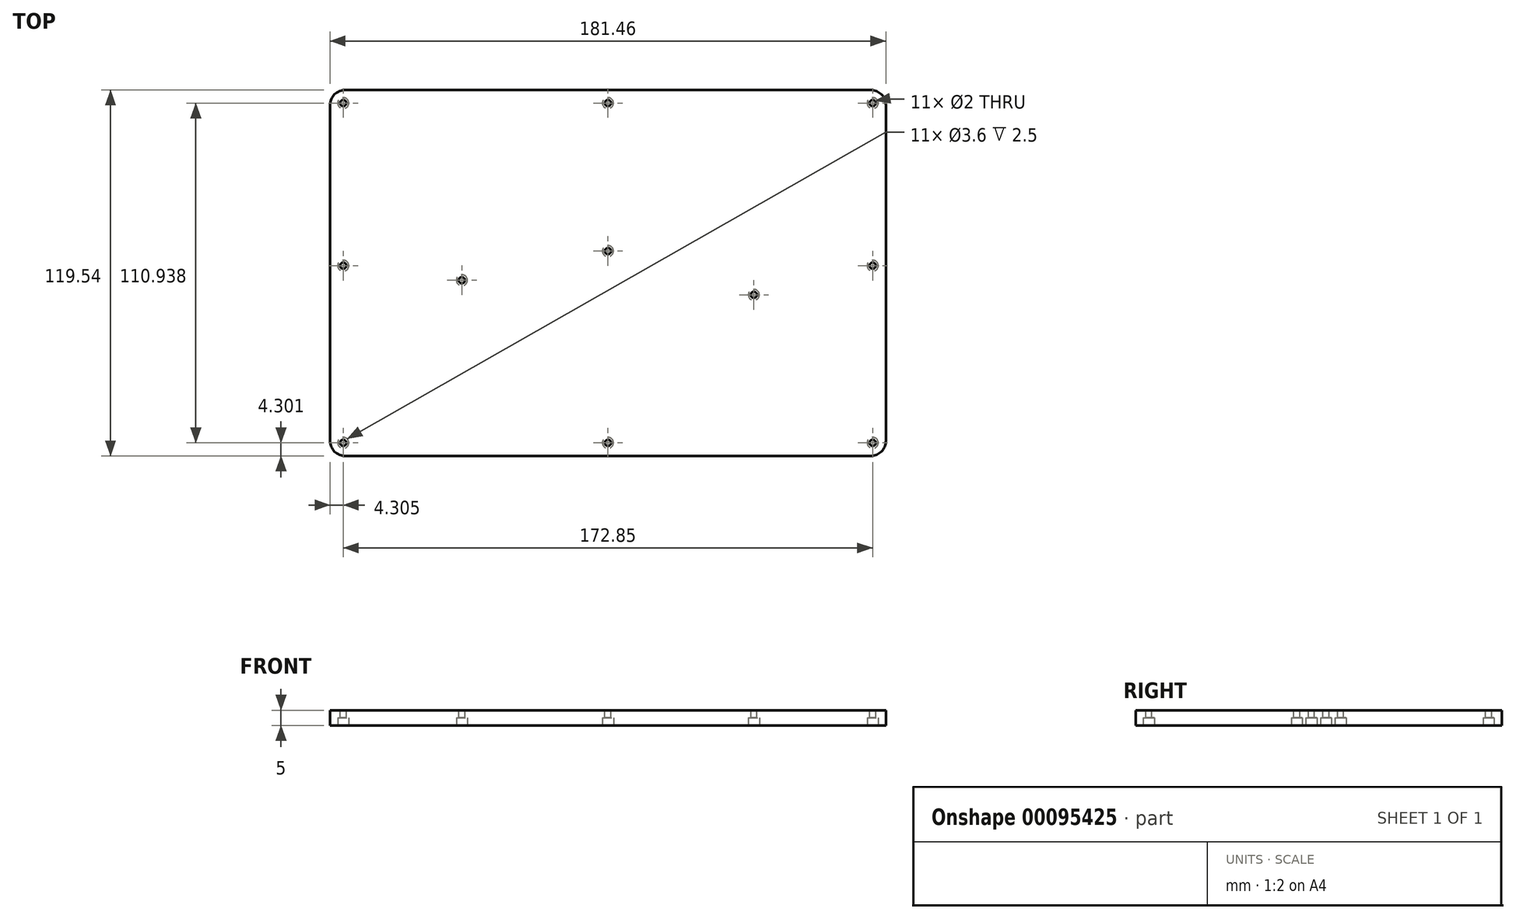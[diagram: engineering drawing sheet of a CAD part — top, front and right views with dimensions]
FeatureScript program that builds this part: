
annotation { "Feature Type Name" : "Feature", "Feature Type Description" : "" }
export const myFeature = defineFeature(function(context is Context, id is Id, definition is map)
    precondition{}
    {
        {
            var Q0;
            Q0=qCreatedBy(makeId("Top.planeOp"),FACE);
            var sketch = newSketch(context, id + "F0", { "sketchPlane" : qUnion([Q0])});
            skLineSegment(sketch, "E0", {"start": v(-90.73, 59.77) * mm, "end": v(90.73, 59.77) * mm});
            skLineSegment(sketch, "E1", {"start": v(90.73, 59.77) * mm, "end": v(90.73, -59.77) * mm});
            skLineSegment(sketch, "E2", {"start": v(90.73, -59.77) * mm, "end": v(-90.73, -59.77) * mm});
            skLineSegment(sketch, "E3", {"start": v(-90.73, -59.77) * mm, "end": v(-90.73, 59.77) * mm});
            skLineSegment(sketch, "E4", {"start": v(-70.2, -42.72) * mm, "end": v(-70.2, -43.52) * mm});
            skLineSegment(sketch, "E5", {"start": v(-70.2, -43.52) * mm, "end": v(-71.47, -43.52) * mm});
            skLineSegment(sketch, "E6", {"start": v(-71.47, -43.52) * mm, "end": v(-71.47, -44.3) * mm});
            skLineSegment(sketch, "E7", {"start": v(-71.47, -44.3) * mm, "end": v(-70.67, -44.3) * mm});
            skLineSegment(sketch, "E8", {"start": v(-70.67, -44.3) * mm, "end": v(-70.67, -46.02) * mm});
            skLineSegment(sketch, "E9", {"start": v(-70.67, -46.02) * mm, "end": v(-69.75, -46.02) * mm});
            skLineSegment(sketch, "E10", {"start": v(-69.75, -46.02) * mm, "end": v(-69.75, -49.32) * mm});
            skLineSegment(sketch, "E11", {"start": v(-69.75, -49.32) * mm, "end": v(-70.67, -49.32) * mm});
            skLineSegment(sketch, "E12", {"start": v(-70.67, -49.32) * mm, "end": v(-70.67, -50.94) * mm});
            skLineSegment(sketch, "E13", {"start": v(-70.67, -50.94) * mm, "end": v(-73.9, -50.94) * mm});
            skLineSegment(sketch, "E14", {"start": v(-73.9, -50.94) * mm, "end": v(-73.9, -51.82) * mm});
            skLineSegment(sketch, "E15", {"start": v(-73.9, -51.82) * mm, "end": v(-76.7, -51.82) * mm});
            skLineSegment(sketch, "E16", {"start": v(-76.7, -51.82) * mm, "end": v(-76.7, -50.94) * mm});
            skLineSegment(sketch, "E17", {"start": v(-76.7, -50.94) * mm, "end": v(-82.97, -50.94) * mm});
            skLineSegment(sketch, "E18", {"start": v(-82.97, -50.94) * mm, "end": v(-82.97, -49.32) * mm});
            skLineSegment(sketch, "E19", {"start": v(-82.97, -49.32) * mm, "end": v(-83.95, -49.32) * mm});
            skLineSegment(sketch, "E20", {"start": v(-83.95, -49.32) * mm, "end": v(-83.95, -46.02) * mm});
            skLineSegment(sketch, "E21", {"start": v(-83.95, -46.02) * mm, "end": v(-82.97, -46.02) * mm});
            skLineSegment(sketch, "E22", {"start": v(-82.97, -46.02) * mm, "end": v(-82.97, -44.3) * mm});
            skLineSegment(sketch, "E23", {"start": v(-82.97, -44.3) * mm, "end": v(-82.17, -44.3) * mm});
            skLineSegment(sketch, "E24", {"start": v(-82.17, -44.3) * mm, "end": v(-82.17, -43.52) * mm});
            skLineSegment(sketch, "E25", {"start": v(-82.17, -43.52) * mm, "end": v(-82.2, -43.52) * mm});
            skLineSegment(sketch, "E26", {"start": v(-82.2, -43.52) * mm, "end": v(-82.2, -42.72) * mm});
            skLineSegment(sketch, "E27", {"start": v(-82.2, -42.72) * mm, "end": v(-83.2, -42.72) * mm});
            skLineSegment(sketch, "E28", {"start": v(-83.2, -42.72) * mm, "end": v(-83.2, -28.72) * mm});
            skLineSegment(sketch, "E29", {"start": v(-83.2, -28.72) * mm, "end": v(-82.2, -28.72) * mm});
            skLineSegment(sketch, "E30", {"start": v(-82.2, -28.72) * mm, "end": v(-82.2, -27.92) * mm});
            skLineSegment(sketch, "E31", {"start": v(-82.2, -27.92) * mm, "end": v(-82.17, -27.92) * mm});
            skLineSegment(sketch, "E32", {"start": v(-82.17, -27.92) * mm, "end": v(-82.17, -27.14) * mm});
            skLineSegment(sketch, "E33", {"start": v(-82.17, -27.14) * mm, "end": v(-82.97, -27.14) * mm});
            skLineSegment(sketch, "E34", {"start": v(-82.97, -27.14) * mm, "end": v(-82.97, -25.42) * mm});
            skLineSegment(sketch, "E35", {"start": v(-82.97, -25.42) * mm, "end": v(-83.95, -25.42) * mm});
            skLineSegment(sketch, "E36", {"start": v(-83.95, -25.42) * mm, "end": v(-83.95, -22.12) * mm});
            skLineSegment(sketch, "E37", {"start": v(-83.95, -22.12) * mm, "end": v(-82.97, -22.12) * mm});
            skLineSegment(sketch, "E38", {"start": v(-82.97, -22.12) * mm, "end": v(-82.97, -20.5) * mm});
            skLineSegment(sketch, "E39", {"start": v(-82.97, -20.5) * mm, "end": v(-76.7, -20.5) * mm});
            skLineSegment(sketch, "E40", {"start": v(-76.7, -20.5) * mm, "end": v(-76.7, -19.62) * mm});
            skLineSegment(sketch, "E41", {"start": v(-76.7, -19.62) * mm, "end": v(-73.9, -19.62) * mm});
            skLineSegment(sketch, "E42", {"start": v(-73.9, -19.62) * mm, "end": v(-73.9, -20.5) * mm});
            skLineSegment(sketch, "E43", {"start": v(-73.9, -20.5) * mm, "end": v(-70.67, -20.5) * mm});
            skLineSegment(sketch, "E44", {"start": v(-70.67, -20.5) * mm, "end": v(-70.67, -22.12) * mm});
            skLineSegment(sketch, "E45", {"start": v(-70.67, -22.12) * mm, "end": v(-69.75, -22.12) * mm});
            skLineSegment(sketch, "E46", {"start": v(-69.75, -22.12) * mm, "end": v(-69.75, -25.42) * mm});
            skLineSegment(sketch, "E47", {"start": v(-69.75, -25.42) * mm, "end": v(-70.67, -25.42) * mm});
            skLineSegment(sketch, "E48", {"start": v(-70.67, -25.42) * mm, "end": v(-70.67, -27.14) * mm});
            skLineSegment(sketch, "E49", {"start": v(-70.67, -27.14) * mm, "end": v(-71.47, -27.14) * mm});
            skLineSegment(sketch, "E50", {"start": v(-71.47, -27.14) * mm, "end": v(-71.47, -27.92) * mm});
            skLineSegment(sketch, "E51", {"start": v(-71.47, -27.92) * mm, "end": v(-70.2, -27.92) * mm});
            skLineSegment(sketch, "E52", {"start": v(-70.2, -27.92) * mm, "end": v(-70.2, -28.72) * mm});
            skLineSegment(sketch, "E53", {"start": v(-70.2, -28.72) * mm, "end": v(-69.2, -28.72) * mm});
            skLineSegment(sketch, "E54", {"start": v(-69.2, -28.72) * mm, "end": v(-69.2, -42.72) * mm});
            skLineSegment(sketch, "E55", {"start": v(-69.2, -42.72) * mm, "end": v(-70.2, -42.72) * mm});
            skLineSegment(sketch, "E56", {"start": v(-69.2, 24.96) * mm, "end": v(-69.2, 23.96) * mm});
            skLineSegment(sketch, "E57", {"start": v(-69.2, 23.96) * mm, "end": v(-83.2, 23.96) * mm});
            skLineSegment(sketch, "E58", {"start": v(-83.2, 23.96) * mm, "end": v(-83.2, 24.96) * mm});
            skLineSegment(sketch, "E59", {"start": v(-83.2, 24.96) * mm, "end": v(-84, 24.96) * mm});
            skLineSegment(sketch, "E60", {"start": v(-84, 24.96) * mm, "end": v(-84, 28.06) * mm});
            skLineSegment(sketch, "E61", {"start": v(-84, 28.06) * mm, "end": v(-83.2, 28.06) * mm});
            skLineSegment(sketch, "E62", {"start": v(-83.2, 28.06) * mm, "end": v(-83.2, 33.86) * mm});
            skLineSegment(sketch, "E63", {"start": v(-83.2, 33.86) * mm, "end": v(-84, 33.86) * mm});
            skLineSegment(sketch, "E64", {"start": v(-84, 33.86) * mm, "end": v(-84, 36.96) * mm});
            skLineSegment(sketch, "E65", {"start": v(-84, 36.96) * mm, "end": v(-83.2, 36.96) * mm});
            skLineSegment(sketch, "E66", {"start": v(-83.2, 36.96) * mm, "end": v(-83.2, 37.96) * mm});
            skLineSegment(sketch, "E67", {"start": v(-83.2, 37.96) * mm, "end": v(-69.2, 37.96) * mm});
            skLineSegment(sketch, "E68", {"start": v(-69.2, 37.96) * mm, "end": v(-69.2, 36.96) * mm});
            skLineSegment(sketch, "E69", {"start": v(-69.2, 36.96) * mm, "end": v(-68.4, 36.96) * mm});
            skLineSegment(sketch, "E70", {"start": v(-68.4, 36.96) * mm, "end": v(-68.4, 33.86) * mm});
            skLineSegment(sketch, "E71", {"start": v(-68.4, 33.86) * mm, "end": v(-69.2, 33.86) * mm});
            skLineSegment(sketch, "E72", {"start": v(-69.2, 33.86) * mm, "end": v(-69.2, 28.06) * mm});
            skLineSegment(sketch, "E73", {"start": v(-69.2, 28.06) * mm, "end": v(-68.4, 28.06) * mm});
            skLineSegment(sketch, "E74", {"start": v(-68.4, 28.06) * mm, "end": v(-68.4, 24.96) * mm});
            skLineSegment(sketch, "E75", {"start": v(-68.4, 24.96) * mm, "end": v(-69.2, 24.96) * mm});
            skLineSegment(sketch, "E76", {"start": v(-69.2, 5.9) * mm, "end": v(-69.2, 4.9) * mm});
            skLineSegment(sketch, "E77", {"start": v(-69.2, 4.9) * mm, "end": v(-83.2, 4.9) * mm});
            skLineSegment(sketch, "E78", {"start": v(-83.2, 4.9) * mm, "end": v(-83.2, 5.9) * mm});
            skLineSegment(sketch, "E79", {"start": v(-83.2, 5.9) * mm, "end": v(-84, 5.9) * mm});
            skLineSegment(sketch, "E80", {"start": v(-84, 5.9) * mm, "end": v(-84, 9) * mm});
            skLineSegment(sketch, "E81", {"start": v(-84, 9) * mm, "end": v(-83.2, 9) * mm});
            skLineSegment(sketch, "E82", {"start": v(-83.2, 9) * mm, "end": v(-83.2, 14.8) * mm});
            skLineSegment(sketch, "E83", {"start": v(-83.2, 14.8) * mm, "end": v(-84, 14.8) * mm});
            skLineSegment(sketch, "E84", {"start": v(-84, 14.8) * mm, "end": v(-84, 17.9) * mm});
            skLineSegment(sketch, "E85", {"start": v(-84, 17.9) * mm, "end": v(-83.2, 17.9) * mm});
            skLineSegment(sketch, "E86", {"start": v(-83.2, 17.9) * mm, "end": v(-83.2, 18.9) * mm});
            skLineSegment(sketch, "E87", {"start": v(-83.2, 18.9) * mm, "end": v(-69.2, 18.9) * mm});
            skLineSegment(sketch, "E88", {"start": v(-69.2, 18.9) * mm, "end": v(-69.2, 17.9) * mm});
            skLineSegment(sketch, "E89", {"start": v(-69.2, 17.9) * mm, "end": v(-68.4, 17.9) * mm});
            skLineSegment(sketch, "E90", {"start": v(-68.4, 17.9) * mm, "end": v(-68.4, 14.8) * mm});
            skLineSegment(sketch, "E91", {"start": v(-68.4, 14.8) * mm, "end": v(-69.2, 14.8) * mm});
            skLineSegment(sketch, "E92", {"start": v(-69.2, 14.8) * mm, "end": v(-69.2, 9) * mm});
            skLineSegment(sketch, "E93", {"start": v(-69.2, 9) * mm, "end": v(-68.4, 9) * mm});
            skLineSegment(sketch, "E94", {"start": v(-68.4, 9) * mm, "end": v(-68.4, 5.9) * mm});
            skLineSegment(sketch, "E95", {"start": v(-68.4, 5.9) * mm, "end": v(-69.2, 5.9) * mm});
            skLineSegment(sketch, "E96", {"start": v(-69.2, -13.14) * mm, "end": v(-69.2, -14.14) * mm});
            skLineSegment(sketch, "E97", {"start": v(-69.2, -14.14) * mm, "end": v(-83.2, -14.14) * mm});
            skLineSegment(sketch, "E98", {"start": v(-83.2, -14.14) * mm, "end": v(-83.2, -13.14) * mm});
            skLineSegment(sketch, "E99", {"start": v(-83.2, -13.14) * mm, "end": v(-84, -13.14) * mm});
            skLineSegment(sketch, "E100", {"start": v(-84, -13.14) * mm, "end": v(-84, -10.04) * mm});
            skLineSegment(sketch, "E101", {"start": v(-84, -10.04) * mm, "end": v(-83.2, -10.04) * mm});
            skLineSegment(sketch, "E102", {"start": v(-83.2, -10.04) * mm, "end": v(-83.2, -4.24) * mm});
            skLineSegment(sketch, "E103", {"start": v(-83.2, -4.24) * mm, "end": v(-84, -4.24) * mm});
            skLineSegment(sketch, "E104", {"start": v(-84, -4.24) * mm, "end": v(-84, -1.14) * mm});
            skLineSegment(sketch, "E105", {"start": v(-84, -1.14) * mm, "end": v(-83.2, -1.14) * mm});
            skLineSegment(sketch, "E106", {"start": v(-83.2, -1.14) * mm, "end": v(-83.2, -0.14) * mm});
            skLineSegment(sketch, "E107", {"start": v(-83.2, -0.14) * mm, "end": v(-69.2, -0.14) * mm});
            skLineSegment(sketch, "E108", {"start": v(-69.2, -0.14) * mm, "end": v(-69.2, -1.14) * mm});
            skLineSegment(sketch, "E109", {"start": v(-69.2, -1.14) * mm, "end": v(-68.4, -1.14) * mm});
            skLineSegment(sketch, "E110", {"start": v(-68.4, -1.14) * mm, "end": v(-68.4, -4.24) * mm});
            skLineSegment(sketch, "E111", {"start": v(-68.4, -4.24) * mm, "end": v(-69.2, -4.24) * mm});
            skLineSegment(sketch, "E112", {"start": v(-69.2, -4.24) * mm, "end": v(-69.2, -10.04) * mm});
            skLineSegment(sketch, "E113", {"start": v(-69.2, -10.04) * mm, "end": v(-68.4, -10.04) * mm});
            skLineSegment(sketch, "E114", {"start": v(-68.4, -10.04) * mm, "end": v(-68.4, -13.14) * mm});
            skLineSegment(sketch, "E115", {"start": v(-68.4, -13.14) * mm, "end": v(-69.2, -13.14) * mm});
            skLineSegment(sketch, "E116", {"start": v(-50.15, 29.72) * mm, "end": v(-50.15, 28.72) * mm});
            skLineSegment(sketch, "E117", {"start": v(-50.15, 28.72) * mm, "end": v(-64.15, 28.72) * mm});
            skLineSegment(sketch, "E118", {"start": v(-64.15, 28.72) * mm, "end": v(-64.15, 29.72) * mm});
            skLineSegment(sketch, "E119", {"start": v(-64.15, 29.72) * mm, "end": v(-64.95, 29.72) * mm});
            skLineSegment(sketch, "E120", {"start": v(-64.95, 29.72) * mm, "end": v(-64.95, 32.82) * mm});
            skLineSegment(sketch, "E121", {"start": v(-64.95, 32.82) * mm, "end": v(-64.15, 32.82) * mm});
            skLineSegment(sketch, "E122", {"start": v(-64.15, 32.82) * mm, "end": v(-64.15, 38.62) * mm});
            skLineSegment(sketch, "E123", {"start": v(-64.15, 38.62) * mm, "end": v(-64.95, 38.62) * mm});
            skLineSegment(sketch, "E124", {"start": v(-64.95, 38.62) * mm, "end": v(-64.95, 41.72) * mm});
            skLineSegment(sketch, "E125", {"start": v(-64.95, 41.72) * mm, "end": v(-64.15, 41.72) * mm});
            skLineSegment(sketch, "E126", {"start": v(-64.15, 41.72) * mm, "end": v(-64.15, 42.72) * mm});
            skLineSegment(sketch, "E127", {"start": v(-64.15, 42.72) * mm, "end": v(-50.15, 42.72) * mm});
            skLineSegment(sketch, "E128", {"start": v(-50.15, 42.72) * mm, "end": v(-50.15, 41.72) * mm});
            skLineSegment(sketch, "E129", {"start": v(-50.15, 41.72) * mm, "end": v(-49.35, 41.72) * mm});
            skLineSegment(sketch, "E130", {"start": v(-49.35, 41.72) * mm, "end": v(-49.35, 38.62) * mm});
            skLineSegment(sketch, "E131", {"start": v(-49.35, 38.62) * mm, "end": v(-50.15, 38.62) * mm});
            skLineSegment(sketch, "E132", {"start": v(-50.15, 38.62) * mm, "end": v(-50.15, 32.82) * mm});
            skLineSegment(sketch, "E133", {"start": v(-50.15, 32.82) * mm, "end": v(-49.35, 32.82) * mm});
            skLineSegment(sketch, "E134", {"start": v(-49.35, 32.82) * mm, "end": v(-49.35, 29.72) * mm});
            skLineSegment(sketch, "E135", {"start": v(-49.35, 29.72) * mm, "end": v(-50.15, 29.72) * mm});
            skLineSegment(sketch, "E136", {"start": v(-50.15, 10.67) * mm, "end": v(-50.15, 9.67) * mm});
            skLineSegment(sketch, "E137", {"start": v(-50.15, 9.67) * mm, "end": v(-64.15, 9.67) * mm});
            skLineSegment(sketch, "E138", {"start": v(-64.15, 9.67) * mm, "end": v(-64.15, 10.67) * mm});
            skLineSegment(sketch, "E139", {"start": v(-64.15, 10.67) * mm, "end": v(-64.95, 10.67) * mm});
            skLineSegment(sketch, "E140", {"start": v(-64.95, 10.67) * mm, "end": v(-64.95, 13.77) * mm});
            skLineSegment(sketch, "E141", {"start": v(-64.95, 13.77) * mm, "end": v(-64.15, 13.77) * mm});
            skLineSegment(sketch, "E142", {"start": v(-64.15, 13.77) * mm, "end": v(-64.15, 19.57) * mm});
            skLineSegment(sketch, "E143", {"start": v(-64.15, 19.57) * mm, "end": v(-64.95, 19.57) * mm});
            skLineSegment(sketch, "E144", {"start": v(-64.95, 19.57) * mm, "end": v(-64.95, 22.67) * mm});
            skLineSegment(sketch, "E145", {"start": v(-64.95, 22.67) * mm, "end": v(-64.15, 22.67) * mm});
            skLineSegment(sketch, "E146", {"start": v(-64.15, 22.67) * mm, "end": v(-64.15, 23.67) * mm});
            skLineSegment(sketch, "E147", {"start": v(-64.15, 23.67) * mm, "end": v(-50.15, 23.67) * mm});
            skLineSegment(sketch, "E148", {"start": v(-50.15, 23.67) * mm, "end": v(-50.15, 22.67) * mm});
            skLineSegment(sketch, "E149", {"start": v(-50.15, 22.67) * mm, "end": v(-49.35, 22.67) * mm});
            skLineSegment(sketch, "E150", {"start": v(-49.35, 22.67) * mm, "end": v(-49.35, 19.57) * mm});
            skLineSegment(sketch, "E151", {"start": v(-49.35, 19.57) * mm, "end": v(-50.15, 19.57) * mm});
            skLineSegment(sketch, "E152", {"start": v(-50.15, 19.57) * mm, "end": v(-50.15, 13.77) * mm});
            skLineSegment(sketch, "E153", {"start": v(-50.15, 13.77) * mm, "end": v(-49.35, 13.77) * mm});
            skLineSegment(sketch, "E154", {"start": v(-49.35, 13.77) * mm, "end": v(-49.35, 10.67) * mm});
            skLineSegment(sketch, "E155", {"start": v(-49.35, 10.67) * mm, "end": v(-50.15, 10.67) * mm});
            skLineSegment(sketch, "E156", {"start": v(-50.15, -8.38) * mm, "end": v(-50.15, -9.38) * mm});
            skLineSegment(sketch, "E157", {"start": v(-50.15, -9.38) * mm, "end": v(-64.15, -9.38) * mm});
            skLineSegment(sketch, "E158", {"start": v(-64.15, -9.38) * mm, "end": v(-64.15, -8.38) * mm});
            skLineSegment(sketch, "E159", {"start": v(-64.15, -8.38) * mm, "end": v(-64.95, -8.38) * mm});
            skLineSegment(sketch, "E160", {"start": v(-64.95, -8.38) * mm, "end": v(-64.95, -5.28) * mm});
            skLineSegment(sketch, "E161", {"start": v(-64.95, -5.28) * mm, "end": v(-64.15, -5.28) * mm});
            skLineSegment(sketch, "E162", {"start": v(-64.15, -5.28) * mm, "end": v(-64.15, 0.52) * mm});
            skLineSegment(sketch, "E163", {"start": v(-64.15, 0.52) * mm, "end": v(-64.95, 0.52) * mm});
            skLineSegment(sketch, "E164", {"start": v(-64.95, 0.52) * mm, "end": v(-64.95, 3.62) * mm});
            skLineSegment(sketch, "E165", {"start": v(-64.95, 3.62) * mm, "end": v(-64.15, 3.62) * mm});
            skLineSegment(sketch, "E166", {"start": v(-64.15, 3.62) * mm, "end": v(-64.15, 4.62) * mm});
            skLineSegment(sketch, "E167", {"start": v(-64.15, 4.62) * mm, "end": v(-50.15, 4.62) * mm});
            skLineSegment(sketch, "E168", {"start": v(-50.15, 4.62) * mm, "end": v(-50.15, 3.62) * mm});
            skLineSegment(sketch, "E169", {"start": v(-50.15, 3.62) * mm, "end": v(-49.35, 3.62) * mm});
            skLineSegment(sketch, "E170", {"start": v(-49.35, 3.62) * mm, "end": v(-49.35, 0.52) * mm});
            skLineSegment(sketch, "E171", {"start": v(-49.35, 0.52) * mm, "end": v(-50.15, 0.52) * mm});
            skLineSegment(sketch, "E172", {"start": v(-50.15, 0.52) * mm, "end": v(-50.15, -5.28) * mm});
            skLineSegment(sketch, "E173", {"start": v(-50.15, -5.28) * mm, "end": v(-49.35, -5.28) * mm});
            skLineSegment(sketch, "E174", {"start": v(-49.35, -5.28) * mm, "end": v(-49.35, -8.38) * mm});
            skLineSegment(sketch, "E175", {"start": v(-49.35, -8.38) * mm, "end": v(-50.15, -8.38) * mm});
            skLineSegment(sketch, "E176", {"start": v(-50.15, -27.43) * mm, "end": v(-50.15, -28.43) * mm});
            skLineSegment(sketch, "E177", {"start": v(-50.15, -28.43) * mm, "end": v(-64.15, -28.43) * mm});
            skLineSegment(sketch, "E178", {"start": v(-64.15, -28.43) * mm, "end": v(-64.15, -27.43) * mm});
            skLineSegment(sketch, "E179", {"start": v(-64.15, -27.43) * mm, "end": v(-64.95, -27.43) * mm});
            skLineSegment(sketch, "E180", {"start": v(-64.95, -27.43) * mm, "end": v(-64.95, -24.33) * mm});
            skLineSegment(sketch, "E181", {"start": v(-64.95, -24.33) * mm, "end": v(-64.15, -24.33) * mm});
            skLineSegment(sketch, "E182", {"start": v(-64.15, -24.33) * mm, "end": v(-64.15, -18.53) * mm});
            skLineSegment(sketch, "E183", {"start": v(-64.15, -18.53) * mm, "end": v(-64.95, -18.53) * mm});
            skLineSegment(sketch, "E184", {"start": v(-64.95, -18.53) * mm, "end": v(-64.95, -15.43) * mm});
            skLineSegment(sketch, "E185", {"start": v(-64.95, -15.43) * mm, "end": v(-64.15, -15.43) * mm});
            skLineSegment(sketch, "E186", {"start": v(-64.15, -15.43) * mm, "end": v(-64.15, -14.43) * mm});
            skLineSegment(sketch, "E187", {"start": v(-64.15, -14.43) * mm, "end": v(-50.15, -14.43) * mm});
            skLineSegment(sketch, "E188", {"start": v(-50.15, -14.43) * mm, "end": v(-50.15, -15.43) * mm});
            skLineSegment(sketch, "E189", {"start": v(-50.15, -15.43) * mm, "end": v(-49.35, -15.43) * mm});
            skLineSegment(sketch, "E190", {"start": v(-49.35, -15.43) * mm, "end": v(-49.35, -18.53) * mm});
            skLineSegment(sketch, "E191", {"start": v(-49.35, -18.53) * mm, "end": v(-50.15, -18.53) * mm});
            skLineSegment(sketch, "E192", {"start": v(-50.15, -18.53) * mm, "end": v(-50.15, -24.33) * mm});
            skLineSegment(sketch, "E193", {"start": v(-50.15, -24.33) * mm, "end": v(-49.35, -24.33) * mm});
            skLineSegment(sketch, "E194", {"start": v(-49.35, -24.33) * mm, "end": v(-49.35, -27.43) * mm});
            skLineSegment(sketch, "E195", {"start": v(-49.35, -27.43) * mm, "end": v(-50.15, -27.43) * mm});
            skLineSegment(sketch, "E196", {"start": v(-50.15, -46.48) * mm, "end": v(-50.15, -47.48) * mm});
            skLineSegment(sketch, "E197", {"start": v(-50.15, -47.48) * mm, "end": v(-64.15, -47.48) * mm});
            skLineSegment(sketch, "E198", {"start": v(-64.15, -47.48) * mm, "end": v(-64.15, -46.48) * mm});
            skLineSegment(sketch, "E199", {"start": v(-64.15, -46.48) * mm, "end": v(-64.95, -46.48) * mm});
            skLineSegment(sketch, "E200", {"start": v(-64.95, -46.48) * mm, "end": v(-64.95, -43.38) * mm});
            skLineSegment(sketch, "E201", {"start": v(-64.95, -43.38) * mm, "end": v(-64.15, -43.38) * mm});
            skLineSegment(sketch, "E202", {"start": v(-64.15, -43.38) * mm, "end": v(-64.15, -37.58) * mm});
            skLineSegment(sketch, "E203", {"start": v(-64.15, -37.58) * mm, "end": v(-64.95, -37.58) * mm});
            skLineSegment(sketch, "E204", {"start": v(-64.95, -37.58) * mm, "end": v(-64.95, -34.48) * mm});
            skLineSegment(sketch, "E205", {"start": v(-64.95, -34.48) * mm, "end": v(-64.15, -34.48) * mm});
            skLineSegment(sketch, "E206", {"start": v(-64.15, -34.48) * mm, "end": v(-64.15, -33.48) * mm});
            skLineSegment(sketch, "E207", {"start": v(-64.15, -33.48) * mm, "end": v(-50.15, -33.48) * mm});
            skLineSegment(sketch, "E208", {"start": v(-50.15, -33.48) * mm, "end": v(-50.15, -34.48) * mm});
            skLineSegment(sketch, "E209", {"start": v(-50.15, -34.48) * mm, "end": v(-49.35, -34.48) * mm});
            skLineSegment(sketch, "E210", {"start": v(-49.35, -34.48) * mm, "end": v(-49.35, -37.58) * mm});
            skLineSegment(sketch, "E211", {"start": v(-49.35, -37.58) * mm, "end": v(-50.15, -37.58) * mm});
            skLineSegment(sketch, "E212", {"start": v(-50.15, -37.58) * mm, "end": v(-50.15, -43.38) * mm});
            skLineSegment(sketch, "E213", {"start": v(-50.15, -43.38) * mm, "end": v(-49.35, -43.38) * mm});
            skLineSegment(sketch, "E214", {"start": v(-49.35, -43.38) * mm, "end": v(-49.35, -46.48) * mm});
            skLineSegment(sketch, "E215", {"start": v(-49.35, -46.48) * mm, "end": v(-50.15, -46.48) * mm});
            skLineSegment(sketch, "E216", {"start": v(-31.1, 39.24) * mm, "end": v(-31.1, 38.24) * mm});
            skLineSegment(sketch, "E217", {"start": v(-31.1, 38.24) * mm, "end": v(-45.1, 38.24) * mm});
            skLineSegment(sketch, "E218", {"start": v(-45.1, 38.24) * mm, "end": v(-45.1, 39.24) * mm});
            skLineSegment(sketch, "E219", {"start": v(-45.1, 39.24) * mm, "end": v(-45.9, 39.24) * mm});
            skLineSegment(sketch, "E220", {"start": v(-45.9, 39.24) * mm, "end": v(-45.9, 42.34) * mm});
            skLineSegment(sketch, "E221", {"start": v(-45.9, 42.34) * mm, "end": v(-45.1, 42.34) * mm});
            skLineSegment(sketch, "E222", {"start": v(-45.1, 42.34) * mm, "end": v(-45.1, 48.14) * mm});
            skLineSegment(sketch, "E223", {"start": v(-45.1, 48.14) * mm, "end": v(-45.9, 48.14) * mm});
            skLineSegment(sketch, "E224", {"start": v(-45.9, 48.14) * mm, "end": v(-45.9, 51.24) * mm});
            skLineSegment(sketch, "E225", {"start": v(-45.9, 51.24) * mm, "end": v(-45.1, 51.24) * mm});
            skLineSegment(sketch, "E226", {"start": v(-45.1, 51.24) * mm, "end": v(-45.1, 52.24) * mm});
            skLineSegment(sketch, "E227", {"start": v(-45.1, 52.24) * mm, "end": v(-31.1, 52.24) * mm});
            skLineSegment(sketch, "E228", {"start": v(-31.1, 52.24) * mm, "end": v(-31.1, 51.24) * mm});
            skLineSegment(sketch, "E229", {"start": v(-31.1, 51.24) * mm, "end": v(-30.3, 51.24) * mm});
            skLineSegment(sketch, "E230", {"start": v(-30.3, 51.24) * mm, "end": v(-30.3, 48.14) * mm});
            skLineSegment(sketch, "E231", {"start": v(-30.3, 48.14) * mm, "end": v(-31.1, 48.14) * mm});
            skLineSegment(sketch, "E232", {"start": v(-31.1, 48.14) * mm, "end": v(-31.1, 42.34) * mm});
            skLineSegment(sketch, "E233", {"start": v(-31.1, 42.34) * mm, "end": v(-30.3, 42.34) * mm});
            skLineSegment(sketch, "E234", {"start": v(-30.3, 42.34) * mm, "end": v(-30.3, 39.24) * mm});
            skLineSegment(sketch, "E235", {"start": v(-30.3, 39.24) * mm, "end": v(-31.1, 39.24) * mm});
            skLineSegment(sketch, "E236", {"start": v(-31.1, 20.2) * mm, "end": v(-31.1, 19.2) * mm});
            skLineSegment(sketch, "E237", {"start": v(-31.1, 19.2) * mm, "end": v(-45.1, 19.2) * mm});
            skLineSegment(sketch, "E238", {"start": v(-45.1, 19.2) * mm, "end": v(-45.1, 20.2) * mm});
            skLineSegment(sketch, "E239", {"start": v(-45.1, 20.2) * mm, "end": v(-45.9, 20.2) * mm});
            skLineSegment(sketch, "E240", {"start": v(-45.9, 20.2) * mm, "end": v(-45.9, 23.3) * mm});
            skLineSegment(sketch, "E241", {"start": v(-45.9, 23.3) * mm, "end": v(-45.1, 23.3) * mm});
            skLineSegment(sketch, "E242", {"start": v(-45.1, 23.3) * mm, "end": v(-45.1, 29.1) * mm});
            skLineSegment(sketch, "E243", {"start": v(-45.1, 29.1) * mm, "end": v(-45.9, 29.1) * mm});
            skLineSegment(sketch, "E244", {"start": v(-45.9, 29.1) * mm, "end": v(-45.9, 32.2) * mm});
            skLineSegment(sketch, "E245", {"start": v(-45.9, 32.2) * mm, "end": v(-45.1, 32.2) * mm});
            skLineSegment(sketch, "E246", {"start": v(-45.1, 32.2) * mm, "end": v(-45.1, 33.2) * mm});
            skLineSegment(sketch, "E247", {"start": v(-45.1, 33.2) * mm, "end": v(-31.1, 33.2) * mm});
            skLineSegment(sketch, "E248", {"start": v(-31.1, 33.2) * mm, "end": v(-31.1, 32.2) * mm});
            skLineSegment(sketch, "E249", {"start": v(-31.1, 32.2) * mm, "end": v(-30.3, 32.2) * mm});
            skLineSegment(sketch, "E250", {"start": v(-30.3, 32.2) * mm, "end": v(-30.3, 29.1) * mm});
            skLineSegment(sketch, "E251", {"start": v(-30.3, 29.1) * mm, "end": v(-31.1, 29.1) * mm});
            skLineSegment(sketch, "E252", {"start": v(-31.1, 29.1) * mm, "end": v(-31.1, 23.3) * mm});
            skLineSegment(sketch, "E253", {"start": v(-31.1, 23.3) * mm, "end": v(-30.3, 23.3) * mm});
            skLineSegment(sketch, "E254", {"start": v(-30.3, 23.3) * mm, "end": v(-30.3, 20.2) * mm});
            skLineSegment(sketch, "E255", {"start": v(-30.3, 20.2) * mm, "end": v(-31.1, 20.2) * mm});
            skLineSegment(sketch, "E256", {"start": v(-31.1, 1.14) * mm, "end": v(-31.1, 0.14) * mm});
            skLineSegment(sketch, "E257", {"start": v(-31.1, 0.14) * mm, "end": v(-45.1, 0.14) * mm});
            skLineSegment(sketch, "E258", {"start": v(-45.1, 0.14) * mm, "end": v(-45.1, 1.14) * mm});
            skLineSegment(sketch, "E259", {"start": v(-45.1, 1.14) * mm, "end": v(-45.9, 1.14) * mm});
            skLineSegment(sketch, "E260", {"start": v(-45.9, 1.14) * mm, "end": v(-45.9, 4.24) * mm});
            skLineSegment(sketch, "E261", {"start": v(-45.9, 4.24) * mm, "end": v(-45.1, 4.24) * mm});
            skLineSegment(sketch, "E262", {"start": v(-45.1, 4.24) * mm, "end": v(-45.1, 10.04) * mm});
            skLineSegment(sketch, "E263", {"start": v(-45.1, 10.04) * mm, "end": v(-45.9, 10.04) * mm});
            skLineSegment(sketch, "E264", {"start": v(-45.9, 10.04) * mm, "end": v(-45.9, 13.14) * mm});
            skLineSegment(sketch, "E265", {"start": v(-45.9, 13.14) * mm, "end": v(-45.1, 13.14) * mm});
            skLineSegment(sketch, "E266", {"start": v(-45.1, 13.14) * mm, "end": v(-45.1, 14.14) * mm});
            skLineSegment(sketch, "E267", {"start": v(-45.1, 14.14) * mm, "end": v(-31.1, 14.14) * mm});
            skLineSegment(sketch, "E268", {"start": v(-31.1, 14.14) * mm, "end": v(-31.1, 13.14) * mm});
            skLineSegment(sketch, "E269", {"start": v(-31.1, 13.14) * mm, "end": v(-30.3, 13.14) * mm});
            skLineSegment(sketch, "E270", {"start": v(-30.3, 13.14) * mm, "end": v(-30.3, 10.04) * mm});
            skLineSegment(sketch, "E271", {"start": v(-30.3, 10.04) * mm, "end": v(-31.1, 10.04) * mm});
            skLineSegment(sketch, "E272", {"start": v(-31.1, 10.04) * mm, "end": v(-31.1, 4.24) * mm});
            skLineSegment(sketch, "E273", {"start": v(-31.1, 4.24) * mm, "end": v(-30.3, 4.24) * mm});
            skLineSegment(sketch, "E274", {"start": v(-30.3, 4.24) * mm, "end": v(-30.3, 1.14) * mm});
            skLineSegment(sketch, "E275", {"start": v(-30.3, 1.14) * mm, "end": v(-31.1, 1.14) * mm});
            skLineSegment(sketch, "E276", {"start": v(-31.1, -17.9) * mm, "end": v(-31.1, -18.9) * mm});
            skLineSegment(sketch, "E277", {"start": v(-31.1, -18.9) * mm, "end": v(-45.1, -18.9) * mm});
            skLineSegment(sketch, "E278", {"start": v(-45.1, -18.9) * mm, "end": v(-45.1, -17.9) * mm});
            skLineSegment(sketch, "E279", {"start": v(-45.1, -17.9) * mm, "end": v(-45.9, -17.9) * mm});
            skLineSegment(sketch, "E280", {"start": v(-45.9, -17.9) * mm, "end": v(-45.9, -14.8) * mm});
            skLineSegment(sketch, "E281", {"start": v(-45.9, -14.8) * mm, "end": v(-45.1, -14.8) * mm});
            skLineSegment(sketch, "E282", {"start": v(-45.1, -14.8) * mm, "end": v(-45.1, -9) * mm});
            skLineSegment(sketch, "E283", {"start": v(-45.1, -9) * mm, "end": v(-45.9, -9) * mm});
            skLineSegment(sketch, "E284", {"start": v(-45.9, -9) * mm, "end": v(-45.9, -5.9) * mm});
            skLineSegment(sketch, "E285", {"start": v(-45.9, -5.9) * mm, "end": v(-45.1, -5.9) * mm});
            skLineSegment(sketch, "E286", {"start": v(-45.1, -5.9) * mm, "end": v(-45.1, -4.9) * mm});
            skLineSegment(sketch, "E287", {"start": v(-45.1, -4.9) * mm, "end": v(-31.1, -4.9) * mm});
            skLineSegment(sketch, "E288", {"start": v(-31.1, -4.9) * mm, "end": v(-31.1, -5.9) * mm});
            skLineSegment(sketch, "E289", {"start": v(-31.1, -5.9) * mm, "end": v(-30.3, -5.9) * mm});
            skLineSegment(sketch, "E290", {"start": v(-30.3, -5.9) * mm, "end": v(-30.3, -9) * mm});
            skLineSegment(sketch, "E291", {"start": v(-30.3, -9) * mm, "end": v(-31.1, -9) * mm});
            skLineSegment(sketch, "E292", {"start": v(-31.1, -9) * mm, "end": v(-31.1, -14.8) * mm});
            skLineSegment(sketch, "E293", {"start": v(-31.1, -14.8) * mm, "end": v(-30.3, -14.8) * mm});
            skLineSegment(sketch, "E294", {"start": v(-30.3, -14.8) * mm, "end": v(-30.3, -17.9) * mm});
            skLineSegment(sketch, "E295", {"start": v(-30.3, -17.9) * mm, "end": v(-31.1, -17.9) * mm});
            skLineSegment(sketch, "E296", {"start": v(-31.1, -36.96) * mm, "end": v(-31.1, -37.96) * mm});
            skLineSegment(sketch, "E297", {"start": v(-31.1, -37.96) * mm, "end": v(-45.1, -37.96) * mm});
            skLineSegment(sketch, "E298", {"start": v(-45.1, -37.96) * mm, "end": v(-45.1, -36.96) * mm});
            skLineSegment(sketch, "E299", {"start": v(-45.1, -36.96) * mm, "end": v(-45.9, -36.96) * mm});
            skLineSegment(sketch, "E300", {"start": v(-45.9, -36.96) * mm, "end": v(-45.9, -33.86) * mm});
            skLineSegment(sketch, "E301", {"start": v(-45.9, -33.86) * mm, "end": v(-45.1, -33.86) * mm});
            skLineSegment(sketch, "E302", {"start": v(-45.1, -33.86) * mm, "end": v(-45.1, -28.06) * mm});
            skLineSegment(sketch, "E303", {"start": v(-45.1, -28.06) * mm, "end": v(-45.9, -28.06) * mm});
            skLineSegment(sketch, "E304", {"start": v(-45.9, -28.06) * mm, "end": v(-45.9, -24.96) * mm});
            skLineSegment(sketch, "E305", {"start": v(-45.9, -24.96) * mm, "end": v(-45.1, -24.96) * mm});
            skLineSegment(sketch, "E306", {"start": v(-45.1, -24.96) * mm, "end": v(-45.1, -23.96) * mm});
            skLineSegment(sketch, "E307", {"start": v(-45.1, -23.96) * mm, "end": v(-31.1, -23.96) * mm});
            skLineSegment(sketch, "E308", {"start": v(-31.1, -23.96) * mm, "end": v(-31.1, -24.96) * mm});
            skLineSegment(sketch, "E309", {"start": v(-31.1, -24.96) * mm, "end": v(-30.3, -24.96) * mm});
            skLineSegment(sketch, "E310", {"start": v(-30.3, -24.96) * mm, "end": v(-30.3, -28.06) * mm});
            skLineSegment(sketch, "E311", {"start": v(-30.3, -28.06) * mm, "end": v(-31.1, -28.06) * mm});
            skLineSegment(sketch, "E312", {"start": v(-31.1, -28.06) * mm, "end": v(-31.1, -33.86) * mm});
            skLineSegment(sketch, "E313", {"start": v(-31.1, -33.86) * mm, "end": v(-30.3, -33.86) * mm});
            skLineSegment(sketch, "E314", {"start": v(-30.3, -33.86) * mm, "end": v(-30.3, -36.96) * mm});
            skLineSegment(sketch, "E315", {"start": v(-30.3, -36.96) * mm, "end": v(-31.1, -36.96) * mm});
            skLineSegment(sketch, "E316", {"start": v(-12.05, 34.48) * mm, "end": v(-12.05, 33.48) * mm});
            skLineSegment(sketch, "E317", {"start": v(-12.05, 33.48) * mm, "end": v(-26.05, 33.48) * mm});
            skLineSegment(sketch, "E318", {"start": v(-26.05, 33.48) * mm, "end": v(-26.05, 34.48) * mm});
            skLineSegment(sketch, "E319", {"start": v(-26.05, 34.48) * mm, "end": v(-26.85, 34.48) * mm});
            skLineSegment(sketch, "E320", {"start": v(-26.85, 34.48) * mm, "end": v(-26.85, 37.58) * mm});
            skLineSegment(sketch, "E321", {"start": v(-26.85, 37.58) * mm, "end": v(-26.05, 37.58) * mm});
            skLineSegment(sketch, "E322", {"start": v(-26.05, 37.58) * mm, "end": v(-26.05, 43.38) * mm});
            skLineSegment(sketch, "E323", {"start": v(-26.05, 43.38) * mm, "end": v(-26.85, 43.38) * mm});
            skLineSegment(sketch, "E324", {"start": v(-26.85, 43.38) * mm, "end": v(-26.85, 46.48) * mm});
            skLineSegment(sketch, "E325", {"start": v(-26.85, 46.48) * mm, "end": v(-26.05, 46.48) * mm});
            skLineSegment(sketch, "E326", {"start": v(-26.05, 46.48) * mm, "end": v(-26.05, 47.48) * mm});
            skLineSegment(sketch, "E327", {"start": v(-26.05, 47.48) * mm, "end": v(-12.05, 47.48) * mm});
            skLineSegment(sketch, "E328", {"start": v(-12.05, 47.48) * mm, "end": v(-12.05, 46.48) * mm});
            skLineSegment(sketch, "E329", {"start": v(-12.05, 46.48) * mm, "end": v(-11.25, 46.48) * mm});
            skLineSegment(sketch, "E330", {"start": v(-11.25, 46.48) * mm, "end": v(-11.25, 43.38) * mm});
            skLineSegment(sketch, "E331", {"start": v(-11.25, 43.38) * mm, "end": v(-12.05, 43.38) * mm});
            skLineSegment(sketch, "E332", {"start": v(-12.05, 43.38) * mm, "end": v(-12.05, 37.58) * mm});
            skLineSegment(sketch, "E333", {"start": v(-12.05, 37.58) * mm, "end": v(-11.25, 37.58) * mm});
            skLineSegment(sketch, "E334", {"start": v(-11.25, 37.58) * mm, "end": v(-11.25, 34.48) * mm});
            skLineSegment(sketch, "E335", {"start": v(-11.25, 34.48) * mm, "end": v(-12.05, 34.48) * mm});
            skLineSegment(sketch, "E336", {"start": v(-12.05, 15.43) * mm, "end": v(-12.05, 14.43) * mm});
            skLineSegment(sketch, "E337", {"start": v(-12.05, 14.43) * mm, "end": v(-26.05, 14.43) * mm});
            skLineSegment(sketch, "E338", {"start": v(-26.05, 14.43) * mm, "end": v(-26.05, 15.43) * mm});
            skLineSegment(sketch, "E339", {"start": v(-26.05, 15.43) * mm, "end": v(-26.85, 15.43) * mm});
            skLineSegment(sketch, "E340", {"start": v(-26.85, 15.43) * mm, "end": v(-26.85, 18.53) * mm});
            skLineSegment(sketch, "E341", {"start": v(-26.85, 18.53) * mm, "end": v(-26.05, 18.53) * mm});
            skLineSegment(sketch, "E342", {"start": v(-26.05, 18.53) * mm, "end": v(-26.05, 24.33) * mm});
            skLineSegment(sketch, "E343", {"start": v(-26.05, 24.33) * mm, "end": v(-26.85, 24.33) * mm});
            skLineSegment(sketch, "E344", {"start": v(-26.85, 24.33) * mm, "end": v(-26.85, 27.43) * mm});
            skLineSegment(sketch, "E345", {"start": v(-26.85, 27.43) * mm, "end": v(-26.05, 27.43) * mm});
            skLineSegment(sketch, "E346", {"start": v(-26.05, 27.43) * mm, "end": v(-26.05, 28.43) * mm});
            skLineSegment(sketch, "E347", {"start": v(-26.05, 28.43) * mm, "end": v(-12.05, 28.43) * mm});
            skLineSegment(sketch, "E348", {"start": v(-12.05, 28.43) * mm, "end": v(-12.05, 27.43) * mm});
            skLineSegment(sketch, "E349", {"start": v(-12.05, 27.43) * mm, "end": v(-11.25, 27.43) * mm});
            skLineSegment(sketch, "E350", {"start": v(-11.25, 27.43) * mm, "end": v(-11.25, 24.33) * mm});
            skLineSegment(sketch, "E351", {"start": v(-11.25, 24.33) * mm, "end": v(-12.05, 24.33) * mm});
            skLineSegment(sketch, "E352", {"start": v(-12.05, 24.33) * mm, "end": v(-12.05, 18.53) * mm});
            skLineSegment(sketch, "E353", {"start": v(-12.05, 18.53) * mm, "end": v(-11.25, 18.53) * mm});
            skLineSegment(sketch, "E354", {"start": v(-11.25, 18.53) * mm, "end": v(-11.25, 15.43) * mm});
            skLineSegment(sketch, "E355", {"start": v(-11.25, 15.43) * mm, "end": v(-12.05, 15.43) * mm});
            skLineSegment(sketch, "E356", {"start": v(-12.05, -3.62) * mm, "end": v(-12.05, -4.62) * mm});
            skLineSegment(sketch, "E357", {"start": v(-12.05, -4.62) * mm, "end": v(-26.05, -4.62) * mm});
            skLineSegment(sketch, "E358", {"start": v(-26.05, -4.62) * mm, "end": v(-26.05, -3.62) * mm});
            skLineSegment(sketch, "E359", {"start": v(-26.05, -3.62) * mm, "end": v(-26.85, -3.62) * mm});
            skLineSegment(sketch, "E360", {"start": v(-26.85, -3.62) * mm, "end": v(-26.85, -0.52) * mm});
            skLineSegment(sketch, "E361", {"start": v(-26.85, -0.52) * mm, "end": v(-26.05, -0.52) * mm});
            skLineSegment(sketch, "E362", {"start": v(-26.05, -0.52) * mm, "end": v(-26.05, 5.28) * mm});
            skLineSegment(sketch, "E363", {"start": v(-26.05, 5.28) * mm, "end": v(-26.85, 5.28) * mm});
            skLineSegment(sketch, "E364", {"start": v(-26.85, 5.28) * mm, "end": v(-26.85, 8.38) * mm});
            skLineSegment(sketch, "E365", {"start": v(-26.85, 8.38) * mm, "end": v(-26.05, 8.38) * mm});
            skLineSegment(sketch, "E366", {"start": v(-26.05, 8.38) * mm, "end": v(-26.05, 9.38) * mm});
            skLineSegment(sketch, "E367", {"start": v(-26.05, 9.38) * mm, "end": v(-12.05, 9.38) * mm});
            skLineSegment(sketch, "E368", {"start": v(-12.05, 9.38) * mm, "end": v(-12.05, 8.38) * mm});
            skLineSegment(sketch, "E369", {"start": v(-12.05, 8.38) * mm, "end": v(-11.25, 8.38) * mm});
            skLineSegment(sketch, "E370", {"start": v(-11.25, 8.38) * mm, "end": v(-11.25, 5.28) * mm});
            skLineSegment(sketch, "E371", {"start": v(-11.25, 5.28) * mm, "end": v(-12.05, 5.28) * mm});
            skLineSegment(sketch, "E372", {"start": v(-12.05, 5.28) * mm, "end": v(-12.05, -0.52) * mm});
            skLineSegment(sketch, "E373", {"start": v(-12.05, -0.52) * mm, "end": v(-11.25, -0.52) * mm});
            skLineSegment(sketch, "E374", {"start": v(-11.25, -0.52) * mm, "end": v(-11.25, -3.62) * mm});
            skLineSegment(sketch, "E375", {"start": v(-11.25, -3.62) * mm, "end": v(-12.05, -3.62) * mm});
            skLineSegment(sketch, "E376", {"start": v(-12.05, -22.67) * mm, "end": v(-12.05, -23.67) * mm});
            skLineSegment(sketch, "E377", {"start": v(-12.05, -23.67) * mm, "end": v(-26.05, -23.67) * mm});
            skLineSegment(sketch, "E378", {"start": v(-26.05, -23.67) * mm, "end": v(-26.05, -22.67) * mm});
            skLineSegment(sketch, "E379", {"start": v(-26.05, -22.67) * mm, "end": v(-26.85, -22.67) * mm});
            skLineSegment(sketch, "E380", {"start": v(-26.85, -22.67) * mm, "end": v(-26.85, -19.57) * mm});
            skLineSegment(sketch, "E381", {"start": v(-26.85, -19.57) * mm, "end": v(-26.05, -19.57) * mm});
            skLineSegment(sketch, "E382", {"start": v(-26.05, -19.57) * mm, "end": v(-26.05, -13.77) * mm});
            skLineSegment(sketch, "E383", {"start": v(-26.05, -13.77) * mm, "end": v(-26.85, -13.77) * mm});
            skLineSegment(sketch, "E384", {"start": v(-26.85, -13.77) * mm, "end": v(-26.85, -10.67) * mm});
            skLineSegment(sketch, "E385", {"start": v(-26.85, -10.67) * mm, "end": v(-26.05, -10.67) * mm});
            skLineSegment(sketch, "E386", {"start": v(-26.05, -10.67) * mm, "end": v(-26.05, -9.67) * mm});
            skLineSegment(sketch, "E387", {"start": v(-26.05, -9.67) * mm, "end": v(-12.05, -9.67) * mm});
            skLineSegment(sketch, "E388", {"start": v(-12.05, -9.67) * mm, "end": v(-12.05, -10.67) * mm});
            skLineSegment(sketch, "E389", {"start": v(-12.05, -10.67) * mm, "end": v(-11.25, -10.67) * mm});
            skLineSegment(sketch, "E390", {"start": v(-11.25, -10.67) * mm, "end": v(-11.25, -13.77) * mm});
            skLineSegment(sketch, "E391", {"start": v(-11.25, -13.77) * mm, "end": v(-12.05, -13.77) * mm});
            skLineSegment(sketch, "E392", {"start": v(-12.05, -13.77) * mm, "end": v(-12.05, -19.57) * mm});
            skLineSegment(sketch, "E393", {"start": v(-12.05, -19.57) * mm, "end": v(-11.25, -19.57) * mm});
            skLineSegment(sketch, "E394", {"start": v(-11.25, -19.57) * mm, "end": v(-11.25, -22.67) * mm});
            skLineSegment(sketch, "E395", {"start": v(-11.25, -22.67) * mm, "end": v(-12.05, -22.67) * mm});
            skLineSegment(sketch, "E396", {"start": v(-12.05, -41.72) * mm, "end": v(-12.05, -42.72) * mm});
            skLineSegment(sketch, "E397", {"start": v(-12.05, -42.72) * mm, "end": v(-26.05, -42.72) * mm});
            skLineSegment(sketch, "E398", {"start": v(-26.05, -42.72) * mm, "end": v(-26.05, -41.72) * mm});
            skLineSegment(sketch, "E399", {"start": v(-26.05, -41.72) * mm, "end": v(-26.85, -41.72) * mm});
            skLineSegment(sketch, "E400", {"start": v(-26.85, -41.72) * mm, "end": v(-26.85, -38.62) * mm});
            skLineSegment(sketch, "E401", {"start": v(-26.85, -38.62) * mm, "end": v(-26.05, -38.62) * mm});
            skLineSegment(sketch, "E402", {"start": v(-26.05, -38.62) * mm, "end": v(-26.05, -32.82) * mm});
            skLineSegment(sketch, "E403", {"start": v(-26.05, -32.82) * mm, "end": v(-26.85, -32.82) * mm});
            skLineSegment(sketch, "E404", {"start": v(-26.85, -32.82) * mm, "end": v(-26.85, -29.72) * mm});
            skLineSegment(sketch, "E405", {"start": v(-26.85, -29.72) * mm, "end": v(-26.05, -29.72) * mm});
            skLineSegment(sketch, "E406", {"start": v(-26.05, -29.72) * mm, "end": v(-26.05, -28.72) * mm});
            skLineSegment(sketch, "E407", {"start": v(-26.05, -28.72) * mm, "end": v(-12.05, -28.72) * mm});
            skLineSegment(sketch, "E408", {"start": v(-12.05, -28.72) * mm, "end": v(-12.05, -29.72) * mm});
            skLineSegment(sketch, "E409", {"start": v(-12.05, -29.72) * mm, "end": v(-11.25, -29.72) * mm});
            skLineSegment(sketch, "E410", {"start": v(-11.25, -29.72) * mm, "end": v(-11.25, -32.82) * mm});
            skLineSegment(sketch, "E411", {"start": v(-11.25, -32.82) * mm, "end": v(-12.05, -32.82) * mm});
            skLineSegment(sketch, "E412", {"start": v(-12.05, -32.82) * mm, "end": v(-12.05, -38.62) * mm});
            skLineSegment(sketch, "E413", {"start": v(-12.05, -38.62) * mm, "end": v(-11.25, -38.62) * mm});
            skLineSegment(sketch, "E414", {"start": v(-11.25, -38.62) * mm, "end": v(-11.25, -41.72) * mm});
            skLineSegment(sketch, "E415", {"start": v(-11.25, -41.72) * mm, "end": v(-12.05, -41.72) * mm});
            skLineSegment(sketch, "E416", {"start": v(7, 29.72) * mm, "end": v(7, 28.72) * mm});
            skLineSegment(sketch, "E417", {"start": v(7, 28.72) * mm, "end": v(-7, 28.72) * mm});
            skLineSegment(sketch, "E418", {"start": v(-7, 28.72) * mm, "end": v(-7, 29.72) * mm});
            skLineSegment(sketch, "E419", {"start": v(-7, 29.72) * mm, "end": v(-7.8, 29.72) * mm});
            skLineSegment(sketch, "E420", {"start": v(-7.8, 29.72) * mm, "end": v(-7.8, 32.82) * mm});
            skLineSegment(sketch, "E421", {"start": v(-7.8, 32.82) * mm, "end": v(-7, 32.82) * mm});
            skLineSegment(sketch, "E422", {"start": v(-7, 32.82) * mm, "end": v(-7, 38.62) * mm});
            skLineSegment(sketch, "E423", {"start": v(-7, 38.62) * mm, "end": v(-7.8, 38.62) * mm});
            skLineSegment(sketch, "E424", {"start": v(-7.8, 38.62) * mm, "end": v(-7.8, 41.72) * mm});
            skLineSegment(sketch, "E425", {"start": v(-7.8, 41.72) * mm, "end": v(-7, 41.72) * mm});
            skLineSegment(sketch, "E426", {"start": v(-7, 41.72) * mm, "end": v(-7, 42.72) * mm});
            skLineSegment(sketch, "E427", {"start": v(-7, 42.72) * mm, "end": v(7, 42.72) * mm});
            skLineSegment(sketch, "E428", {"start": v(7, 42.72) * mm, "end": v(7, 41.72) * mm});
            skLineSegment(sketch, "E429", {"start": v(7, 41.72) * mm, "end": v(7.8, 41.72) * mm});
            skLineSegment(sketch, "E430", {"start": v(7.8, 41.72) * mm, "end": v(7.8, 38.62) * mm});
            skLineSegment(sketch, "E431", {"start": v(7.8, 38.62) * mm, "end": v(7, 38.62) * mm});
            skLineSegment(sketch, "E432", {"start": v(7, 38.62) * mm, "end": v(7, 32.82) * mm});
            skLineSegment(sketch, "E433", {"start": v(7, 32.82) * mm, "end": v(7.8, 32.82) * mm});
            skLineSegment(sketch, "E434", {"start": v(7.8, 32.82) * mm, "end": v(7.8, 29.72) * mm});
            skLineSegment(sketch, "E435", {"start": v(7.8, 29.72) * mm, "end": v(7, 29.72) * mm});
            skLineSegment(sketch, "E436", {"start": v(7, 10.67) * mm, "end": v(7, 9.67) * mm});
            skLineSegment(sketch, "E437", {"start": v(7, 9.67) * mm, "end": v(-7, 9.67) * mm});
            skLineSegment(sketch, "E438", {"start": v(-7, 9.67) * mm, "end": v(-7, 10.67) * mm});
            skLineSegment(sketch, "E439", {"start": v(-7, 10.67) * mm, "end": v(-7.8, 10.67) * mm});
            skLineSegment(sketch, "E440", {"start": v(-7.8, 10.67) * mm, "end": v(-7.8, 13.77) * mm});
            skLineSegment(sketch, "E441", {"start": v(-7.8, 13.77) * mm, "end": v(-7, 13.77) * mm});
            skLineSegment(sketch, "E442", {"start": v(-7, 13.77) * mm, "end": v(-7, 19.57) * mm});
            skLineSegment(sketch, "E443", {"start": v(-7, 19.57) * mm, "end": v(-7.8, 19.57) * mm});
            skLineSegment(sketch, "E444", {"start": v(-7.8, 19.57) * mm, "end": v(-7.8, 22.67) * mm});
            skLineSegment(sketch, "E445", {"start": v(-7.8, 22.67) * mm, "end": v(-7, 22.67) * mm});
            skLineSegment(sketch, "E446", {"start": v(-7, 22.67) * mm, "end": v(-7, 23.67) * mm});
            skLineSegment(sketch, "E447", {"start": v(-7, 23.67) * mm, "end": v(7, 23.67) * mm});
            skLineSegment(sketch, "E448", {"start": v(7, 23.67) * mm, "end": v(7, 22.67) * mm});
            skLineSegment(sketch, "E449", {"start": v(7, 22.67) * mm, "end": v(7.8, 22.67) * mm});
            skLineSegment(sketch, "E450", {"start": v(7.8, 22.67) * mm, "end": v(7.8, 19.57) * mm});
            skLineSegment(sketch, "E451", {"start": v(7.8, 19.57) * mm, "end": v(7, 19.57) * mm});
            skLineSegment(sketch, "E452", {"start": v(7, 19.57) * mm, "end": v(7, 13.77) * mm});
            skLineSegment(sketch, "E453", {"start": v(7, 13.77) * mm, "end": v(7.8, 13.77) * mm});
            skLineSegment(sketch, "E454", {"start": v(7.8, 13.77) * mm, "end": v(7.8, 10.67) * mm});
            skLineSegment(sketch, "E455", {"start": v(7.8, 10.67) * mm, "end": v(7, 10.67) * mm});
            skLineSegment(sketch, "E456", {"start": v(7, -8.38) * mm, "end": v(7, -9.38) * mm});
            skLineSegment(sketch, "E457", {"start": v(7, -9.38) * mm, "end": v(-7, -9.38) * mm});
            skLineSegment(sketch, "E458", {"start": v(-7, -9.38) * mm, "end": v(-7, -8.38) * mm});
            skLineSegment(sketch, "E459", {"start": v(-7, -8.38) * mm, "end": v(-7.8, -8.38) * mm});
            skLineSegment(sketch, "E460", {"start": v(-7.8, -8.38) * mm, "end": v(-7.8, -5.28) * mm});
            skLineSegment(sketch, "E461", {"start": v(-7.8, -5.28) * mm, "end": v(-7, -5.28) * mm});
            skLineSegment(sketch, "E462", {"start": v(-7, -5.28) * mm, "end": v(-7, 0.52) * mm});
            skLineSegment(sketch, "E463", {"start": v(-7, 0.52) * mm, "end": v(-7.8, 0.52) * mm});
            skLineSegment(sketch, "E464", {"start": v(-7.8, 0.52) * mm, "end": v(-7.8, 3.62) * mm});
            skLineSegment(sketch, "E465", {"start": v(-7.8, 3.62) * mm, "end": v(-7, 3.62) * mm});
            skLineSegment(sketch, "E466", {"start": v(-7, 3.62) * mm, "end": v(-7, 4.62) * mm});
            skLineSegment(sketch, "E467", {"start": v(-7, 4.62) * mm, "end": v(7, 4.62) * mm});
            skLineSegment(sketch, "E468", {"start": v(7, 4.62) * mm, "end": v(7, 3.62) * mm});
            skLineSegment(sketch, "E469", {"start": v(7, 3.62) * mm, "end": v(7.8, 3.62) * mm});
            skLineSegment(sketch, "E470", {"start": v(7.8, 3.62) * mm, "end": v(7.8, 0.52) * mm});
            skLineSegment(sketch, "E471", {"start": v(7.8, 0.52) * mm, "end": v(7, 0.52) * mm});
            skLineSegment(sketch, "E472", {"start": v(7, 0.52) * mm, "end": v(7, -5.28) * mm});
            skLineSegment(sketch, "E473", {"start": v(7, -5.28) * mm, "end": v(7.8, -5.28) * mm});
            skLineSegment(sketch, "E474", {"start": v(7.8, -5.28) * mm, "end": v(7.8, -8.38) * mm});
            skLineSegment(sketch, "E475", {"start": v(7.8, -8.38) * mm, "end": v(7, -8.38) * mm});
            skLineSegment(sketch, "E476", {"start": v(7, -27.43) * mm, "end": v(7, -28.43) * mm});
            skLineSegment(sketch, "E477", {"start": v(7, -28.43) * mm, "end": v(-7, -28.43) * mm});
            skLineSegment(sketch, "E478", {"start": v(-7, -28.43) * mm, "end": v(-7, -27.43) * mm});
            skLineSegment(sketch, "E479", {"start": v(-7, -27.43) * mm, "end": v(-7.8, -27.43) * mm});
            skLineSegment(sketch, "E480", {"start": v(-7.8, -27.43) * mm, "end": v(-7.8, -24.33) * mm});
            skLineSegment(sketch, "E481", {"start": v(-7.8, -24.33) * mm, "end": v(-7, -24.33) * mm});
            skLineSegment(sketch, "E482", {"start": v(-7, -24.33) * mm, "end": v(-7, -18.53) * mm});
            skLineSegment(sketch, "E483", {"start": v(-7, -18.53) * mm, "end": v(-7.8, -18.53) * mm});
            skLineSegment(sketch, "E484", {"start": v(-7.8, -18.53) * mm, "end": v(-7.8, -15.43) * mm});
            skLineSegment(sketch, "E485", {"start": v(-7.8, -15.43) * mm, "end": v(-7, -15.43) * mm});
            skLineSegment(sketch, "E486", {"start": v(-7, -15.43) * mm, "end": v(-7, -14.43) * mm});
            skLineSegment(sketch, "E487", {"start": v(-7, -14.43) * mm, "end": v(7, -14.43) * mm});
            skLineSegment(sketch, "E488", {"start": v(7, -14.43) * mm, "end": v(7, -15.43) * mm});
            skLineSegment(sketch, "E489", {"start": v(7, -15.43) * mm, "end": v(7.8, -15.43) * mm});
            skLineSegment(sketch, "E490", {"start": v(7.8, -15.43) * mm, "end": v(7.8, -18.53) * mm});
            skLineSegment(sketch, "E491", {"start": v(7.8, -18.53) * mm, "end": v(7, -18.53) * mm});
            skLineSegment(sketch, "E492", {"start": v(7, -18.53) * mm, "end": v(7, -24.33) * mm});
            skLineSegment(sketch, "E493", {"start": v(7, -24.33) * mm, "end": v(7.8, -24.33) * mm});
            skLineSegment(sketch, "E494", {"start": v(7.8, -24.33) * mm, "end": v(7.8, -27.43) * mm});
            skLineSegment(sketch, "E495", {"start": v(7.8, -27.43) * mm, "end": v(7, -27.43) * mm});
            skLineSegment(sketch, "E496", {"start": v(7, -46.48) * mm, "end": v(7, -47.48) * mm});
            skLineSegment(sketch, "E497", {"start": v(7, -47.48) * mm, "end": v(-7, -47.48) * mm});
            skLineSegment(sketch, "E498", {"start": v(-7, -47.48) * mm, "end": v(-7, -46.48) * mm});
            skLineSegment(sketch, "E499", {"start": v(-7, -46.48) * mm, "end": v(-7.8, -46.48) * mm});
            skLineSegment(sketch, "E500", {"start": v(-7.8, -46.48) * mm, "end": v(-7.8, -43.38) * mm});
            skLineSegment(sketch, "E501", {"start": v(-7.8, -43.38) * mm, "end": v(-7, -43.38) * mm});
            skLineSegment(sketch, "E502", {"start": v(-7, -43.38) * mm, "end": v(-7, -37.58) * mm});
            skLineSegment(sketch, "E503", {"start": v(-7, -37.58) * mm, "end": v(-7.8, -37.58) * mm});
            skLineSegment(sketch, "E504", {"start": v(-7.8, -37.58) * mm, "end": v(-7.8, -34.48) * mm});
            skLineSegment(sketch, "E505", {"start": v(-7.8, -34.48) * mm, "end": v(-7, -34.48) * mm});
            skLineSegment(sketch, "E506", {"start": v(-7, -34.48) * mm, "end": v(-7, -33.48) * mm});
            skLineSegment(sketch, "E507", {"start": v(-7, -33.48) * mm, "end": v(7, -33.48) * mm});
            skLineSegment(sketch, "E508", {"start": v(7, -33.48) * mm, "end": v(7, -34.48) * mm});
            skLineSegment(sketch, "E509", {"start": v(7, -34.48) * mm, "end": v(7.8, -34.48) * mm});
            skLineSegment(sketch, "E510", {"start": v(7.8, -34.48) * mm, "end": v(7.8, -37.58) * mm});
            skLineSegment(sketch, "E511", {"start": v(7.8, -37.58) * mm, "end": v(7, -37.58) * mm});
            skLineSegment(sketch, "E512", {"start": v(7, -37.58) * mm, "end": v(7, -43.38) * mm});
            skLineSegment(sketch, "E513", {"start": v(7, -43.38) * mm, "end": v(7.8, -43.38) * mm});
            skLineSegment(sketch, "E514", {"start": v(7.8, -43.38) * mm, "end": v(7.8, -46.48) * mm});
            skLineSegment(sketch, "E515", {"start": v(7.8, -46.48) * mm, "end": v(7, -46.48) * mm});
            skLineSegment(sketch, "E516", {"start": v(26.05, 24.96) * mm, "end": v(26.05, 23.96) * mm});
            skLineSegment(sketch, "E517", {"start": v(26.05, 23.96) * mm, "end": v(12.05, 23.96) * mm});
            skLineSegment(sketch, "E518", {"start": v(12.05, 23.96) * mm, "end": v(12.05, 24.96) * mm});
            skLineSegment(sketch, "E519", {"start": v(12.05, 24.96) * mm, "end": v(11.25, 24.96) * mm});
            skLineSegment(sketch, "E520", {"start": v(11.25, 24.96) * mm, "end": v(11.25, 28.06) * mm});
            skLineSegment(sketch, "E521", {"start": v(11.25, 28.06) * mm, "end": v(12.05, 28.06) * mm});
            skLineSegment(sketch, "E522", {"start": v(12.05, 28.06) * mm, "end": v(12.05, 33.86) * mm});
            skLineSegment(sketch, "E523", {"start": v(12.05, 33.86) * mm, "end": v(11.25, 33.86) * mm});
            skLineSegment(sketch, "E524", {"start": v(11.25, 33.86) * mm, "end": v(11.25, 36.96) * mm});
            skLineSegment(sketch, "E525", {"start": v(11.25, 36.96) * mm, "end": v(12.05, 36.96) * mm});
            skLineSegment(sketch, "E526", {"start": v(12.05, 36.96) * mm, "end": v(12.05, 37.96) * mm});
            skLineSegment(sketch, "E527", {"start": v(12.05, 37.96) * mm, "end": v(26.05, 37.96) * mm});
            skLineSegment(sketch, "E528", {"start": v(26.05, 37.96) * mm, "end": v(26.05, 36.96) * mm});
            skLineSegment(sketch, "E529", {"start": v(26.05, 36.96) * mm, "end": v(26.85, 36.96) * mm});
            skLineSegment(sketch, "E530", {"start": v(26.85, 36.96) * mm, "end": v(26.85, 33.86) * mm});
            skLineSegment(sketch, "E531", {"start": v(26.85, 33.86) * mm, "end": v(26.05, 33.86) * mm});
            skLineSegment(sketch, "E532", {"start": v(26.05, 33.86) * mm, "end": v(26.05, 28.06) * mm});
            skLineSegment(sketch, "E533", {"start": v(26.05, 28.06) * mm, "end": v(26.85, 28.06) * mm});
            skLineSegment(sketch, "E534", {"start": v(26.85, 28.06) * mm, "end": v(26.85, 24.96) * mm});
            skLineSegment(sketch, "E535", {"start": v(26.85, 24.96) * mm, "end": v(26.05, 24.96) * mm});
            skLineSegment(sketch, "E536", {"start": v(26.05, 5.9) * mm, "end": v(26.05, 4.9) * mm});
            skLineSegment(sketch, "E537", {"start": v(26.05, 4.9) * mm, "end": v(12.05, 4.9) * mm});
            skLineSegment(sketch, "E538", {"start": v(12.05, 4.9) * mm, "end": v(12.05, 5.9) * mm});
            skLineSegment(sketch, "E539", {"start": v(12.05, 5.9) * mm, "end": v(11.25, 5.9) * mm});
            skLineSegment(sketch, "E540", {"start": v(11.25, 5.9) * mm, "end": v(11.25, 9) * mm});
            skLineSegment(sketch, "E541", {"start": v(11.25, 9) * mm, "end": v(12.05, 9) * mm});
            skLineSegment(sketch, "E542", {"start": v(12.05, 9) * mm, "end": v(12.05, 14.8) * mm});
            skLineSegment(sketch, "E543", {"start": v(12.05, 14.8) * mm, "end": v(11.25, 14.8) * mm});
            skLineSegment(sketch, "E544", {"start": v(11.25, 14.8) * mm, "end": v(11.25, 17.9) * mm});
            skLineSegment(sketch, "E545", {"start": v(11.25, 17.9) * mm, "end": v(12.05, 17.9) * mm});
            skLineSegment(sketch, "E546", {"start": v(12.05, 17.9) * mm, "end": v(12.05, 18.9) * mm});
            skLineSegment(sketch, "E547", {"start": v(12.05, 18.9) * mm, "end": v(26.05, 18.9) * mm});
            skLineSegment(sketch, "E548", {"start": v(26.05, 18.9) * mm, "end": v(26.05, 17.9) * mm});
            skLineSegment(sketch, "E549", {"start": v(26.05, 17.9) * mm, "end": v(26.85, 17.9) * mm});
            skLineSegment(sketch, "E550", {"start": v(26.85, 17.9) * mm, "end": v(26.85, 14.8) * mm});
            skLineSegment(sketch, "E551", {"start": v(26.85, 14.8) * mm, "end": v(26.05, 14.8) * mm});
            skLineSegment(sketch, "E552", {"start": v(26.05, 14.8) * mm, "end": v(26.05, 9) * mm});
            skLineSegment(sketch, "E553", {"start": v(26.05, 9) * mm, "end": v(26.85, 9) * mm});
            skLineSegment(sketch, "E554", {"start": v(26.85, 9) * mm, "end": v(26.85, 5.9) * mm});
            skLineSegment(sketch, "E555", {"start": v(26.85, 5.9) * mm, "end": v(26.05, 5.9) * mm});
            skLineSegment(sketch, "E556", {"start": v(26.05, -13.14) * mm, "end": v(26.05, -14.14) * mm});
            skLineSegment(sketch, "E557", {"start": v(26.05, -14.14) * mm, "end": v(12.05, -14.14) * mm});
            skLineSegment(sketch, "E558", {"start": v(12.05, -14.14) * mm, "end": v(12.05, -13.14) * mm});
            skLineSegment(sketch, "E559", {"start": v(12.05, -13.14) * mm, "end": v(11.25, -13.14) * mm});
            skLineSegment(sketch, "E560", {"start": v(11.25, -13.14) * mm, "end": v(11.25, -10.04) * mm});
            skLineSegment(sketch, "E561", {"start": v(11.25, -10.04) * mm, "end": v(12.05, -10.04) * mm});
            skLineSegment(sketch, "E562", {"start": v(12.05, -10.04) * mm, "end": v(12.05, -4.24) * mm});
            skLineSegment(sketch, "E563", {"start": v(12.05, -4.24) * mm, "end": v(11.25, -4.24) * mm});
            skLineSegment(sketch, "E564", {"start": v(11.25, -4.24) * mm, "end": v(11.25, -1.14) * mm});
            skLineSegment(sketch, "E565", {"start": v(11.25, -1.14) * mm, "end": v(12.05, -1.14) * mm});
            skLineSegment(sketch, "E566", {"start": v(12.05, -1.14) * mm, "end": v(12.05, -0.14) * mm});
            skLineSegment(sketch, "E567", {"start": v(12.05, -0.14) * mm, "end": v(26.05, -0.14) * mm});
            skLineSegment(sketch, "E568", {"start": v(26.05, -0.14) * mm, "end": v(26.05, -1.14) * mm});
            skLineSegment(sketch, "E569", {"start": v(26.05, -1.14) * mm, "end": v(26.85, -1.14) * mm});
            skLineSegment(sketch, "E570", {"start": v(26.85, -1.14) * mm, "end": v(26.85, -4.24) * mm});
            skLineSegment(sketch, "E571", {"start": v(26.85, -4.24) * mm, "end": v(26.05, -4.24) * mm});
            skLineSegment(sketch, "E572", {"start": v(26.05, -4.24) * mm, "end": v(26.05, -10.04) * mm});
            skLineSegment(sketch, "E573", {"start": v(26.05, -10.04) * mm, "end": v(26.85, -10.04) * mm});
            skLineSegment(sketch, "E574", {"start": v(26.85, -10.04) * mm, "end": v(26.85, -13.14) * mm});
            skLineSegment(sketch, "E575", {"start": v(26.85, -13.14) * mm, "end": v(26.05, -13.14) * mm});
            skLineSegment(sketch, "E576", {"start": v(26.05, -32.2) * mm, "end": v(26.05, -33.2) * mm});
            skLineSegment(sketch, "E577", {"start": v(26.05, -33.2) * mm, "end": v(12.05, -33.2) * mm});
            skLineSegment(sketch, "E578", {"start": v(12.05, -33.2) * mm, "end": v(12.05, -32.2) * mm});
            skLineSegment(sketch, "E579", {"start": v(12.05, -32.2) * mm, "end": v(11.25, -32.2) * mm});
            skLineSegment(sketch, "E580", {"start": v(11.25, -32.2) * mm, "end": v(11.25, -29.1) * mm});
            skLineSegment(sketch, "E581", {"start": v(11.25, -29.1) * mm, "end": v(12.05, -29.1) * mm});
            skLineSegment(sketch, "E582", {"start": v(12.05, -29.1) * mm, "end": v(12.05, -23.3) * mm});
            skLineSegment(sketch, "E583", {"start": v(12.05, -23.3) * mm, "end": v(11.25, -23.3) * mm});
            skLineSegment(sketch, "E584", {"start": v(11.25, -23.3) * mm, "end": v(11.25, -20.2) * mm});
            skLineSegment(sketch, "E585", {"start": v(11.25, -20.2) * mm, "end": v(12.05, -20.2) * mm});
            skLineSegment(sketch, "E586", {"start": v(12.05, -20.2) * mm, "end": v(12.05, -19.2) * mm});
            skLineSegment(sketch, "E587", {"start": v(12.05, -19.2) * mm, "end": v(26.05, -19.2) * mm});
            skLineSegment(sketch, "E588", {"start": v(26.05, -19.2) * mm, "end": v(26.05, -20.2) * mm});
            skLineSegment(sketch, "E589", {"start": v(26.05, -20.2) * mm, "end": v(26.85, -20.2) * mm});
            skLineSegment(sketch, "E590", {"start": v(26.85, -20.2) * mm, "end": v(26.85, -23.3) * mm});
            skLineSegment(sketch, "E591", {"start": v(26.85, -23.3) * mm, "end": v(26.05, -23.3) * mm});
            skLineSegment(sketch, "E592", {"start": v(26.05, -23.3) * mm, "end": v(26.05, -29.1) * mm});
            skLineSegment(sketch, "E593", {"start": v(26.05, -29.1) * mm, "end": v(26.85, -29.1) * mm});
            skLineSegment(sketch, "E594", {"start": v(26.85, -29.1) * mm, "end": v(26.85, -32.2) * mm});
            skLineSegment(sketch, "E595", {"start": v(26.85, -32.2) * mm, "end": v(26.05, -32.2) * mm});
            skLineSegment(sketch, "E596", {"start": v(26.05, -51.24) * mm, "end": v(26.05, -52.24) * mm});
            skLineSegment(sketch, "E597", {"start": v(26.05, -52.24) * mm, "end": v(12.05, -52.24) * mm});
            skLineSegment(sketch, "E598", {"start": v(12.05, -52.24) * mm, "end": v(12.05, -51.24) * mm});
            skLineSegment(sketch, "E599", {"start": v(12.05, -51.24) * mm, "end": v(11.25, -51.24) * mm});
            skLineSegment(sketch, "E600", {"start": v(11.25, -51.24) * mm, "end": v(11.25, -48.14) * mm});
            skLineSegment(sketch, "E601", {"start": v(11.25, -48.14) * mm, "end": v(12.05, -48.14) * mm});
            skLineSegment(sketch, "E602", {"start": v(12.05, -48.14) * mm, "end": v(12.05, -42.34) * mm});
            skLineSegment(sketch, "E603", {"start": v(12.05, -42.34) * mm, "end": v(11.25, -42.34) * mm});
            skLineSegment(sketch, "E604", {"start": v(11.25, -42.34) * mm, "end": v(11.25, -39.24) * mm});
            skLineSegment(sketch, "E605", {"start": v(11.25, -39.24) * mm, "end": v(12.05, -39.24) * mm});
            skLineSegment(sketch, "E606", {"start": v(12.05, -39.24) * mm, "end": v(12.05, -38.24) * mm});
            skLineSegment(sketch, "E607", {"start": v(12.05, -38.24) * mm, "end": v(26.05, -38.24) * mm});
            skLineSegment(sketch, "E608", {"start": v(26.05, -38.24) * mm, "end": v(26.05, -39.24) * mm});
            skLineSegment(sketch, "E609", {"start": v(26.05, -39.24) * mm, "end": v(26.85, -39.24) * mm});
            skLineSegment(sketch, "E610", {"start": v(26.85, -39.24) * mm, "end": v(26.85, -42.34) * mm});
            skLineSegment(sketch, "E611", {"start": v(26.85, -42.34) * mm, "end": v(26.05, -42.34) * mm});
            skLineSegment(sketch, "E612", {"start": v(26.05, -42.34) * mm, "end": v(26.05, -48.14) * mm});
            skLineSegment(sketch, "E613", {"start": v(26.05, -48.14) * mm, "end": v(26.85, -48.14) * mm});
            skLineSegment(sketch, "E614", {"start": v(26.85, -48.14) * mm, "end": v(26.85, -51.24) * mm});
            skLineSegment(sketch, "E615", {"start": v(26.85, -51.24) * mm, "end": v(26.05, -51.24) * mm});
            skLineSegment(sketch, "E616", {"start": v(45.1, 24.96) * mm, "end": v(45.1, 23.96) * mm});
            skLineSegment(sketch, "E617", {"start": v(45.1, 23.96) * mm, "end": v(31.1, 23.96) * mm});
            skLineSegment(sketch, "E618", {"start": v(31.1, 23.96) * mm, "end": v(31.1, 24.96) * mm});
            skLineSegment(sketch, "E619", {"start": v(31.1, 24.96) * mm, "end": v(30.3, 24.96) * mm});
            skLineSegment(sketch, "E620", {"start": v(30.3, 24.96) * mm, "end": v(30.3, 28.06) * mm});
            skLineSegment(sketch, "E621", {"start": v(30.3, 28.06) * mm, "end": v(31.1, 28.06) * mm});
            skLineSegment(sketch, "E622", {"start": v(31.1, 28.06) * mm, "end": v(31.1, 33.86) * mm});
            skLineSegment(sketch, "E623", {"start": v(31.1, 33.86) * mm, "end": v(30.3, 33.86) * mm});
            skLineSegment(sketch, "E624", {"start": v(30.3, 33.86) * mm, "end": v(30.3, 36.96) * mm});
            skLineSegment(sketch, "E625", {"start": v(30.3, 36.96) * mm, "end": v(31.1, 36.96) * mm});
            skLineSegment(sketch, "E626", {"start": v(31.1, 36.96) * mm, "end": v(31.1, 37.96) * mm});
            skLineSegment(sketch, "E627", {"start": v(31.1, 37.96) * mm, "end": v(45.1, 37.96) * mm});
            skLineSegment(sketch, "E628", {"start": v(45.1, 37.96) * mm, "end": v(45.1, 36.96) * mm});
            skLineSegment(sketch, "E629", {"start": v(45.1, 36.96) * mm, "end": v(45.9, 36.96) * mm});
            skLineSegment(sketch, "E630", {"start": v(45.9, 36.96) * mm, "end": v(45.9, 33.86) * mm});
            skLineSegment(sketch, "E631", {"start": v(45.9, 33.86) * mm, "end": v(45.1, 33.86) * mm});
            skLineSegment(sketch, "E632", {"start": v(45.1, 33.86) * mm, "end": v(45.1, 28.06) * mm});
            skLineSegment(sketch, "E633", {"start": v(45.1, 28.06) * mm, "end": v(45.9, 28.06) * mm});
            skLineSegment(sketch, "E634", {"start": v(45.9, 28.06) * mm, "end": v(45.9, 24.96) * mm});
            skLineSegment(sketch, "E635", {"start": v(45.9, 24.96) * mm, "end": v(45.1, 24.96) * mm});
            skLineSegment(sketch, "E636", {"start": v(45.1, 5.9) * mm, "end": v(45.1, 4.9) * mm});
            skLineSegment(sketch, "E637", {"start": v(45.1, 4.9) * mm, "end": v(31.1, 4.9) * mm});
            skLineSegment(sketch, "E638", {"start": v(31.1, 4.9) * mm, "end": v(31.1, 5.9) * mm});
            skLineSegment(sketch, "E639", {"start": v(31.1, 5.9) * mm, "end": v(30.3, 5.9) * mm});
            skLineSegment(sketch, "E640", {"start": v(30.3, 5.9) * mm, "end": v(30.3, 9) * mm});
            skLineSegment(sketch, "E641", {"start": v(30.3, 9) * mm, "end": v(31.1, 9) * mm});
            skLineSegment(sketch, "E642", {"start": v(31.1, 9) * mm, "end": v(31.1, 14.8) * mm});
            skLineSegment(sketch, "E643", {"start": v(31.1, 14.8) * mm, "end": v(30.3, 14.8) * mm});
            skLineSegment(sketch, "E644", {"start": v(30.3, 14.8) * mm, "end": v(30.3, 17.9) * mm});
            skLineSegment(sketch, "E645", {"start": v(30.3, 17.9) * mm, "end": v(31.1, 17.9) * mm});
            skLineSegment(sketch, "E646", {"start": v(31.1, 17.9) * mm, "end": v(31.1, 18.9) * mm});
            skLineSegment(sketch, "E647", {"start": v(31.1, 18.9) * mm, "end": v(45.1, 18.9) * mm});
            skLineSegment(sketch, "E648", {"start": v(45.1, 18.9) * mm, "end": v(45.1, 17.9) * mm});
            skLineSegment(sketch, "E649", {"start": v(45.1, 17.9) * mm, "end": v(45.9, 17.9) * mm});
            skLineSegment(sketch, "E650", {"start": v(45.9, 17.9) * mm, "end": v(45.9, 14.8) * mm});
            skLineSegment(sketch, "E651", {"start": v(45.9, 14.8) * mm, "end": v(45.1, 14.8) * mm});
            skLineSegment(sketch, "E652", {"start": v(45.1, 14.8) * mm, "end": v(45.1, 9) * mm});
            skLineSegment(sketch, "E653", {"start": v(45.1, 9) * mm, "end": v(45.9, 9) * mm});
            skLineSegment(sketch, "E654", {"start": v(45.9, 9) * mm, "end": v(45.9, 5.9) * mm});
            skLineSegment(sketch, "E655", {"start": v(45.9, 5.9) * mm, "end": v(45.1, 5.9) * mm});
            skLineSegment(sketch, "E656", {"start": v(45.1, -13.14) * mm, "end": v(45.1, -14.14) * mm});
            skLineSegment(sketch, "E657", {"start": v(45.1, -14.14) * mm, "end": v(31.1, -14.14) * mm});
            skLineSegment(sketch, "E658", {"start": v(31.1, -14.14) * mm, "end": v(31.1, -13.14) * mm});
            skLineSegment(sketch, "E659", {"start": v(31.1, -13.14) * mm, "end": v(30.3, -13.14) * mm});
            skLineSegment(sketch, "E660", {"start": v(30.3, -13.14) * mm, "end": v(30.3, -10.04) * mm});
            skLineSegment(sketch, "E661", {"start": v(30.3, -10.04) * mm, "end": v(31.1, -10.04) * mm});
            skLineSegment(sketch, "E662", {"start": v(31.1, -10.04) * mm, "end": v(31.1, -4.24) * mm});
            skLineSegment(sketch, "E663", {"start": v(31.1, -4.24) * mm, "end": v(30.3, -4.24) * mm});
            skLineSegment(sketch, "E664", {"start": v(30.3, -4.24) * mm, "end": v(30.3, -1.14) * mm});
            skLineSegment(sketch, "E665", {"start": v(30.3, -1.14) * mm, "end": v(31.1, -1.14) * mm});
            skLineSegment(sketch, "E666", {"start": v(31.1, -1.14) * mm, "end": v(31.1, -0.14) * mm});
            skLineSegment(sketch, "E667", {"start": v(31.1, -0.14) * mm, "end": v(45.1, -0.14) * mm});
            skLineSegment(sketch, "E668", {"start": v(45.1, -0.14) * mm, "end": v(45.1, -1.14) * mm});
            skLineSegment(sketch, "E669", {"start": v(45.1, -1.14) * mm, "end": v(45.9, -1.14) * mm});
            skLineSegment(sketch, "E670", {"start": v(45.9, -1.14) * mm, "end": v(45.9, -4.24) * mm});
            skLineSegment(sketch, "E671", {"start": v(45.9, -4.24) * mm, "end": v(45.1, -4.24) * mm});
            skLineSegment(sketch, "E672", {"start": v(45.1, -4.24) * mm, "end": v(45.1, -10.04) * mm});
            skLineSegment(sketch, "E673", {"start": v(45.1, -10.04) * mm, "end": v(45.9, -10.04) * mm});
            skLineSegment(sketch, "E674", {"start": v(45.9, -10.04) * mm, "end": v(45.9, -13.14) * mm});
            skLineSegment(sketch, "E675", {"start": v(45.9, -13.14) * mm, "end": v(45.1, -13.14) * mm});
            skLineSegment(sketch, "E676", {"start": v(45.1, -32.2) * mm, "end": v(45.1, -33.2) * mm});
            skLineSegment(sketch, "E677", {"start": v(45.1, -33.2) * mm, "end": v(31.1, -33.2) * mm});
            skLineSegment(sketch, "E678", {"start": v(31.1, -33.2) * mm, "end": v(31.1, -32.2) * mm});
            skLineSegment(sketch, "E679", {"start": v(31.1, -32.2) * mm, "end": v(30.3, -32.2) * mm});
            skLineSegment(sketch, "E680", {"start": v(30.3, -32.2) * mm, "end": v(30.3, -29.1) * mm});
            skLineSegment(sketch, "E681", {"start": v(30.3, -29.1) * mm, "end": v(31.1, -29.1) * mm});
            skLineSegment(sketch, "E682", {"start": v(31.1, -29.1) * mm, "end": v(31.1, -23.3) * mm});
            skLineSegment(sketch, "E683", {"start": v(31.1, -23.3) * mm, "end": v(30.3, -23.3) * mm});
            skLineSegment(sketch, "E684", {"start": v(30.3, -23.3) * mm, "end": v(30.3, -20.2) * mm});
            skLineSegment(sketch, "E685", {"start": v(30.3, -20.2) * mm, "end": v(31.1, -20.2) * mm});
            skLineSegment(sketch, "E686", {"start": v(31.1, -20.2) * mm, "end": v(31.1, -19.2) * mm});
            skLineSegment(sketch, "E687", {"start": v(31.1, -19.2) * mm, "end": v(45.1, -19.2) * mm});
            skLineSegment(sketch, "E688", {"start": v(45.1, -19.2) * mm, "end": v(45.1, -20.2) * mm});
            skLineSegment(sketch, "E689", {"start": v(45.1, -20.2) * mm, "end": v(45.9, -20.2) * mm});
            skLineSegment(sketch, "E690", {"start": v(45.9, -20.2) * mm, "end": v(45.9, -23.3) * mm});
            skLineSegment(sketch, "E691", {"start": v(45.9, -23.3) * mm, "end": v(45.1, -23.3) * mm});
            skLineSegment(sketch, "E692", {"start": v(45.1, -23.3) * mm, "end": v(45.1, -29.1) * mm});
            skLineSegment(sketch, "E693", {"start": v(45.1, -29.1) * mm, "end": v(45.9, -29.1) * mm});
            skLineSegment(sketch, "E694", {"start": v(45.9, -29.1) * mm, "end": v(45.9, -32.2) * mm});
            skLineSegment(sketch, "E695", {"start": v(45.9, -32.2) * mm, "end": v(45.1, -32.2) * mm});
            skLineSegment(sketch, "E696", {"start": v(45.1, -51.24) * mm, "end": v(45.1, -52.24) * mm});
            skLineSegment(sketch, "E697", {"start": v(45.1, -52.24) * mm, "end": v(31.1, -52.24) * mm});
            skLineSegment(sketch, "E698", {"start": v(31.1, -52.24) * mm, "end": v(31.1, -51.24) * mm});
            skLineSegment(sketch, "E699", {"start": v(31.1, -51.24) * mm, "end": v(30.3, -51.24) * mm});
            skLineSegment(sketch, "E700", {"start": v(30.3, -51.24) * mm, "end": v(30.3, -48.14) * mm});
            skLineSegment(sketch, "E701", {"start": v(30.3, -48.14) * mm, "end": v(31.1, -48.14) * mm});
            skLineSegment(sketch, "E702", {"start": v(31.1, -48.14) * mm, "end": v(31.1, -42.34) * mm});
            skLineSegment(sketch, "E703", {"start": v(31.1, -42.34) * mm, "end": v(30.3, -42.34) * mm});
            skLineSegment(sketch, "E704", {"start": v(30.3, -42.34) * mm, "end": v(30.3, -39.24) * mm});
            skLineSegment(sketch, "E705", {"start": v(30.3, -39.24) * mm, "end": v(31.1, -39.24) * mm});
            skLineSegment(sketch, "E706", {"start": v(31.1, -39.24) * mm, "end": v(31.1, -38.24) * mm});
            skLineSegment(sketch, "E707", {"start": v(31.1, -38.24) * mm, "end": v(45.1, -38.24) * mm});
            skLineSegment(sketch, "E708", {"start": v(45.1, -38.24) * mm, "end": v(45.1, -39.24) * mm});
            skLineSegment(sketch, "E709", {"start": v(45.1, -39.24) * mm, "end": v(45.9, -39.24) * mm});
            skLineSegment(sketch, "E710", {"start": v(45.9, -39.24) * mm, "end": v(45.9, -42.34) * mm});
            skLineSegment(sketch, "E711", {"start": v(45.9, -42.34) * mm, "end": v(45.1, -42.34) * mm});
            skLineSegment(sketch, "E712", {"start": v(45.1, -42.34) * mm, "end": v(45.1, -48.14) * mm});
            skLineSegment(sketch, "E713", {"start": v(45.1, -48.14) * mm, "end": v(45.9, -48.14) * mm});
            skLineSegment(sketch, "E714", {"start": v(45.9, -48.14) * mm, "end": v(45.9, -51.24) * mm});
            skLineSegment(sketch, "E715", {"start": v(45.9, -51.24) * mm, "end": v(45.1, -51.24) * mm});
            skLineSegment(sketch, "E716", {"start": v(64.15, 24.96) * mm, "end": v(64.15, 23.96) * mm});
            skLineSegment(sketch, "E717", {"start": v(64.15, 23.96) * mm, "end": v(50.15, 23.96) * mm});
            skLineSegment(sketch, "E718", {"start": v(50.15, 23.96) * mm, "end": v(50.15, 24.96) * mm});
            skLineSegment(sketch, "E719", {"start": v(50.15, 24.96) * mm, "end": v(49.35, 24.96) * mm});
            skLineSegment(sketch, "E720", {"start": v(49.35, 24.96) * mm, "end": v(49.35, 28.06) * mm});
            skLineSegment(sketch, "E721", {"start": v(49.35, 28.06) * mm, "end": v(50.15, 28.06) * mm});
            skLineSegment(sketch, "E722", {"start": v(50.15, 28.06) * mm, "end": v(50.15, 33.86) * mm});
            skLineSegment(sketch, "E723", {"start": v(50.15, 33.86) * mm, "end": v(49.35, 33.86) * mm});
            skLineSegment(sketch, "E724", {"start": v(49.35, 33.86) * mm, "end": v(49.35, 36.96) * mm});
            skLineSegment(sketch, "E725", {"start": v(49.35, 36.96) * mm, "end": v(50.15, 36.96) * mm});
            skLineSegment(sketch, "E726", {"start": v(50.15, 36.96) * mm, "end": v(50.15, 37.96) * mm});
            skLineSegment(sketch, "E727", {"start": v(50.15, 37.96) * mm, "end": v(64.15, 37.96) * mm});
            skLineSegment(sketch, "E728", {"start": v(64.15, 37.96) * mm, "end": v(64.15, 36.96) * mm});
            skLineSegment(sketch, "E729", {"start": v(64.15, 36.96) * mm, "end": v(64.95, 36.96) * mm});
            skLineSegment(sketch, "E730", {"start": v(64.95, 36.96) * mm, "end": v(64.95, 33.86) * mm});
            skLineSegment(sketch, "E731", {"start": v(64.95, 33.86) * mm, "end": v(64.15, 33.86) * mm});
            skLineSegment(sketch, "E732", {"start": v(64.15, 33.86) * mm, "end": v(64.15, 28.06) * mm});
            skLineSegment(sketch, "E733", {"start": v(64.15, 28.06) * mm, "end": v(64.95, 28.06) * mm});
            skLineSegment(sketch, "E734", {"start": v(64.95, 28.06) * mm, "end": v(64.95, 24.96) * mm});
            skLineSegment(sketch, "E735", {"start": v(64.95, 24.96) * mm, "end": v(64.15, 24.96) * mm});
            skLineSegment(sketch, "E736", {"start": v(64.15, 5.9) * mm, "end": v(64.15, 4.9) * mm});
            skLineSegment(sketch, "E737", {"start": v(64.15, 4.9) * mm, "end": v(50.15, 4.9) * mm});
            skLineSegment(sketch, "E738", {"start": v(50.15, 4.9) * mm, "end": v(50.15, 5.9) * mm});
            skLineSegment(sketch, "E739", {"start": v(50.15, 5.9) * mm, "end": v(49.35, 5.9) * mm});
            skLineSegment(sketch, "E740", {"start": v(49.35, 5.9) * mm, "end": v(49.35, 9) * mm});
            skLineSegment(sketch, "E741", {"start": v(49.35, 9) * mm, "end": v(50.15, 9) * mm});
            skLineSegment(sketch, "E742", {"start": v(50.15, 9) * mm, "end": v(50.15, 14.8) * mm});
            skLineSegment(sketch, "E743", {"start": v(50.15, 14.8) * mm, "end": v(49.35, 14.8) * mm});
            skLineSegment(sketch, "E744", {"start": v(49.35, 14.8) * mm, "end": v(49.35, 17.9) * mm});
            skLineSegment(sketch, "E745", {"start": v(49.35, 17.9) * mm, "end": v(50.15, 17.9) * mm});
            skLineSegment(sketch, "E746", {"start": v(50.15, 17.9) * mm, "end": v(50.15, 18.9) * mm});
            skLineSegment(sketch, "E747", {"start": v(50.15, 18.9) * mm, "end": v(64.15, 18.9) * mm});
            skLineSegment(sketch, "E748", {"start": v(64.15, 18.9) * mm, "end": v(64.15, 17.9) * mm});
            skLineSegment(sketch, "E749", {"start": v(64.15, 17.9) * mm, "end": v(64.95, 17.9) * mm});
            skLineSegment(sketch, "E750", {"start": v(64.95, 17.9) * mm, "end": v(64.95, 14.8) * mm});
            skLineSegment(sketch, "E751", {"start": v(64.95, 14.8) * mm, "end": v(64.15, 14.8) * mm});
            skLineSegment(sketch, "E752", {"start": v(64.15, 14.8) * mm, "end": v(64.15, 9) * mm});
            skLineSegment(sketch, "E753", {"start": v(64.15, 9) * mm, "end": v(64.95, 9) * mm});
            skLineSegment(sketch, "E754", {"start": v(64.95, 9) * mm, "end": v(64.95, 5.9) * mm});
            skLineSegment(sketch, "E755", {"start": v(64.95, 5.9) * mm, "end": v(64.15, 5.9) * mm});
            skLineSegment(sketch, "E756", {"start": v(64.15, -13.14) * mm, "end": v(64.15, -14.14) * mm});
            skLineSegment(sketch, "E757", {"start": v(64.15, -14.14) * mm, "end": v(50.15, -14.14) * mm});
            skLineSegment(sketch, "E758", {"start": v(50.15, -14.14) * mm, "end": v(50.15, -13.14) * mm});
            skLineSegment(sketch, "E759", {"start": v(50.15, -13.14) * mm, "end": v(49.35, -13.14) * mm});
            skLineSegment(sketch, "E760", {"start": v(49.35, -13.14) * mm, "end": v(49.35, -10.04) * mm});
            skLineSegment(sketch, "E761", {"start": v(49.35, -10.04) * mm, "end": v(50.15, -10.04) * mm});
            skLineSegment(sketch, "E762", {"start": v(50.15, -10.04) * mm, "end": v(50.15, -4.24) * mm});
            skLineSegment(sketch, "E763", {"start": v(50.15, -4.24) * mm, "end": v(49.35, -4.24) * mm});
            skLineSegment(sketch, "E764", {"start": v(49.35, -4.24) * mm, "end": v(49.35, -1.14) * mm});
            skLineSegment(sketch, "E765", {"start": v(49.35, -1.14) * mm, "end": v(50.15, -1.14) * mm});
            skLineSegment(sketch, "E766", {"start": v(50.15, -1.14) * mm, "end": v(50.15, -0.14) * mm});
            skLineSegment(sketch, "E767", {"start": v(50.15, -0.14) * mm, "end": v(64.15, -0.14) * mm});
            skLineSegment(sketch, "E768", {"start": v(64.15, -0.14) * mm, "end": v(64.15, -1.14) * mm});
            skLineSegment(sketch, "E769", {"start": v(64.15, -1.14) * mm, "end": v(64.95, -1.14) * mm});
            skLineSegment(sketch, "E770", {"start": v(64.95, -1.14) * mm, "end": v(64.95, -4.24) * mm});
            skLineSegment(sketch, "E771", {"start": v(64.95, -4.24) * mm, "end": v(64.15, -4.24) * mm});
            skLineSegment(sketch, "E772", {"start": v(64.15, -4.24) * mm, "end": v(64.15, -10.04) * mm});
            skLineSegment(sketch, "E773", {"start": v(64.15, -10.04) * mm, "end": v(64.95, -10.04) * mm});
            skLineSegment(sketch, "E774", {"start": v(64.95, -10.04) * mm, "end": v(64.95, -13.14) * mm});
            skLineSegment(sketch, "E775", {"start": v(64.95, -13.14) * mm, "end": v(64.15, -13.14) * mm});
            skLineSegment(sketch, "E776", {"start": v(64.15, -32.2) * mm, "end": v(64.15, -33.2) * mm});
            skLineSegment(sketch, "E777", {"start": v(64.15, -33.2) * mm, "end": v(50.15, -33.2) * mm});
            skLineSegment(sketch, "E778", {"start": v(50.15, -33.2) * mm, "end": v(50.15, -32.2) * mm});
            skLineSegment(sketch, "E779", {"start": v(50.15, -32.2) * mm, "end": v(49.35, -32.2) * mm});
            skLineSegment(sketch, "E780", {"start": v(49.35, -32.2) * mm, "end": v(49.35, -29.1) * mm});
            skLineSegment(sketch, "E781", {"start": v(49.35, -29.1) * mm, "end": v(50.15, -29.1) * mm});
            skLineSegment(sketch, "E782", {"start": v(50.15, -29.1) * mm, "end": v(50.15, -23.3) * mm});
            skLineSegment(sketch, "E783", {"start": v(50.15, -23.3) * mm, "end": v(49.35, -23.3) * mm});
            skLineSegment(sketch, "E784", {"start": v(49.35, -23.3) * mm, "end": v(49.35, -20.2) * mm});
            skLineSegment(sketch, "E785", {"start": v(49.35, -20.2) * mm, "end": v(50.15, -20.2) * mm});
            skLineSegment(sketch, "E786", {"start": v(50.15, -20.2) * mm, "end": v(50.15, -19.2) * mm});
            skLineSegment(sketch, "E787", {"start": v(50.15, -19.2) * mm, "end": v(64.15, -19.2) * mm});
            skLineSegment(sketch, "E788", {"start": v(64.15, -19.2) * mm, "end": v(64.15, -20.2) * mm});
            skLineSegment(sketch, "E789", {"start": v(64.15, -20.2) * mm, "end": v(64.95, -20.2) * mm});
            skLineSegment(sketch, "E790", {"start": v(64.95, -20.2) * mm, "end": v(64.95, -23.3) * mm});
            skLineSegment(sketch, "E791", {"start": v(64.95, -23.3) * mm, "end": v(64.15, -23.3) * mm});
            skLineSegment(sketch, "E792", {"start": v(64.15, -23.3) * mm, "end": v(64.15, -29.1) * mm});
            skLineSegment(sketch, "E793", {"start": v(64.15, -29.1) * mm, "end": v(64.95, -29.1) * mm});
            skLineSegment(sketch, "E794", {"start": v(64.95, -29.1) * mm, "end": v(64.95, -32.2) * mm});
            skLineSegment(sketch, "E795", {"start": v(64.95, -32.2) * mm, "end": v(64.15, -32.2) * mm});
            skLineSegment(sketch, "E796", {"start": v(81.9, -45.74) * mm, "end": v(81.9, -52.01) * mm});
            skLineSegment(sketch, "E797", {"start": v(81.9, -52.01) * mm, "end": v(80.27, -52.01) * mm});
            skLineSegment(sketch, "E798", {"start": v(80.27, -52.01) * mm, "end": v(80.27, -53) * mm});
            skLineSegment(sketch, "E799", {"start": v(80.27, -53) * mm, "end": v(76.98, -53) * mm});
            skLineSegment(sketch, "E800", {"start": v(76.98, -53) * mm, "end": v(76.98, -52.01) * mm});
            skLineSegment(sketch, "E801", {"start": v(76.98, -52.01) * mm, "end": v(75.25, -52.01) * mm});
            skLineSegment(sketch, "E802", {"start": v(75.25, -52.01) * mm, "end": v(75.25, -51.21) * mm});
            skLineSegment(sketch, "E803", {"start": v(75.25, -51.21) * mm, "end": v(74.48, -51.21) * mm});
            skLineSegment(sketch, "E804", {"start": v(74.48, -51.21) * mm, "end": v(74.48, -51.24) * mm});
            skLineSegment(sketch, "E805", {"start": v(74.48, -51.24) * mm, "end": v(73.68, -51.24) * mm});
            skLineSegment(sketch, "E806", {"start": v(73.68, -51.24) * mm, "end": v(73.68, -52.24) * mm});
            skLineSegment(sketch, "E807", {"start": v(73.68, -52.24) * mm, "end": v(59.68, -52.24) * mm});
            skLineSegment(sketch, "E808", {"start": v(59.68, -52.24) * mm, "end": v(59.68, -51.24) * mm});
            skLineSegment(sketch, "E809", {"start": v(59.68, -51.24) * mm, "end": v(58.87, -51.24) * mm});
            skLineSegment(sketch, "E810", {"start": v(58.87, -51.24) * mm, "end": v(58.87, -51.21) * mm});
            skLineSegment(sketch, "E811", {"start": v(58.87, -51.21) * mm, "end": v(58.1, -51.21) * mm});
            skLineSegment(sketch, "E812", {"start": v(58.1, -51.21) * mm, "end": v(58.1, -52.01) * mm});
            skLineSegment(sketch, "E813", {"start": v(58.1, -52.01) * mm, "end": v(56.38, -52.01) * mm});
            skLineSegment(sketch, "E814", {"start": v(56.38, -52.01) * mm, "end": v(56.38, -53) * mm});
            skLineSegment(sketch, "E815", {"start": v(56.38, -53) * mm, "end": v(53.07, -53) * mm});
            skLineSegment(sketch, "E816", {"start": v(53.07, -53) * mm, "end": v(53.07, -52.01) * mm});
            skLineSegment(sketch, "E817", {"start": v(53.07, -52.01) * mm, "end": v(51.45, -52.01) * mm});
            skLineSegment(sketch, "E818", {"start": v(51.45, -52.01) * mm, "end": v(51.45, -45.74) * mm});
            skLineSegment(sketch, "E819", {"start": v(51.45, -45.74) * mm, "end": v(50.58, -45.74) * mm});
            skLineSegment(sketch, "E820", {"start": v(50.58, -45.74) * mm, "end": v(50.58, -42.94) * mm});
            skLineSegment(sketch, "E821", {"start": v(50.58, -42.94) * mm, "end": v(51.45, -42.94) * mm});
            skLineSegment(sketch, "E822", {"start": v(51.45, -42.94) * mm, "end": v(51.45, -39.71) * mm});
            skLineSegment(sketch, "E823", {"start": v(51.45, -39.71) * mm, "end": v(53.07, -39.71) * mm});
            skLineSegment(sketch, "E824", {"start": v(53.07, -39.71) * mm, "end": v(53.07, -38.8) * mm});
            skLineSegment(sketch, "E825", {"start": v(53.07, -38.8) * mm, "end": v(56.38, -38.8) * mm});
            skLineSegment(sketch, "E826", {"start": v(56.38, -38.8) * mm, "end": v(56.38, -39.71) * mm});
            skLineSegment(sketch, "E827", {"start": v(56.38, -39.71) * mm, "end": v(58.1, -39.71) * mm});
            skLineSegment(sketch, "E828", {"start": v(58.1, -39.71) * mm, "end": v(58.1, -40.51) * mm});
            skLineSegment(sketch, "E829", {"start": v(58.1, -40.51) * mm, "end": v(58.87, -40.51) * mm});
            skLineSegment(sketch, "E830", {"start": v(58.87, -40.51) * mm, "end": v(58.87, -39.24) * mm});
            skLineSegment(sketch, "E831", {"start": v(58.87, -39.24) * mm, "end": v(59.68, -39.24) * mm});
            skLineSegment(sketch, "E832", {"start": v(59.68, -39.24) * mm, "end": v(59.68, -38.24) * mm});
            skLineSegment(sketch, "E833", {"start": v(59.68, -38.24) * mm, "end": v(73.68, -38.24) * mm});
            skLineSegment(sketch, "E834", {"start": v(73.68, -38.24) * mm, "end": v(73.68, -39.24) * mm});
            skLineSegment(sketch, "E835", {"start": v(73.68, -39.24) * mm, "end": v(74.48, -39.24) * mm});
            skLineSegment(sketch, "E836", {"start": v(74.48, -39.24) * mm, "end": v(74.48, -40.51) * mm});
            skLineSegment(sketch, "E837", {"start": v(74.48, -40.51) * mm, "end": v(75.25, -40.51) * mm});
            skLineSegment(sketch, "E838", {"start": v(75.25, -40.51) * mm, "end": v(75.25, -39.71) * mm});
            skLineSegment(sketch, "E839", {"start": v(75.25, -39.71) * mm, "end": v(76.98, -39.71) * mm});
            skLineSegment(sketch, "E840", {"start": v(76.98, -39.71) * mm, "end": v(76.98, -38.8) * mm});
            skLineSegment(sketch, "E841", {"start": v(76.98, -38.8) * mm, "end": v(80.27, -38.8) * mm});
            skLineSegment(sketch, "E842", {"start": v(80.27, -38.8) * mm, "end": v(80.27, -39.71) * mm});
            skLineSegment(sketch, "E843", {"start": v(80.27, -39.71) * mm, "end": v(81.9, -39.71) * mm});
            skLineSegment(sketch, "E844", {"start": v(81.9, -39.71) * mm, "end": v(81.9, -42.94) * mm});
            skLineSegment(sketch, "E845", {"start": v(81.9, -42.94) * mm, "end": v(82.78, -42.94) * mm});
            skLineSegment(sketch, "E846", {"start": v(82.78, -42.94) * mm, "end": v(82.78, -45.74) * mm});
            skLineSegment(sketch, "E847", {"start": v(82.78, -45.74) * mm, "end": v(81.9, -45.74) * mm});
            skLineSegment(sketch, "E848", {"start": v(83.2, 24.96) * mm, "end": v(83.2, 23.96) * mm});
            skLineSegment(sketch, "E849", {"start": v(83.2, 23.96) * mm, "end": v(69.2, 23.96) * mm});
            skLineSegment(sketch, "E850", {"start": v(69.2, 23.96) * mm, "end": v(69.2, 24.96) * mm});
            skLineSegment(sketch, "E851", {"start": v(69.2, 24.96) * mm, "end": v(68.4, 24.96) * mm});
            skLineSegment(sketch, "E852", {"start": v(68.4, 24.96) * mm, "end": v(68.4, 28.06) * mm});
            skLineSegment(sketch, "E853", {"start": v(68.4, 28.06) * mm, "end": v(69.2, 28.06) * mm});
            skLineSegment(sketch, "E854", {"start": v(69.2, 28.06) * mm, "end": v(69.2, 33.86) * mm});
            skLineSegment(sketch, "E855", {"start": v(69.2, 33.86) * mm, "end": v(68.4, 33.86) * mm});
            skLineSegment(sketch, "E856", {"start": v(68.4, 33.86) * mm, "end": v(68.4, 36.96) * mm});
            skLineSegment(sketch, "E857", {"start": v(68.4, 36.96) * mm, "end": v(69.2, 36.96) * mm});
            skLineSegment(sketch, "E858", {"start": v(69.2, 36.96) * mm, "end": v(69.2, 37.96) * mm});
            skLineSegment(sketch, "E859", {"start": v(69.2, 37.96) * mm, "end": v(83.2, 37.96) * mm});
            skLineSegment(sketch, "E860", {"start": v(83.2, 37.96) * mm, "end": v(83.2, 36.96) * mm});
            skLineSegment(sketch, "E861", {"start": v(83.2, 36.96) * mm, "end": v(84, 36.96) * mm});
            skLineSegment(sketch, "E862", {"start": v(84, 36.96) * mm, "end": v(84, 33.86) * mm});
            skLineSegment(sketch, "E863", {"start": v(84, 33.86) * mm, "end": v(83.2, 33.86) * mm});
            skLineSegment(sketch, "E864", {"start": v(83.2, 33.86) * mm, "end": v(83.2, 28.06) * mm});
            skLineSegment(sketch, "E865", {"start": v(83.2, 28.06) * mm, "end": v(84, 28.06) * mm});
            skLineSegment(sketch, "E866", {"start": v(84, 28.06) * mm, "end": v(84, 24.96) * mm});
            skLineSegment(sketch, "E867", {"start": v(84, 24.96) * mm, "end": v(83.2, 24.96) * mm});
            skLineSegment(sketch, "E868", {"start": v(83.2, 5.9) * mm, "end": v(83.2, 4.9) * mm});
            skLineSegment(sketch, "E869", {"start": v(83.2, 4.9) * mm, "end": v(69.2, 4.9) * mm});
            skLineSegment(sketch, "E870", {"start": v(69.2, 4.9) * mm, "end": v(69.2, 5.9) * mm});
            skLineSegment(sketch, "E871", {"start": v(69.2, 5.9) * mm, "end": v(68.4, 5.9) * mm});
            skLineSegment(sketch, "E872", {"start": v(68.4, 5.9) * mm, "end": v(68.4, 9) * mm});
            skLineSegment(sketch, "E873", {"start": v(68.4, 9) * mm, "end": v(69.2, 9) * mm});
            skLineSegment(sketch, "E874", {"start": v(69.2, 9) * mm, "end": v(69.2, 14.8) * mm});
            skLineSegment(sketch, "E875", {"start": v(69.2, 14.8) * mm, "end": v(68.4, 14.8) * mm});
            skLineSegment(sketch, "E876", {"start": v(68.4, 14.8) * mm, "end": v(68.4, 17.9) * mm});
            skLineSegment(sketch, "E877", {"start": v(68.4, 17.9) * mm, "end": v(69.2, 17.9) * mm});
            skLineSegment(sketch, "E878", {"start": v(69.2, 17.9) * mm, "end": v(69.2, 18.9) * mm});
            skLineSegment(sketch, "E879", {"start": v(69.2, 18.9) * mm, "end": v(83.2, 18.9) * mm});
            skLineSegment(sketch, "E880", {"start": v(83.2, 18.9) * mm, "end": v(83.2, 17.9) * mm});
            skLineSegment(sketch, "E881", {"start": v(83.2, 17.9) * mm, "end": v(84, 17.9) * mm});
            skLineSegment(sketch, "E882", {"start": v(84, 17.9) * mm, "end": v(84, 14.8) * mm});
            skLineSegment(sketch, "E883", {"start": v(84, 14.8) * mm, "end": v(83.2, 14.8) * mm});
            skLineSegment(sketch, "E884", {"start": v(83.2, 14.8) * mm, "end": v(83.2, 9) * mm});
            skLineSegment(sketch, "E885", {"start": v(83.2, 9) * mm, "end": v(84, 9) * mm});
            skLineSegment(sketch, "E886", {"start": v(84, 9) * mm, "end": v(84, 5.9) * mm});
            skLineSegment(sketch, "E887", {"start": v(84, 5.9) * mm, "end": v(83.2, 5.9) * mm});
            skLineSegment(sketch, "E888", {"start": v(83.2, -13.14) * mm, "end": v(83.2, -14.14) * mm});
            skLineSegment(sketch, "E889", {"start": v(83.2, -14.14) * mm, "end": v(69.2, -14.14) * mm});
            skLineSegment(sketch, "E890", {"start": v(69.2, -14.14) * mm, "end": v(69.2, -13.14) * mm});
            skLineSegment(sketch, "E891", {"start": v(69.2, -13.14) * mm, "end": v(68.4, -13.14) * mm});
            skLineSegment(sketch, "E892", {"start": v(68.4, -13.14) * mm, "end": v(68.4, -10.04) * mm});
            skLineSegment(sketch, "E893", {"start": v(68.4, -10.04) * mm, "end": v(69.2, -10.04) * mm});
            skLineSegment(sketch, "E894", {"start": v(69.2, -10.04) * mm, "end": v(69.2, -4.24) * mm});
            skLineSegment(sketch, "E895", {"start": v(69.2, -4.24) * mm, "end": v(68.4, -4.24) * mm});
            skLineSegment(sketch, "E896", {"start": v(68.4, -4.24) * mm, "end": v(68.4, -1.14) * mm});
            skLineSegment(sketch, "E897", {"start": v(68.4, -1.14) * mm, "end": v(69.2, -1.14) * mm});
            skLineSegment(sketch, "E898", {"start": v(69.2, -1.14) * mm, "end": v(69.2, -0.14) * mm});
            skLineSegment(sketch, "E899", {"start": v(69.2, -0.14) * mm, "end": v(83.2, -0.14) * mm});
            skLineSegment(sketch, "E900", {"start": v(83.2, -0.14) * mm, "end": v(83.2, -1.14) * mm});
            skLineSegment(sketch, "E901", {"start": v(83.2, -1.14) * mm, "end": v(84, -1.14) * mm});
            skLineSegment(sketch, "E902", {"start": v(84, -1.14) * mm, "end": v(84, -4.24) * mm});
            skLineSegment(sketch, "E903", {"start": v(84, -4.24) * mm, "end": v(83.2, -4.24) * mm});
            skLineSegment(sketch, "E904", {"start": v(83.2, -4.24) * mm, "end": v(83.2, -10.04) * mm});
            skLineSegment(sketch, "E905", {"start": v(83.2, -10.04) * mm, "end": v(84, -10.04) * mm});
            skLineSegment(sketch, "E906", {"start": v(84, -10.04) * mm, "end": v(84, -13.14) * mm});
            skLineSegment(sketch, "E907", {"start": v(84, -13.14) * mm, "end": v(83.2, -13.14) * mm});
            skLineSegment(sketch, "E908", {"start": v(83.2, -32.2) * mm, "end": v(83.2, -33.2) * mm});
            skLineSegment(sketch, "E909", {"start": v(83.2, -33.2) * mm, "end": v(69.2, -33.2) * mm});
            skLineSegment(sketch, "E910", {"start": v(69.2, -33.2) * mm, "end": v(69.2, -32.2) * mm});
            skLineSegment(sketch, "E911", {"start": v(69.2, -32.2) * mm, "end": v(68.4, -32.2) * mm});
            skLineSegment(sketch, "E912", {"start": v(68.4, -32.2) * mm, "end": v(68.4, -29.1) * mm});
            skLineSegment(sketch, "E913", {"start": v(68.4, -29.1) * mm, "end": v(69.2, -29.1) * mm});
            skLineSegment(sketch, "E914", {"start": v(69.2, -29.1) * mm, "end": v(69.2, -23.3) * mm});
            skLineSegment(sketch, "E915", {"start": v(69.2, -23.3) * mm, "end": v(68.4, -23.3) * mm});
            skLineSegment(sketch, "E916", {"start": v(68.4, -23.3) * mm, "end": v(68.4, -20.2) * mm});
            skLineSegment(sketch, "E917", {"start": v(68.4, -20.2) * mm, "end": v(69.2, -20.2) * mm});
            skLineSegment(sketch, "E918", {"start": v(69.2, -20.2) * mm, "end": v(69.2, -19.2) * mm});
            skLineSegment(sketch, "E919", {"start": v(69.2, -19.2) * mm, "end": v(83.2, -19.2) * mm});
            skLineSegment(sketch, "E920", {"start": v(83.2, -19.2) * mm, "end": v(83.2, -20.2) * mm});
            skLineSegment(sketch, "E921", {"start": v(83.2, -20.2) * mm, "end": v(84, -20.2) * mm});
            skLineSegment(sketch, "E922", {"start": v(84, -20.2) * mm, "end": v(84, -23.3) * mm});
            skLineSegment(sketch, "E923", {"start": v(84, -23.3) * mm, "end": v(83.2, -23.3) * mm});
            skLineSegment(sketch, "E924", {"start": v(83.2, -23.3) * mm, "end": v(83.2, -29.1) * mm});
            skLineSegment(sketch, "E925", {"start": v(83.2, -29.1) * mm, "end": v(84, -29.1) * mm});
            skLineSegment(sketch, "E926", {"start": v(84, -29.1) * mm, "end": v(84, -32.2) * mm});
            skLineSegment(sketch, "E927", {"start": v(84, -32.2) * mm, "end": v(83.2, -32.2) * mm});
            skLineSegment(sketch, "E928.bottom", {"start": v(-84, 38.76) * mm, "end": v(-68.4, 38.76) * mm});
            skLineSegment(sketch, "E928.top", {"start": v(-84, 23.16) * mm, "end": v(-68.4, 23.16) * mm});
            skLineSegment(sketch, "E928.left", {"start": v(-84, 38.76) * mm, "end": v(-84, 23.16) * mm});
            skLineSegment(sketch, "E928.right", {"start": v(-68.4, 38.76) * mm, "end": v(-68.4, 23.16) * mm});
            skLineSegment(sketch, "E929.bottom", {"start": v(-84, 19.7) * mm, "end": v(-68.4, 19.7) * mm});
            skLineSegment(sketch, "E929.top", {"start": v(-84, 4.1) * mm, "end": v(-68.4, 4.1) * mm});
            skLineSegment(sketch, "E929.left", {"start": v(-84, 19.7) * mm, "end": v(-84, 4.1) * mm});
            skLineSegment(sketch, "E929.right", {"start": v(-68.4, 19.7) * mm, "end": v(-68.4, 4.1) * mm});
            skLineSegment(sketch, "E930.bottom", {"start": v(-84, 0.66) * mm, "end": v(-68.4, 0.66) * mm});
            skLineSegment(sketch, "E930.top", {"start": v(-84, -14.94) * mm, "end": v(-68.4, -14.94) * mm});
            skLineSegment(sketch, "E930.left", {"start": v(-84, 0.66) * mm, "end": v(-84, -14.94) * mm});
            skLineSegment(sketch, "E930.right", {"start": v(-68.4, 0.66) * mm, "end": v(-68.4, -14.94) * mm});
            skLineSegment(sketch, "E931.bottom", {"start": v(-64.95, 43.52) * mm, "end": v(-49.35, 43.52) * mm});
            skLineSegment(sketch, "E931.top", {"start": v(-64.95, 27.92) * mm, "end": v(-49.35, 27.92) * mm});
            skLineSegment(sketch, "E931.left", {"start": v(-64.95, 43.52) * mm, "end": v(-64.95, 27.92) * mm});
            skLineSegment(sketch, "E931.right", {"start": v(-49.35, 43.52) * mm, "end": v(-49.35, 27.92) * mm});
            skLineSegment(sketch, "E932.bottom", {"start": v(-64.95, 24.47) * mm, "end": v(-49.35, 24.47) * mm});
            skLineSegment(sketch, "E932.top", {"start": v(-64.95, 8.87) * mm, "end": v(-49.35, 8.87) * mm});
            skLineSegment(sketch, "E932.left", {"start": v(-64.95, 24.47) * mm, "end": v(-64.95, 8.87) * mm});
            skLineSegment(sketch, "E932.right", {"start": v(-49.35, 24.47) * mm, "end": v(-49.35, 8.87) * mm});
            skLineSegment(sketch, "E933.bottom", {"start": v(-64.95, 5.42) * mm, "end": v(-49.35, 5.42) * mm});
            skLineSegment(sketch, "E933.top", {"start": v(-64.95, -10.18) * mm, "end": v(-49.35, -10.18) * mm});
            skLineSegment(sketch, "E933.left", {"start": v(-64.95, 5.42) * mm, "end": v(-64.95, -10.18) * mm});
            skLineSegment(sketch, "E933.right", {"start": v(-49.35, 5.42) * mm, "end": v(-49.35, -10.18) * mm});
            skLineSegment(sketch, "E934.bottom", {"start": v(-64.95, -13.63) * mm, "end": v(-49.35, -13.63) * mm});
            skLineSegment(sketch, "E934.top", {"start": v(-64.95, -29.23) * mm, "end": v(-49.35, -29.23) * mm});
            skLineSegment(sketch, "E934.left", {"start": v(-64.95, -13.63) * mm, "end": v(-64.95, -29.23) * mm});
            skLineSegment(sketch, "E934.right", {"start": v(-49.35, -13.63) * mm, "end": v(-49.35, -29.23) * mm});
            skLineSegment(sketch, "E935.bottom", {"start": v(-64.95, -32.68) * mm, "end": v(-49.35, -32.68) * mm});
            skLineSegment(sketch, "E935.top", {"start": v(-64.95, -48.28) * mm, "end": v(-49.35, -48.28) * mm});
            skLineSegment(sketch, "E935.left", {"start": v(-64.95, -32.68) * mm, "end": v(-64.95, -48.28) * mm});
            skLineSegment(sketch, "E935.right", {"start": v(-49.35, -32.68) * mm, "end": v(-49.35, -48.28) * mm});
            skLineSegment(sketch, "E936.bottom", {"start": v(-45.9, 53.04) * mm, "end": v(-30.3, 53.04) * mm});
            skLineSegment(sketch, "E936.top", {"start": v(-45.9, 37.44) * mm, "end": v(-30.3, 37.44) * mm});
            skLineSegment(sketch, "E936.left", {"start": v(-45.9, 53.04) * mm, "end": v(-45.9, 37.44) * mm});
            skLineSegment(sketch, "E936.right", {"start": v(-30.3, 53.04) * mm, "end": v(-30.3, 37.44) * mm});
            skLineSegment(sketch, "E937.bottom", {"start": v(-45.9, 34) * mm, "end": v(-30.3, 34) * mm});
            skLineSegment(sketch, "E937.top", {"start": v(-45.9, 17.93) * mm, "end": v(-30.3, 17.93) * mm});
            skLineSegment(sketch, "E937.left", {"start": v(-45.9, 34) * mm, "end": v(-45.9, 17.93) * mm});
            skLineSegment(sketch, "E937.right", {"start": v(-30.3, 34) * mm, "end": v(-30.3, 17.93) * mm});
            skLineSegment(sketch, "E938.bottom", {"start": v(-45.9, 14.94) * mm, "end": v(-30.3, 14.94) * mm});
            skLineSegment(sketch, "E938.top", {"start": v(-45.9, -0.66) * mm, "end": v(-30.3, -0.66) * mm});
            skLineSegment(sketch, "E938.left", {"start": v(-45.9, 14.94) * mm, "end": v(-45.9, -0.66) * mm});
            skLineSegment(sketch, "E938.right", {"start": v(-30.3, 14.94) * mm, "end": v(-30.3, -0.66) * mm});
            skLineSegment(sketch, "E939.bottom", {"start": v(-45.9, -4.1) * mm, "end": v(-30.3, -4.1) * mm});
            skLineSegment(sketch, "E939.top", {"start": v(-45.9, -19.7) * mm, "end": v(-30.3, -19.7) * mm});
            skLineSegment(sketch, "E939.left", {"start": v(-45.9, -4.1) * mm, "end": v(-45.9, -19.7) * mm});
            skLineSegment(sketch, "E939.right", {"start": v(-30.3, -4.1) * mm, "end": v(-30.3, -19.7) * mm});
            skLineSegment(sketch, "E940.bottom", {"start": v(-45.9, -23.16) * mm, "end": v(-30.3, -23.16) * mm});
            skLineSegment(sketch, "E940.top", {"start": v(-45.9, -38.76) * mm, "end": v(-30.3, -38.76) * mm});
            skLineSegment(sketch, "E940.left", {"start": v(-45.9, -23.16) * mm, "end": v(-45.9, -38.76) * mm});
            skLineSegment(sketch, "E940.right", {"start": v(-30.3, -23.16) * mm, "end": v(-30.3, -38.76) * mm});
            skLineSegment(sketch, "E941.bottom", {"start": v(-26.85, -27.92) * mm, "end": v(-11.25, -27.92) * mm});
            skLineSegment(sketch, "E941.top", {"start": v(-26.85, -43.52) * mm, "end": v(-11.25, -43.52) * mm});
            skLineSegment(sketch, "E941.left", {"start": v(-26.85, -27.92) * mm, "end": v(-26.85, -43.52) * mm});
            skLineSegment(sketch, "E941.right", {"start": v(-11.25, -27.92) * mm, "end": v(-11.25, -43.52) * mm});
            skLineSegment(sketch, "E942.bottom", {"start": v(-26.85, -8.87) * mm, "end": v(-11.25, -8.87) * mm});
            skLineSegment(sketch, "E942.top", {"start": v(-26.85, -24.47) * mm, "end": v(-11.25, -24.47) * mm});
            skLineSegment(sketch, "E942.left", {"start": v(-26.85, -8.87) * mm, "end": v(-26.85, -24.47) * mm});
            skLineSegment(sketch, "E942.right", {"start": v(-11.25, -8.87) * mm, "end": v(-11.25, -24.47) * mm});
            skPoint(sketch, "E943.oppositeSnap0", {"position": v(-11.25, -2.07) * mm});
            skLineSegment(sketch, "E943.bottom", {"start": v(-26.85, 10.18) * mm, "end": v(-11.25, 10.18) * mm});
            skLineSegment(sketch, "E943.top", {"start": v(-26.85, -5.42) * mm, "end": v(-11.25, -5.42) * mm});
            skLineSegment(sketch, "E943.left", {"start": v(-26.85, 10.18) * mm, "end": v(-26.85, -5.42) * mm});
            skLineSegment(sketch, "E943.right", {"start": v(-11.25, 10.18) * mm, "end": v(-11.25, -5.42) * mm});
            skLineSegment(sketch, "E944.bottom", {"start": v(-26.85, 29.23) * mm, "end": v(-11.25, 29.23) * mm});
            skLineSegment(sketch, "E944.top", {"start": v(-26.85, 13.63) * mm, "end": v(-11.25, 13.63) * mm});
            skLineSegment(sketch, "E944.left", {"start": v(-26.85, 29.23) * mm, "end": v(-26.85, 13.63) * mm});
            skLineSegment(sketch, "E944.right", {"start": v(-11.25, 29.23) * mm, "end": v(-11.25, 13.63) * mm});
            skLineSegment(sketch, "E945.bottom", {"start": v(-26.85, 48.28) * mm, "end": v(-11.25, 48.28) * mm});
            skLineSegment(sketch, "E945.top", {"start": v(-26.85, 32.68) * mm, "end": v(-11.25, 32.68) * mm});
            skLineSegment(sketch, "E945.left", {"start": v(-26.85, 48.28) * mm, "end": v(-26.85, 32.68) * mm});
            skLineSegment(sketch, "E945.right", {"start": v(-11.25, 48.28) * mm, "end": v(-11.25, 32.68) * mm});
            skLineSegment(sketch, "E946.bottom", {"start": v(-7.8, 43.52) * mm, "end": v(7.8, 43.52) * mm});
            skLineSegment(sketch, "E946.top", {"start": v(-7.8, 27.92) * mm, "end": v(7.8, 27.92) * mm});
            skLineSegment(sketch, "E946.left", {"start": v(-7.8, 43.52) * mm, "end": v(-7.8, 27.92) * mm});
            skLineSegment(sketch, "E946.right", {"start": v(7.8, 43.52) * mm, "end": v(7.8, 27.92) * mm});
            skLineSegment(sketch, "E947.bottom", {"start": v(-7.8, 24.47) * mm, "end": v(7.8, 24.47) * mm});
            skLineSegment(sketch, "E947.top", {"start": v(-7.8, 8.87) * mm, "end": v(7.8, 8.87) * mm});
            skLineSegment(sketch, "E947.left", {"start": v(-7.8, 24.47) * mm, "end": v(-7.8, 8.87) * mm});
            skLineSegment(sketch, "E947.right", {"start": v(7.8, 24.47) * mm, "end": v(7.8, 8.87) * mm});
            skLineSegment(sketch, "E948.bottom", {"start": v(-7.8, 5.42) * mm, "end": v(7.8, 5.42) * mm});
            skLineSegment(sketch, "E948.top", {"start": v(-7.8, -10.18) * mm, "end": v(7.8, -10.18) * mm});
            skLineSegment(sketch, "E948.left", {"start": v(-7.8, 5.42) * mm, "end": v(-7.8, -10.18) * mm});
            skLineSegment(sketch, "E948.right", {"start": v(7.8, 5.42) * mm, "end": v(7.8, -10.18) * mm});
            skLineSegment(sketch, "E949.bottom", {"start": v(11.25, 38.76) * mm, "end": v(26.85, 38.76) * mm});
            skLineSegment(sketch, "E949.top", {"start": v(11.25, 23.16) * mm, "end": v(26.85, 23.16) * mm});
            skLineSegment(sketch, "E949.left", {"start": v(11.25, 38.76) * mm, "end": v(11.25, 23.16) * mm});
            skLineSegment(sketch, "E949.right", {"start": v(26.85, 38.76) * mm, "end": v(26.85, 23.16) * mm});
            skLineSegment(sketch, "E950.bottom", {"start": v(11.25, 19.7) * mm, "end": v(26.85, 19.7) * mm});
            skLineSegment(sketch, "E950.top", {"start": v(11.25, 4.1) * mm, "end": v(26.85, 4.1) * mm});
            skLineSegment(sketch, "E950.left", {"start": v(11.25, 19.7) * mm, "end": v(11.25, 4.1) * mm});
            skLineSegment(sketch, "E950.right", {"start": v(26.85, 19.7) * mm, "end": v(26.85, 4.1) * mm});
            skLineSegment(sketch, "E951.bottom", {"start": v(11.25, 0.66) * mm, "end": v(26.85, 0.66) * mm});
            skLineSegment(sketch, "E951.top", {"start": v(11.25, -14.94) * mm, "end": v(26.85, -14.94) * mm});
            skLineSegment(sketch, "E951.left", {"start": v(11.25, 0.66) * mm, "end": v(11.25, -14.94) * mm});
            skLineSegment(sketch, "E951.right", {"start": v(26.85, 0.66) * mm, "end": v(26.85, -14.94) * mm});
            skLineSegment(sketch, "E952.bottom", {"start": v(30.3, 38.76) * mm, "end": v(45.9, 38.76) * mm});
            skLineSegment(sketch, "E952.top", {"start": v(30.3, 23.16) * mm, "end": v(45.9, 23.16) * mm});
            skLineSegment(sketch, "E952.left", {"start": v(30.3, 38.76) * mm, "end": v(30.3, 23.16) * mm});
            skLineSegment(sketch, "E952.right", {"start": v(45.9, 38.76) * mm, "end": v(45.9, 23.16) * mm});
            skLineSegment(sketch, "E953.bottom", {"start": v(30.3, 19.7) * mm, "end": v(45.9, 19.7) * mm});
            skLineSegment(sketch, "E953.top", {"start": v(30.3, 4.1) * mm, "end": v(45.9, 4.1) * mm});
            skLineSegment(sketch, "E953.left", {"start": v(30.3, 19.7) * mm, "end": v(30.3, 4.1) * mm});
            skLineSegment(sketch, "E953.right", {"start": v(45.9, 19.7) * mm, "end": v(45.9, 4.1) * mm});
            skLineSegment(sketch, "E954.bottom", {"start": v(30.3, 0.66) * mm, "end": v(45.9, 0.66) * mm});
            skLineSegment(sketch, "E954.top", {"start": v(30.3, -14.94) * mm, "end": v(45.9, -14.94) * mm});
            skLineSegment(sketch, "E954.left", {"start": v(30.3, 0.66) * mm, "end": v(30.3, -14.94) * mm});
            skLineSegment(sketch, "E954.right", {"start": v(45.9, 0.66) * mm, "end": v(45.9, -14.94) * mm});
            skLineSegment(sketch, "E955.bottom", {"start": v(49.35, 38.76) * mm, "end": v(64.95, 38.76) * mm});
            skLineSegment(sketch, "E955.top", {"start": v(49.35, 23.16) * mm, "end": v(64.95, 23.16) * mm});
            skLineSegment(sketch, "E955.left", {"start": v(49.35, 38.76) * mm, "end": v(49.35, 23.16) * mm});
            skLineSegment(sketch, "E955.right", {"start": v(64.95, 38.76) * mm, "end": v(64.95, 23.16) * mm});
            skLineSegment(sketch, "E956.bottom", {"start": v(49.35, 19.7) * mm, "end": v(64.95, 19.7) * mm});
            skLineSegment(sketch, "E956.top", {"start": v(49.35, 4.1) * mm, "end": v(64.95, 4.1) * mm});
            skLineSegment(sketch, "E956.left", {"start": v(49.35, 19.7) * mm, "end": v(49.35, 4.1) * mm});
            skLineSegment(sketch, "E956.right", {"start": v(64.95, 19.7) * mm, "end": v(64.95, 4.1) * mm});
            skLineSegment(sketch, "E957.bottom", {"start": v(49.35, 0.66) * mm, "end": v(64.95, 0.66) * mm});
            skLineSegment(sketch, "E957.top", {"start": v(49.35, -14.94) * mm, "end": v(64.95, -14.94) * mm});
            skLineSegment(sketch, "E957.left", {"start": v(49.35, 0.66) * mm, "end": v(49.35, -14.94) * mm});
            skLineSegment(sketch, "E957.right", {"start": v(64.95, 0.66) * mm, "end": v(64.95, -14.94) * mm});
            skLineSegment(sketch, "E958.bottom", {"start": v(68.4, 38.76) * mm, "end": v(84, 38.76) * mm});
            skLineSegment(sketch, "E958.top", {"start": v(68.4, 23.16) * mm, "end": v(84, 23.16) * mm});
            skLineSegment(sketch, "E958.left", {"start": v(68.4, 38.76) * mm, "end": v(68.4, 23.16) * mm});
            skLineSegment(sketch, "E958.right", {"start": v(84, 38.76) * mm, "end": v(84, 23.16) * mm});
            skLineSegment(sketch, "E959.bottom", {"start": v(68.4, 19.7) * mm, "end": v(84, 19.7) * mm});
            skLineSegment(sketch, "E959.top", {"start": v(68.4, 4.1) * mm, "end": v(84, 4.1) * mm});
            skLineSegment(sketch, "E959.left", {"start": v(68.4, 19.7) * mm, "end": v(68.4, 4.1) * mm});
            skLineSegment(sketch, "E959.right", {"start": v(84, 19.7) * mm, "end": v(84, 4.1) * mm});
            skLineSegment(sketch, "E960.bottom", {"start": v(68.4, 0.66) * mm, "end": v(84, 0.66) * mm});
            skLineSegment(sketch, "E960.top", {"start": v(68.4, -14.94) * mm, "end": v(84, -14.94) * mm});
            skLineSegment(sketch, "E960.left", {"start": v(68.4, 0.66) * mm, "end": v(68.4, -14.94) * mm});
            skLineSegment(sketch, "E960.right", {"start": v(84, 0.66) * mm, "end": v(84, -14.94) * mm});
            skLineSegment(sketch, "E961.bottom", {"start": v(-7.8, -13.44) * mm, "end": v(7.8, -13.44) * mm});
            skLineSegment(sketch, "E961.top", {"start": v(-7.8, -29.57) * mm, "end": v(7.8, -29.57) * mm});
            skLineSegment(sketch, "E961.left", {"start": v(-7.8, -13.44) * mm, "end": v(-7.8, -29.57) * mm});
            skLineSegment(sketch, "E961.right", {"start": v(7.8, -13.44) * mm, "end": v(7.8, -29.57) * mm});
            skLineSegment(sketch, "E962.bottom", {"start": v(-7.8, -32.68) * mm, "end": v(7.8, -32.68) * mm});
            skLineSegment(sketch, "E962.top", {"start": v(-7.8, -48.28) * mm, "end": v(7.8, -48.28) * mm});
            skLineSegment(sketch, "E962.left", {"start": v(-7.8, -32.68) * mm, "end": v(-7.8, -48.28) * mm});
            skLineSegment(sketch, "E962.right", {"start": v(7.8, -32.68) * mm, "end": v(7.8, -48.28) * mm});
            skLineSegment(sketch, "E963.bottom", {"start": v(11.25, -18.4) * mm, "end": v(26.85, -18.4) * mm});
            skLineSegment(sketch, "E963.top", {"start": v(11.25, -34) * mm, "end": v(26.85, -34) * mm});
            skLineSegment(sketch, "E963.left", {"start": v(11.25, -18.4) * mm, "end": v(11.25, -34) * mm});
            skLineSegment(sketch, "E963.right", {"start": v(26.85, -18.4) * mm, "end": v(26.85, -34) * mm});
            skLineSegment(sketch, "E964.bottom", {"start": v(30.3, -18.4) * mm, "end": v(45.9, -18.4) * mm});
            skLineSegment(sketch, "E964.top", {"start": v(30.3, -34) * mm, "end": v(45.9, -34) * mm});
            skLineSegment(sketch, "E964.left", {"start": v(30.3, -18.4) * mm, "end": v(30.3, -34) * mm});
            skLineSegment(sketch, "E964.right", {"start": v(45.9, -18.4) * mm, "end": v(45.9, -34) * mm});
            skLineSegment(sketch, "E965.bottom", {"start": v(49.35, -18.4) * mm, "end": v(64.95, -18.4) * mm});
            skLineSegment(sketch, "E965.top", {"start": v(49.35, -34) * mm, "end": v(64.95, -34) * mm});
            skLineSegment(sketch, "E965.left", {"start": v(49.35, -18.4) * mm, "end": v(49.35, -34) * mm});
            skLineSegment(sketch, "E965.right", {"start": v(64.95, -18.4) * mm, "end": v(64.95, -34) * mm});
            skLineSegment(sketch, "E966.bottom", {"start": v(68.4, -18.4) * mm, "end": v(84, -18.4) * mm});
            skLineSegment(sketch, "E966.top", {"start": v(68.4, -34) * mm, "end": v(84, -34) * mm});
            skLineSegment(sketch, "E966.left", {"start": v(68.4, -18.4) * mm, "end": v(68.4, -34) * mm});
            skLineSegment(sketch, "E966.right", {"start": v(84, -18.4) * mm, "end": v(84, -34) * mm});
            skLineSegment(sketch, "E967.bottom", {"start": v(11.25, -37.44) * mm, "end": v(26.85, -37.44) * mm});
            skLineSegment(sketch, "E967.top", {"start": v(11.25, -53.04) * mm, "end": v(26.85, -53.04) * mm});
            skLineSegment(sketch, "E967.left", {"start": v(11.25, -37.44) * mm, "end": v(11.25, -53.04) * mm});
            skLineSegment(sketch, "E967.right", {"start": v(26.85, -37.44) * mm, "end": v(26.85, -53.04) * mm});
            skLineSegment(sketch, "E968.bottom", {"start": v(30.3, -37.44) * mm, "end": v(45.9, -37.44) * mm});
            skLineSegment(sketch, "E968.top", {"start": v(30.3, -53.04) * mm, "end": v(45.9, -53.04) * mm});
            skLineSegment(sketch, "E968.left", {"start": v(30.3, -37.44) * mm, "end": v(30.3, -53.04) * mm});
            skLineSegment(sketch, "E968.right", {"start": v(45.9, -37.44) * mm, "end": v(45.9, -53.04) * mm});
            skLineSegment(sketch, "E969.bottom", {"start": v(50.58, -37.44) * mm, "end": v(81.9, -37.44) * mm});
            skLineSegment(sketch, "E969.top", {"start": v(50.58, -54.35) * mm, "end": v(81.9, -54.35) * mm});
            skLineSegment(sketch, "E969.left", {"start": v(50.58, -37.44) * mm, "end": v(50.58, -54.35) * mm});
            skLineSegment(sketch, "E969.right", {"start": v(81.9, -37.44) * mm, "end": v(81.9, -54.35) * mm});
            skLineSegment(sketch, "E970.bottom", {"start": v(-67.56, -19.62) * mm, "end": v(-85.14, -19.62) * mm});
            skLineSegment(sketch, "E970.top", {"start": v(-67.56, -51.82) * mm, "end": v(-85.14, -51.82) * mm});
            skLineSegment(sketch, "E970.left", {"start": v(-67.56, -19.62) * mm, "end": v(-67.56, -51.82) * mm});
            skLineSegment(sketch, "E970.right", {"start": v(-85.14, -19.62) * mm, "end": v(-85.14, -51.82) * mm});
            skSolve(sketch);
        }
        {
            var Q0;
            Q0=makeQuery(id+"F0.imprint","IMPRINT",FACE,{"disambiguationData":[TD([[makeQuery(id+"F0.imprint","IMPRINT",EDGE,{"derivedFrom":sQuery(id+"F0.wireOp",EDGE,"E0")}),-1.0]])]});
            var Q1;
            {var subQ0=sQuery(id+"F0.wireOp",EDGE,"E65");Q1=makeQuery(id+"F0.imprint","IMPRINT",FACE,{"disambiguationData":[TD([[makeQuery(id+"F0.imprint","IMPRINT",EDGE,{"derivedFrom":subQ0}),1.0]])]});}
            var Q2;
            {var subQ0=sQuery(id+"F0.wireOp",EDGE,"E61");Q2=makeQuery(id+"F0.imprint","IMPRINT",FACE,{"disambiguationData":[TD([[makeQuery(id+"F0.imprint","IMPRINT",EDGE,{"derivedFrom":subQ0}),1.0]])]});}
            var Q3;
            Q3=makeQuery(id+"F0.imprint","IMPRINT",FACE,{"disambiguationData":[TD([[makeQuery(id+"F0.imprint","IMPRINT",EDGE,{"derivedFrom":sQuery(id+"F0.wireOp",EDGE,"E56")}),1.0]])]});
            var Q4;
            {var subQ0=sQuery(id+"F0.wireOp",EDGE,"E71");Q4=makeQuery(id+"F0.imprint","IMPRINT",FACE,{"disambiguationData":[TD([[makeQuery(id+"F0.imprint","IMPRINT",EDGE,{"derivedFrom":subQ0}),1.0]])]});}
            var Q5;
            {var subQ1=sQuery(id+"F0.wireOp",EDGE,"E85");Q5=makeQuery(id+"F0.imprint","IMPRINT",FACE,{"disambiguationData":[TD([[makeQuery(id+"F0.imprint","IMPRINT",EDGE,{"derivedFrom":subQ1}),1.0]])]});}
            var Q6;
            {var subQ0=sQuery(id+"F0.wireOp",EDGE,"E81");Q6=makeQuery(id+"F0.imprint","IMPRINT",FACE,{"disambiguationData":[TD([[makeQuery(id+"F0.imprint","IMPRINT",EDGE,{"derivedFrom":subQ0}),1.0]])]});}
            var Q7;
            Q7=makeQuery(id+"F0.imprint","IMPRINT",FACE,{"disambiguationData":[TD([[makeQuery(id+"F0.imprint","IMPRINT",EDGE,{"derivedFrom":sQuery(id+"F0.wireOp",EDGE,"E76")}),1.0]])]});
            var Q8;
            {var subQ0=sQuery(id+"F0.wireOp",EDGE,"E91");Q8=makeQuery(id+"F0.imprint","IMPRINT",FACE,{"disambiguationData":[TD([[makeQuery(id+"F0.imprint","IMPRINT",EDGE,{"derivedFrom":subQ0}),1.0]])]});}
            var Q9;
            Q9=makeQuery(id+"F0.imprint","IMPRINT",FACE,{"disambiguationData":[TD([[makeQuery(id+"F0.imprint","IMPRINT",EDGE,{"derivedFrom":sQuery(id+"F0.wireOp",EDGE,"E116")}),1.0]])]});
            var Q10;
            {var subQ0=sQuery(id+"F0.wireOp",EDGE,"E121");Q10=makeQuery(id+"F0.imprint","IMPRINT",FACE,{"disambiguationData":[TD([[makeQuery(id+"F0.imprint","IMPRINT",EDGE,{"derivedFrom":subQ0}),1.0]])]});}
            var Q11;
            {var subQ2=sQuery(id+"F0.wireOp",EDGE,"E125");Q11=makeQuery(id+"F0.imprint","IMPRINT",FACE,{"disambiguationData":[TD([[makeQuery(id+"F0.imprint","IMPRINT",EDGE,{"derivedFrom":subQ2}),1.0]])]});}
            var Q12;
            {var subQ0=sQuery(id+"F0.wireOp",EDGE,"E131");Q12=makeQuery(id+"F0.imprint","IMPRINT",FACE,{"disambiguationData":[TD([[makeQuery(id+"F0.imprint","IMPRINT",EDGE,{"derivedFrom":subQ0}),1.0]])]});}
            var Q13;
            {var subQ3=sQuery(id+"F0.wireOp",EDGE,"E145");Q13=makeQuery(id+"F0.imprint","IMPRINT",FACE,{"disambiguationData":[TD([[makeQuery(id+"F0.imprint","IMPRINT",EDGE,{"derivedFrom":subQ3}),1.0]])]});}
            var Q14;
            {var subQ0=sQuery(id+"F0.wireOp",EDGE,"E141");Q14=makeQuery(id+"F0.imprint","IMPRINT",FACE,{"disambiguationData":[TD([[makeQuery(id+"F0.imprint","IMPRINT",EDGE,{"derivedFrom":subQ0}),1.0]])]});}
            var Q15;
            {var subQ0=sQuery(id+"F0.wireOp",EDGE,"E151");Q15=makeQuery(id+"F0.imprint","IMPRINT",FACE,{"disambiguationData":[TD([[makeQuery(id+"F0.imprint","IMPRINT",EDGE,{"derivedFrom":subQ0}),1.0]])]});}
            var Q16;
            Q16=makeQuery(id+"F0.imprint","IMPRINT",FACE,{"disambiguationData":[TD([[makeQuery(id+"F0.imprint","IMPRINT",EDGE,{"derivedFrom":sQuery(id+"F0.wireOp",EDGE,"E136")}),1.0]])]});
            var Q17;
            Q17=makeQuery(id+"F0.imprint","IMPRINT",FACE,{"disambiguationData":[TD([[makeQuery(id+"F0.imprint","IMPRINT",EDGE,{"derivedFrom":sQuery(id+"F0.wireOp",EDGE,"E256")}),1.0]])]});
            var Q18;
            {var subQ0=sQuery(id+"F0.wireOp",EDGE,"E261");Q18=makeQuery(id+"F0.imprint","IMPRINT",FACE,{"disambiguationData":[TD([[makeQuery(id+"F0.imprint","IMPRINT",EDGE,{"derivedFrom":subQ0}),1.0]])]});}
            var Q19;
            {var subQ3=sQuery(id+"F0.wireOp",EDGE,"E265");Q19=makeQuery(id+"F0.imprint","IMPRINT",FACE,{"disambiguationData":[TD([[makeQuery(id+"F0.imprint","IMPRINT",EDGE,{"derivedFrom":subQ3}),1.0]])]});}
            var Q20;
            {var subQ0=sQuery(id+"F0.wireOp",EDGE,"E271");Q20=makeQuery(id+"F0.imprint","IMPRINT",FACE,{"disambiguationData":[TD([[makeQuery(id+"F0.imprint","IMPRINT",EDGE,{"derivedFrom":subQ0}),1.0]])]});}
            var Q21;
            Q21=makeQuery(id+"F0.imprint","IMPRINT",FACE,{"disambiguationData":[TD([[makeQuery(id+"F0.imprint","IMPRINT",EDGE,{"derivedFrom":sQuery(id+"F0.wireOp",EDGE,"E236")}),1.0]])]});
            var Q22;
            {var subQ0=sQuery(id+"F0.wireOp",EDGE,"E251");Q22=makeQuery(id+"F0.imprint","IMPRINT",FACE,{"disambiguationData":[TD([[makeQuery(id+"F0.imprint","IMPRINT",EDGE,{"derivedFrom":subQ0}),1.0]])]});}
            var Q23;
            {var subQ0=sQuery(id+"F0.wireOp",EDGE,"E241");Q23=makeQuery(id+"F0.imprint","IMPRINT",FACE,{"disambiguationData":[TD([[makeQuery(id+"F0.imprint","IMPRINT",EDGE,{"derivedFrom":subQ0}),1.0]])]});}
            var Q24;
            {var subQ3=sQuery(id+"F0.wireOp",EDGE,"E245");Q24=makeQuery(id+"F0.imprint","IMPRINT",FACE,{"disambiguationData":[TD([[makeQuery(id+"F0.imprint","IMPRINT",EDGE,{"derivedFrom":subQ3}),1.0]])]});}
            var Q25;
            Q25=makeQuery(id+"F0.imprint","IMPRINT",FACE,{"disambiguationData":[TD([[makeQuery(id+"F0.imprint","IMPRINT",EDGE,{"derivedFrom":sQuery(id+"F0.wireOp",EDGE,"E216")}),1.0]])]});
            var Q26;
            {var subQ0=sQuery(id+"F0.wireOp",EDGE,"E221");Q26=makeQuery(id+"F0.imprint","IMPRINT",FACE,{"disambiguationData":[TD([[makeQuery(id+"F0.imprint","IMPRINT",EDGE,{"derivedFrom":subQ0}),1.0]])]});}
            var Q27;
            {var subQ3=sQuery(id+"F0.wireOp",EDGE,"E225");Q27=makeQuery(id+"F0.imprint","IMPRINT",FACE,{"disambiguationData":[TD([[makeQuery(id+"F0.imprint","IMPRINT",EDGE,{"derivedFrom":subQ3}),1.0]])]});}
            var Q28;
            {var subQ0=sQuery(id+"F0.wireOp",EDGE,"E231");Q28=makeQuery(id+"F0.imprint","IMPRINT",FACE,{"disambiguationData":[TD([[makeQuery(id+"F0.imprint","IMPRINT",EDGE,{"derivedFrom":subQ0}),1.0]])]});}
            var Q29;
            {var subQ1=sQuery(id+"F0.wireOp",EDGE,"E105");Q29=makeQuery(id+"F0.imprint","IMPRINT",FACE,{"disambiguationData":[TD([[makeQuery(id+"F0.imprint","IMPRINT",EDGE,{"derivedFrom":subQ1}),1.0]])]});}
            var Q30;
            {var subQ0=sQuery(id+"F0.wireOp",EDGE,"E101");Q30=makeQuery(id+"F0.imprint","IMPRINT",FACE,{"disambiguationData":[TD([[makeQuery(id+"F0.imprint","IMPRINT",EDGE,{"derivedFrom":subQ0}),1.0]])]});}
            var Q31;
            {var subQ0=sQuery(id+"F0.wireOp",EDGE,"E111");Q31=makeQuery(id+"F0.imprint","IMPRINT",FACE,{"disambiguationData":[TD([[makeQuery(id+"F0.imprint","IMPRINT",EDGE,{"derivedFrom":subQ0}),1.0]])]});}
            var Q32;
            Q32=makeQuery(id+"F0.imprint","IMPRINT",FACE,{"disambiguationData":[TD([[makeQuery(id+"F0.imprint","IMPRINT",EDGE,{"derivedFrom":sQuery(id+"F0.wireOp",EDGE,"E96")}),1.0]])]});
            var Q33;
            Q33=makeQuery(id+"F0.imprint","IMPRINT",FACE,{"disambiguationData":[TD([[makeQuery(id+"F0.imprint","IMPRINT",EDGE,{"derivedFrom":sQuery(id+"F0.wireOp",EDGE,"E156")}),1.0]])]});
            var Q34;
            {var subQ0=sQuery(id+"F0.wireOp",EDGE,"E161");Q34=makeQuery(id+"F0.imprint","IMPRINT",FACE,{"disambiguationData":[TD([[makeQuery(id+"F0.imprint","IMPRINT",EDGE,{"derivedFrom":subQ0}),1.0]])]});}
            var Q35;
            {var subQ0=sQuery(id+"F0.wireOp",EDGE,"E165");Q35=makeQuery(id+"F0.imprint","IMPRINT",FACE,{"disambiguationData":[TD([[makeQuery(id+"F0.imprint","IMPRINT",EDGE,{"derivedFrom":subQ0}),1.0]])]});}
            var Q36;
            {var subQ0=sQuery(id+"F0.wireOp",EDGE,"E171");Q36=makeQuery(id+"F0.imprint","IMPRINT",FACE,{"disambiguationData":[TD([[makeQuery(id+"F0.imprint","IMPRINT",EDGE,{"derivedFrom":subQ0}),1.0]])]});}
            var Q37;
            Q37=makeQuery(id+"F0.imprint","IMPRINT",FACE,{"disambiguationData":[TD([[makeQuery(id+"F0.imprint","IMPRINT",EDGE,{"derivedFrom":sQuery(id+"F0.wireOp",EDGE,"E4")}),1.0]])]});
            var Q38;
            {var subQ2=sQuery(id+"F0.wireOp",EDGE,"E16");Q38=makeQuery(id+"F0.imprint","IMPRINT",FACE,{"disambiguationData":[TD([[makeQuery(id+"F0.imprint","IMPRINT",EDGE,{"derivedFrom":subQ2}),1.0]])]});}
            var Q39;
            Q39=makeQuery(id+"F0.imprint","IMPRINT",FACE,{"disambiguationData":[TD([[makeQuery(id+"F0.imprint","IMPRINT",EDGE,{"derivedFrom":sQuery(id+"F0.wireOp",EDGE,"E176")}),1.0]])]});
            var Q40;
            {var subQ0=sQuery(id+"F0.wireOp",EDGE,"E181");Q40=makeQuery(id+"F0.imprint","IMPRINT",FACE,{"disambiguationData":[TD([[makeQuery(id+"F0.imprint","IMPRINT",EDGE,{"derivedFrom":subQ0}),1.0]])]});}
            var Q41;
            {var subQ3=sQuery(id+"F0.wireOp",EDGE,"E185");Q41=makeQuery(id+"F0.imprint","IMPRINT",FACE,{"disambiguationData":[TD([[makeQuery(id+"F0.imprint","IMPRINT",EDGE,{"derivedFrom":subQ3}),1.0]])]});}
            var Q42;
            {var subQ0=sQuery(id+"F0.wireOp",EDGE,"E191");Q42=makeQuery(id+"F0.imprint","IMPRINT",FACE,{"disambiguationData":[TD([[makeQuery(id+"F0.imprint","IMPRINT",EDGE,{"derivedFrom":subQ0}),1.0]])]});}
            var Q43;
            {var subQ0=sQuery(id+"F0.wireOp",EDGE,"E205");Q43=makeQuery(id+"F0.imprint","IMPRINT",FACE,{"disambiguationData":[TD([[makeQuery(id+"F0.imprint","IMPRINT",EDGE,{"derivedFrom":subQ0}),1.0]])]});}
            var Q44;
            {var subQ0=sQuery(id+"F0.wireOp",EDGE,"E211");Q44=makeQuery(id+"F0.imprint","IMPRINT",FACE,{"disambiguationData":[TD([[makeQuery(id+"F0.imprint","IMPRINT",EDGE,{"derivedFrom":subQ0}),1.0]])]});}
            var Q45;
            {var subQ0=sQuery(id+"F0.wireOp",EDGE,"E201");Q45=makeQuery(id+"F0.imprint","IMPRINT",FACE,{"disambiguationData":[TD([[makeQuery(id+"F0.imprint","IMPRINT",EDGE,{"derivedFrom":subQ0}),1.0]])]});}
            var Q46;
            Q46=makeQuery(id+"F0.imprint","IMPRINT",FACE,{"disambiguationData":[TD([[makeQuery(id+"F0.imprint","IMPRINT",EDGE,{"derivedFrom":sQuery(id+"F0.wireOp",EDGE,"E196")}),1.0]])]});
            var Q47;
            Q47=makeQuery(id+"F0.imprint","IMPRINT",FACE,{"disambiguationData":[TD([[makeQuery(id+"F0.imprint","IMPRINT",EDGE,{"derivedFrom":sQuery(id+"F0.wireOp",EDGE,"E296")}),1.0]])]});
            var Q48;
            {var subQ0=sQuery(id+"F0.wireOp",EDGE,"E311");Q48=makeQuery(id+"F0.imprint","IMPRINT",FACE,{"disambiguationData":[TD([[makeQuery(id+"F0.imprint","IMPRINT",EDGE,{"derivedFrom":subQ0}),1.0]])]});}
            var Q49;
            {var subQ0=sQuery(id+"F0.wireOp",EDGE,"E301");Q49=makeQuery(id+"F0.imprint","IMPRINT",FACE,{"disambiguationData":[TD([[makeQuery(id+"F0.imprint","IMPRINT",EDGE,{"derivedFrom":subQ0}),1.0]])]});}
            var Q50;
            {var subQ1=sQuery(id+"F0.wireOp",EDGE,"E305");Q50=makeQuery(id+"F0.imprint","IMPRINT",FACE,{"disambiguationData":[TD([[makeQuery(id+"F0.imprint","IMPRINT",EDGE,{"derivedFrom":subQ1}),1.0]])]});}
            var Q51;
            Q51=makeQuery(id+"F0.imprint","IMPRINT",FACE,{"disambiguationData":[TD([[makeQuery(id+"F0.imprint","IMPRINT",EDGE,{"derivedFrom":sQuery(id+"F0.wireOp",EDGE,"E276")}),1.0]])]});
            var Q52;
            {var subQ0=sQuery(id+"F0.wireOp",EDGE,"E281");Q52=makeQuery(id+"F0.imprint","IMPRINT",FACE,{"disambiguationData":[TD([[makeQuery(id+"F0.imprint","IMPRINT",EDGE,{"derivedFrom":subQ0}),1.0]])]});}
            var Q53;
            {var subQ3=sQuery(id+"F0.wireOp",EDGE,"E285");Q53=makeQuery(id+"F0.imprint","IMPRINT",FACE,{"disambiguationData":[TD([[makeQuery(id+"F0.imprint","IMPRINT",EDGE,{"derivedFrom":subQ3}),1.0]])]});}
            var Q54;
            {var subQ0=sQuery(id+"F0.wireOp",EDGE,"E291");Q54=makeQuery(id+"F0.imprint","IMPRINT",FACE,{"disambiguationData":[TD([[makeQuery(id+"F0.imprint","IMPRINT",EDGE,{"derivedFrom":subQ0}),1.0]])]});}
            var Q55;
            Q55=makeQuery(id+"F0.imprint","IMPRINT",FACE,{"disambiguationData":[TD([[makeQuery(id+"F0.imprint","IMPRINT",EDGE,{"derivedFrom":sQuery(id+"F0.wireOp",EDGE,"E396")}),1.0]])]});
            var Q56;
            {var subQ0=sQuery(id+"F0.wireOp",EDGE,"E401");Q56=makeQuery(id+"F0.imprint","IMPRINT",FACE,{"disambiguationData":[TD([[makeQuery(id+"F0.imprint","IMPRINT",EDGE,{"derivedFrom":subQ0}),1.0]])]});}
            var Q57;
            {var subQ0=sQuery(id+"F0.wireOp",EDGE,"E405");Q57=makeQuery(id+"F0.imprint","IMPRINT",FACE,{"disambiguationData":[TD([[makeQuery(id+"F0.imprint","IMPRINT",EDGE,{"derivedFrom":subQ0}),1.0]])]});}
            var Q58;
            {var subQ0=sQuery(id+"F0.wireOp",EDGE,"E411");Q58=makeQuery(id+"F0.imprint","IMPRINT",FACE,{"disambiguationData":[TD([[makeQuery(id+"F0.imprint","IMPRINT",EDGE,{"derivedFrom":subQ0}),1.0]])]});}
            var Q59;
            Q59=makeQuery(id+"F0.imprint","IMPRINT",FACE,{"disambiguationData":[TD([[makeQuery(id+"F0.imprint","IMPRINT",EDGE,{"derivedFrom":sQuery(id+"F0.wireOp",EDGE,"E376")}),1.0]])]});
            var Q60;
            {var subQ0=sQuery(id+"F0.wireOp",EDGE,"E391");Q60=makeQuery(id+"F0.imprint","IMPRINT",FACE,{"disambiguationData":[TD([[makeQuery(id+"F0.imprint","IMPRINT",EDGE,{"derivedFrom":subQ0}),1.0]])]});}
            var Q61;
            {var subQ0=sQuery(id+"F0.wireOp",EDGE,"E381");Q61=makeQuery(id+"F0.imprint","IMPRINT",FACE,{"disambiguationData":[TD([[makeQuery(id+"F0.imprint","IMPRINT",EDGE,{"derivedFrom":subQ0}),1.0]])]});}
            var Q62;
            {var subQ1=sQuery(id+"F0.wireOp",EDGE,"E385");Q62=makeQuery(id+"F0.imprint","IMPRINT",FACE,{"disambiguationData":[TD([[makeQuery(id+"F0.imprint","IMPRINT",EDGE,{"derivedFrom":subQ1}),1.0]])]});}
            var Q63;
            Q63=makeQuery(id+"F0.imprint","IMPRINT",FACE,{"disambiguationData":[TD([[makeQuery(id+"F0.imprint","IMPRINT",EDGE,{"derivedFrom":sQuery(id+"F0.wireOp",EDGE,"E496")}),1.0]])]});
            var Q64;
            {var subQ0=sQuery(id+"F0.wireOp",EDGE,"E511");Q64=makeQuery(id+"F0.imprint","IMPRINT",FACE,{"disambiguationData":[TD([[makeQuery(id+"F0.imprint","IMPRINT",EDGE,{"derivedFrom":subQ0}),1.0]])]});}
            var Q65;
            {var subQ0=sQuery(id+"F0.wireOp",EDGE,"E501");Q65=makeQuery(id+"F0.imprint","IMPRINT",FACE,{"disambiguationData":[TD([[makeQuery(id+"F0.imprint","IMPRINT",EDGE,{"derivedFrom":subQ0}),1.0]])]});}
            var Q66;
            {var subQ0=sQuery(id+"F0.wireOp",EDGE,"E505");Q66=makeQuery(id+"F0.imprint","IMPRINT",FACE,{"disambiguationData":[TD([[makeQuery(id+"F0.imprint","IMPRINT",EDGE,{"derivedFrom":subQ0}),1.0]])]});}
            var Q67;
            Q67=makeQuery(id+"F0.imprint","IMPRINT",FACE,{"disambiguationData":[TD([[makeQuery(id+"F0.imprint","IMPRINT",EDGE,{"derivedFrom":sQuery(id+"F0.wireOp",EDGE,"E476")}),1.0]])]});
            var Q68;
            {var subQ0=sQuery(id+"F0.wireOp",EDGE,"E481");Q68=makeQuery(id+"F0.imprint","IMPRINT",FACE,{"disambiguationData":[TD([[makeQuery(id+"F0.imprint","IMPRINT",EDGE,{"derivedFrom":subQ0}),1.0]])]});}
            var Q69;
            {var subQ0=sQuery(id+"F0.wireOp",EDGE,"E491");Q69=makeQuery(id+"F0.imprint","IMPRINT",FACE,{"disambiguationData":[TD([[makeQuery(id+"F0.imprint","IMPRINT",EDGE,{"derivedFrom":subQ0}),1.0]])]});}
            var Q70;
            {var subQ1=sQuery(id+"F0.wireOp",EDGE,"E485");Q70=makeQuery(id+"F0.imprint","IMPRINT",FACE,{"disambiguationData":[TD([[makeQuery(id+"F0.imprint","IMPRINT",EDGE,{"derivedFrom":subQ1}),1.0]])]});}
            var Q71;
            Q71=makeQuery(id+"F0.imprint","IMPRINT",FACE,{"disambiguationData":[TD([[makeQuery(id+"F0.imprint","IMPRINT",EDGE,{"derivedFrom":sQuery(id+"F0.wireOp",EDGE,"E456")}),1.0]])]});
            var Q72;
            {var subQ0=sQuery(id+"F0.wireOp",EDGE,"E471");Q72=makeQuery(id+"F0.imprint","IMPRINT",FACE,{"disambiguationData":[TD([[makeQuery(id+"F0.imprint","IMPRINT",EDGE,{"derivedFrom":subQ0}),1.0]])]});}
            var Q73;
            {var subQ0=sQuery(id+"F0.wireOp",EDGE,"E461");Q73=makeQuery(id+"F0.imprint","IMPRINT",FACE,{"disambiguationData":[TD([[makeQuery(id+"F0.imprint","IMPRINT",EDGE,{"derivedFrom":subQ0}),1.0]])]});}
            var Q74;
            {var subQ3=sQuery(id+"F0.wireOp",EDGE,"E465");Q74=makeQuery(id+"F0.imprint","IMPRINT",FACE,{"disambiguationData":[TD([[makeQuery(id+"F0.imprint","IMPRINT",EDGE,{"derivedFrom":subQ3}),1.0]])]});}
            var Q75;
            Q75=makeQuery(id+"F0.imprint","IMPRINT",FACE,{"disambiguationData":[TD([[makeQuery(id+"F0.imprint","IMPRINT",EDGE,{"derivedFrom":sQuery(id+"F0.wireOp",EDGE,"E356")}),1.0]])]});
            var Q76;
            {var subQ0=sQuery(id+"F0.wireOp",EDGE,"E371");Q76=makeQuery(id+"F0.imprint","IMPRINT",FACE,{"disambiguationData":[TD([[makeQuery(id+"F0.imprint","IMPRINT",EDGE,{"derivedFrom":subQ0}),1.0]])]});}
            var Q77;
            {var subQ0=sQuery(id+"F0.wireOp",EDGE,"E361");Q77=makeQuery(id+"F0.imprint","IMPRINT",FACE,{"disambiguationData":[TD([[makeQuery(id+"F0.imprint","IMPRINT",EDGE,{"derivedFrom":subQ0}),1.0]])]});}
            var Q78;
            {var subQ1=sQuery(id+"F0.wireOp",EDGE,"E365");Q78=makeQuery(id+"F0.imprint","IMPRINT",FACE,{"disambiguationData":[TD([[makeQuery(id+"F0.imprint","IMPRINT",EDGE,{"derivedFrom":subQ1}),1.0]])]});}
            var Q79;
            Q79=makeQuery(id+"F0.imprint","IMPRINT",FACE,{"disambiguationData":[TD([[makeQuery(id+"F0.imprint","IMPRINT",EDGE,{"derivedFrom":sQuery(id+"F0.wireOp",EDGE,"E336")}),1.0]])]});
            var Q80;
            {var subQ0=sQuery(id+"F0.wireOp",EDGE,"E341");Q80=makeQuery(id+"F0.imprint","IMPRINT",FACE,{"disambiguationData":[TD([[makeQuery(id+"F0.imprint","IMPRINT",EDGE,{"derivedFrom":subQ0}),1.0]])]});}
            var Q81;
            {var subQ0=sQuery(id+"F0.wireOp",EDGE,"E345");Q81=makeQuery(id+"F0.imprint","IMPRINT",FACE,{"disambiguationData":[TD([[makeQuery(id+"F0.imprint","IMPRINT",EDGE,{"derivedFrom":subQ0}),1.0]])]});}
            var Q82;
            {var subQ0=sQuery(id+"F0.wireOp",EDGE,"E351");Q82=makeQuery(id+"F0.imprint","IMPRINT",FACE,{"disambiguationData":[TD([[makeQuery(id+"F0.imprint","IMPRINT",EDGE,{"derivedFrom":subQ0}),1.0]])]});}
            var Q83;
            Q83=makeQuery(id+"F0.imprint","IMPRINT",FACE,{"disambiguationData":[TD([[makeQuery(id+"F0.imprint","IMPRINT",EDGE,{"derivedFrom":sQuery(id+"F0.wireOp",EDGE,"E436")}),1.0]])]});
            var Q84;
            {var subQ0=sQuery(id+"F0.wireOp",EDGE,"E441");Q84=makeQuery(id+"F0.imprint","IMPRINT",FACE,{"disambiguationData":[TD([[makeQuery(id+"F0.imprint","IMPRINT",EDGE,{"derivedFrom":subQ0}),1.0]])]});}
            var Q85;
            {var subQ0=sQuery(id+"F0.wireOp",EDGE,"E451");Q85=makeQuery(id+"F0.imprint","IMPRINT",FACE,{"disambiguationData":[TD([[makeQuery(id+"F0.imprint","IMPRINT",EDGE,{"derivedFrom":subQ0}),1.0]])]});}
            var Q86;
            {var subQ3=sQuery(id+"F0.wireOp",EDGE,"E445");Q86=makeQuery(id+"F0.imprint","IMPRINT",FACE,{"disambiguationData":[TD([[makeQuery(id+"F0.imprint","IMPRINT",EDGE,{"derivedFrom":subQ3}),1.0]])]});}
            var Q87;
            Q87=makeQuery(id+"F0.imprint","IMPRINT",FACE,{"disambiguationData":[TD([[makeQuery(id+"F0.imprint","IMPRINT",EDGE,{"derivedFrom":sQuery(id+"F0.wireOp",EDGE,"E416")}),1.0]])]});
            var Q88;
            {var subQ0=sQuery(id+"F0.wireOp",EDGE,"E431");Q88=makeQuery(id+"F0.imprint","IMPRINT",FACE,{"disambiguationData":[TD([[makeQuery(id+"F0.imprint","IMPRINT",EDGE,{"derivedFrom":subQ0}),1.0]])]});}
            var Q89;
            {var subQ0=sQuery(id+"F0.wireOp",EDGE,"E421");Q89=makeQuery(id+"F0.imprint","IMPRINT",FACE,{"disambiguationData":[TD([[makeQuery(id+"F0.imprint","IMPRINT",EDGE,{"derivedFrom":subQ0}),1.0]])]});}
            var Q90;
            {var subQ0=sQuery(id+"F0.wireOp",EDGE,"E425");Q90=makeQuery(id+"F0.imprint","IMPRINT",FACE,{"disambiguationData":[TD([[makeQuery(id+"F0.imprint","IMPRINT",EDGE,{"derivedFrom":subQ0}),1.0]])]});}
            var Q91;
            {var subQ1=sQuery(id+"F0.wireOp",EDGE,"E325");Q91=makeQuery(id+"F0.imprint","IMPRINT",FACE,{"disambiguationData":[TD([[makeQuery(id+"F0.imprint","IMPRINT",EDGE,{"derivedFrom":subQ1}),1.0]])]});}
            var Q92;
            {var subQ0=sQuery(id+"F0.wireOp",EDGE,"E331");Q92=makeQuery(id+"F0.imprint","IMPRINT",FACE,{"disambiguationData":[TD([[makeQuery(id+"F0.imprint","IMPRINT",EDGE,{"derivedFrom":subQ0}),1.0]])]});}
            var Q93;
            {var subQ0=sQuery(id+"F0.wireOp",EDGE,"E321");Q93=makeQuery(id+"F0.imprint","IMPRINT",FACE,{"disambiguationData":[TD([[makeQuery(id+"F0.imprint","IMPRINT",EDGE,{"derivedFrom":subQ0}),1.0]])]});}
            var Q94;
            Q94=makeQuery(id+"F0.imprint","IMPRINT",FACE,{"disambiguationData":[TD([[makeQuery(id+"F0.imprint","IMPRINT",EDGE,{"derivedFrom":sQuery(id+"F0.wireOp",EDGE,"E316")}),1.0]])]});
            var Q95;
            {var subQ3=sQuery(id+"F0.wireOp",EDGE,"E525");Q95=makeQuery(id+"F0.imprint","IMPRINT",FACE,{"disambiguationData":[TD([[makeQuery(id+"F0.imprint","IMPRINT",EDGE,{"derivedFrom":subQ3}),1.0]])]});}
            var Q96;
            {var subQ0=sQuery(id+"F0.wireOp",EDGE,"E521");Q96=makeQuery(id+"F0.imprint","IMPRINT",FACE,{"disambiguationData":[TD([[makeQuery(id+"F0.imprint","IMPRINT",EDGE,{"derivedFrom":subQ0}),1.0]])]});}
            var Q97;
            Q97=makeQuery(id+"F0.imprint","IMPRINT",FACE,{"disambiguationData":[TD([[makeQuery(id+"F0.imprint","IMPRINT",EDGE,{"derivedFrom":sQuery(id+"F0.wireOp",EDGE,"E516")}),1.0]])]});
            var Q98;
            {var subQ0=sQuery(id+"F0.wireOp",EDGE,"E531");Q98=makeQuery(id+"F0.imprint","IMPRINT",FACE,{"disambiguationData":[TD([[makeQuery(id+"F0.imprint","IMPRINT",EDGE,{"derivedFrom":subQ0}),1.0]])]});}
            var Q99;
            {var subQ0=sQuery(id+"F0.wireOp",EDGE,"E621");Q99=makeQuery(id+"F0.imprint","IMPRINT",FACE,{"disambiguationData":[TD([[makeQuery(id+"F0.imprint","IMPRINT",EDGE,{"derivedFrom":subQ0}),1.0]])]});}
            var Q100;
            {var subQ0=sQuery(id+"F0.wireOp",EDGE,"E625");Q100=makeQuery(id+"F0.imprint","IMPRINT",FACE,{"disambiguationData":[TD([[makeQuery(id+"F0.imprint","IMPRINT",EDGE,{"derivedFrom":subQ0}),1.0]])]});}
            var Q101;
            {var subQ0=sQuery(id+"F0.wireOp",EDGE,"E631");Q101=makeQuery(id+"F0.imprint","IMPRINT",FACE,{"disambiguationData":[TD([[makeQuery(id+"F0.imprint","IMPRINT",EDGE,{"derivedFrom":subQ0}),1.0]])]});}
            var Q102;
            Q102=makeQuery(id+"F0.imprint","IMPRINT",FACE,{"disambiguationData":[TD([[makeQuery(id+"F0.imprint","IMPRINT",EDGE,{"derivedFrom":sQuery(id+"F0.wireOp",EDGE,"E616")}),1.0]])]});
            var Q103;
            Q103=makeQuery(id+"F0.imprint","IMPRINT",FACE,{"disambiguationData":[TD([[makeQuery(id+"F0.imprint","IMPRINT",EDGE,{"derivedFrom":sQuery(id+"F0.wireOp",EDGE,"E716")}),1.0]])]});
            var Q104;
            {var subQ0=sQuery(id+"F0.wireOp",EDGE,"E721");Q104=makeQuery(id+"F0.imprint","IMPRINT",FACE,{"disambiguationData":[TD([[makeQuery(id+"F0.imprint","IMPRINT",EDGE,{"derivedFrom":subQ0}),1.0]])]});}
            var Q105;
            {var subQ1=sQuery(id+"F0.wireOp",EDGE,"E725");Q105=makeQuery(id+"F0.imprint","IMPRINT",FACE,{"disambiguationData":[TD([[makeQuery(id+"F0.imprint","IMPRINT",EDGE,{"derivedFrom":subQ1}),1.0]])]});}
            var Q106;
            {var subQ0=sQuery(id+"F0.wireOp",EDGE,"E731");Q106=makeQuery(id+"F0.imprint","IMPRINT",FACE,{"disambiguationData":[TD([[makeQuery(id+"F0.imprint","IMPRINT",EDGE,{"derivedFrom":subQ0}),1.0]])]});}
            var Q107;
            {var subQ0=sQuery(id+"F0.wireOp",EDGE,"E853");Q107=makeQuery(id+"F0.imprint","IMPRINT",FACE,{"disambiguationData":[TD([[makeQuery(id+"F0.imprint","IMPRINT",EDGE,{"derivedFrom":subQ0}),1.0]])]});}
            var Q108;
            {var subQ1=sQuery(id+"F0.wireOp",EDGE,"E857");Q108=makeQuery(id+"F0.imprint","IMPRINT",FACE,{"disambiguationData":[TD([[makeQuery(id+"F0.imprint","IMPRINT",EDGE,{"derivedFrom":subQ1}),1.0]])]});}
            var Q109;
            {var subQ0=sQuery(id+"F0.wireOp",EDGE,"E863");Q109=makeQuery(id+"F0.imprint","IMPRINT",FACE,{"disambiguationData":[TD([[makeQuery(id+"F0.imprint","IMPRINT",EDGE,{"derivedFrom":subQ0}),1.0]])]});}
            var Q110;
            Q110=makeQuery(id+"F0.imprint","IMPRINT",FACE,{"disambiguationData":[TD([[makeQuery(id+"F0.imprint","IMPRINT",EDGE,{"derivedFrom":sQuery(id+"F0.wireOp",EDGE,"E848")}),1.0]])]});
            var Q111;
            {var subQ3=sQuery(id+"F0.wireOp",EDGE,"E877");Q111=makeQuery(id+"F0.imprint","IMPRINT",FACE,{"disambiguationData":[TD([[makeQuery(id+"F0.imprint","IMPRINT",EDGE,{"derivedFrom":subQ3}),1.0]])]});}
            var Q112;
            {var subQ0=sQuery(id+"F0.wireOp",EDGE,"E883");Q112=makeQuery(id+"F0.imprint","IMPRINT",FACE,{"disambiguationData":[TD([[makeQuery(id+"F0.imprint","IMPRINT",EDGE,{"derivedFrom":subQ0}),1.0]])]});}
            var Q113;
            Q113=makeQuery(id+"F0.imprint","IMPRINT",FACE,{"disambiguationData":[TD([[makeQuery(id+"F0.imprint","IMPRINT",EDGE,{"derivedFrom":sQuery(id+"F0.wireOp",EDGE,"E868")}),1.0]])]});
            var Q114;
            {var subQ0=sQuery(id+"F0.wireOp",EDGE,"E873");Q114=makeQuery(id+"F0.imprint","IMPRINT",FACE,{"disambiguationData":[TD([[makeQuery(id+"F0.imprint","IMPRINT",EDGE,{"derivedFrom":subQ0}),1.0]])]});}
            var Q115;
            {var subQ1=sQuery(id+"F0.wireOp",EDGE,"E897");Q115=makeQuery(id+"F0.imprint","IMPRINT",FACE,{"disambiguationData":[TD([[makeQuery(id+"F0.imprint","IMPRINT",EDGE,{"derivedFrom":subQ1}),1.0]])]});}
            var Q116;
            {var subQ0=sQuery(id+"F0.wireOp",EDGE,"E893");Q116=makeQuery(id+"F0.imprint","IMPRINT",FACE,{"disambiguationData":[TD([[makeQuery(id+"F0.imprint","IMPRINT",EDGE,{"derivedFrom":subQ0}),1.0]])]});}
            var Q117;
            Q117=makeQuery(id+"F0.imprint","IMPRINT",FACE,{"disambiguationData":[TD([[makeQuery(id+"F0.imprint","IMPRINT",EDGE,{"derivedFrom":sQuery(id+"F0.wireOp",EDGE,"E888")}),1.0]])]});
            var Q118;
            {var subQ0=sQuery(id+"F0.wireOp",EDGE,"E903");Q118=makeQuery(id+"F0.imprint","IMPRINT",FACE,{"disambiguationData":[TD([[makeQuery(id+"F0.imprint","IMPRINT",EDGE,{"derivedFrom":subQ0}),1.0]])]});}
            var Q119;
            {var subQ0=sQuery(id+"F0.wireOp",EDGE,"E751");Q119=makeQuery(id+"F0.imprint","IMPRINT",FACE,{"disambiguationData":[TD([[makeQuery(id+"F0.imprint","IMPRINT",EDGE,{"derivedFrom":subQ0}),1.0]])]});}
            var Q120;
            {var subQ3=sQuery(id+"F0.wireOp",EDGE,"E745");Q120=makeQuery(id+"F0.imprint","IMPRINT",FACE,{"disambiguationData":[TD([[makeQuery(id+"F0.imprint","IMPRINT",EDGE,{"derivedFrom":subQ3}),1.0]])]});}
            var Q121;
            {var subQ0=sQuery(id+"F0.wireOp",EDGE,"E741");Q121=makeQuery(id+"F0.imprint","IMPRINT",FACE,{"disambiguationData":[TD([[makeQuery(id+"F0.imprint","IMPRINT",EDGE,{"derivedFrom":subQ0}),1.0]])]});}
            var Q122;
            Q122=makeQuery(id+"F0.imprint","IMPRINT",FACE,{"disambiguationData":[TD([[makeQuery(id+"F0.imprint","IMPRINT",EDGE,{"derivedFrom":sQuery(id+"F0.wireOp",EDGE,"E736")}),1.0]])]});
            var Q123;
            {var subQ2=sQuery(id+"F0.wireOp",EDGE,"E765");Q123=makeQuery(id+"F0.imprint","IMPRINT",FACE,{"disambiguationData":[TD([[makeQuery(id+"F0.imprint","IMPRINT",EDGE,{"derivedFrom":subQ2}),1.0]])]});}
            var Q124;
            {var subQ0=sQuery(id+"F0.wireOp",EDGE,"E761");Q124=makeQuery(id+"F0.imprint","IMPRINT",FACE,{"disambiguationData":[TD([[makeQuery(id+"F0.imprint","IMPRINT",EDGE,{"derivedFrom":subQ0}),1.0]])]});}
            var Q125;
            Q125=makeQuery(id+"F0.imprint","IMPRINT",FACE,{"disambiguationData":[TD([[makeQuery(id+"F0.imprint","IMPRINT",EDGE,{"derivedFrom":sQuery(id+"F0.wireOp",EDGE,"E756")}),1.0]])]});
            var Q126;
            {var subQ0=sQuery(id+"F0.wireOp",EDGE,"E771");Q126=makeQuery(id+"F0.imprint","IMPRINT",FACE,{"disambiguationData":[TD([[makeQuery(id+"F0.imprint","IMPRINT",EDGE,{"derivedFrom":subQ0}),1.0]])]});}
            var Q127;
            {var subQ0=sQuery(id+"F0.wireOp",EDGE,"E665");Q127=makeQuery(id+"F0.imprint","IMPRINT",FACE,{"disambiguationData":[TD([[makeQuery(id+"F0.imprint","IMPRINT",EDGE,{"derivedFrom":subQ0}),1.0]])]});}
            var Q128;
            {var subQ0=sQuery(id+"F0.wireOp",EDGE,"E671");Q128=makeQuery(id+"F0.imprint","IMPRINT",FACE,{"disambiguationData":[TD([[makeQuery(id+"F0.imprint","IMPRINT",EDGE,{"derivedFrom":subQ0}),1.0]])]});}
            var Q129;
            {var subQ0=sQuery(id+"F0.wireOp",EDGE,"E661");Q129=makeQuery(id+"F0.imprint","IMPRINT",FACE,{"disambiguationData":[TD([[makeQuery(id+"F0.imprint","IMPRINT",EDGE,{"derivedFrom":subQ0}),1.0]])]});}
            var Q130;
            Q130=makeQuery(id+"F0.imprint","IMPRINT",FACE,{"disambiguationData":[TD([[makeQuery(id+"F0.imprint","IMPRINT",EDGE,{"derivedFrom":sQuery(id+"F0.wireOp",EDGE,"E656")}),1.0]])]});
            var Q131;
            Q131=makeQuery(id+"F0.imprint","IMPRINT",FACE,{"disambiguationData":[TD([[makeQuery(id+"F0.imprint","IMPRINT",EDGE,{"derivedFrom":sQuery(id+"F0.wireOp",EDGE,"E636")}),1.0]])]});
            var Q132;
            {var subQ0=sQuery(id+"F0.wireOp",EDGE,"E641");Q132=makeQuery(id+"F0.imprint","IMPRINT",FACE,{"disambiguationData":[TD([[makeQuery(id+"F0.imprint","IMPRINT",EDGE,{"derivedFrom":subQ0}),1.0]])]});}
            var Q133;
            {var subQ1=sQuery(id+"F0.wireOp",EDGE,"E645");Q133=makeQuery(id+"F0.imprint","IMPRINT",FACE,{"disambiguationData":[TD([[makeQuery(id+"F0.imprint","IMPRINT",EDGE,{"derivedFrom":subQ1}),1.0]])]});}
            var Q134;
            {var subQ0=sQuery(id+"F0.wireOp",EDGE,"E651");Q134=makeQuery(id+"F0.imprint","IMPRINT",FACE,{"disambiguationData":[TD([[makeQuery(id+"F0.imprint","IMPRINT",EDGE,{"derivedFrom":subQ0}),1.0]])]});}
            var Q135;
            {var subQ0=sQuery(id+"F0.wireOp",EDGE,"E545");Q135=makeQuery(id+"F0.imprint","IMPRINT",FACE,{"disambiguationData":[TD([[makeQuery(id+"F0.imprint","IMPRINT",EDGE,{"derivedFrom":subQ0}),1.0]])]});}
            var Q136;
            {var subQ0=sQuery(id+"F0.wireOp",EDGE,"E541");Q136=makeQuery(id+"F0.imprint","IMPRINT",FACE,{"disambiguationData":[TD([[makeQuery(id+"F0.imprint","IMPRINT",EDGE,{"derivedFrom":subQ0}),1.0]])]});}
            var Q137;
            Q137=makeQuery(id+"F0.imprint","IMPRINT",FACE,{"disambiguationData":[TD([[makeQuery(id+"F0.imprint","IMPRINT",EDGE,{"derivedFrom":sQuery(id+"F0.wireOp",EDGE,"E536")}),1.0]])]});
            var Q138;
            {var subQ0=sQuery(id+"F0.wireOp",EDGE,"E551");Q138=makeQuery(id+"F0.imprint","IMPRINT",FACE,{"disambiguationData":[TD([[makeQuery(id+"F0.imprint","IMPRINT",EDGE,{"derivedFrom":subQ0}),1.0]])]});}
            var Q139;
            {var subQ1=sQuery(id+"F0.wireOp",EDGE,"E565");Q139=makeQuery(id+"F0.imprint","IMPRINT",FACE,{"disambiguationData":[TD([[makeQuery(id+"F0.imprint","IMPRINT",EDGE,{"derivedFrom":subQ1}),1.0]])]});}
            var Q140;
            {var subQ0=sQuery(id+"F0.wireOp",EDGE,"E561");Q140=makeQuery(id+"F0.imprint","IMPRINT",FACE,{"disambiguationData":[TD([[makeQuery(id+"F0.imprint","IMPRINT",EDGE,{"derivedFrom":subQ0}),1.0]])]});}
            var Q141;
            Q141=makeQuery(id+"F0.imprint","IMPRINT",FACE,{"disambiguationData":[TD([[makeQuery(id+"F0.imprint","IMPRINT",EDGE,{"derivedFrom":sQuery(id+"F0.wireOp",EDGE,"E556")}),1.0]])]});
            var Q142;
            {var subQ0=sQuery(id+"F0.wireOp",EDGE,"E571");Q142=makeQuery(id+"F0.imprint","IMPRINT",FACE,{"disambiguationData":[TD([[makeQuery(id+"F0.imprint","IMPRINT",EDGE,{"derivedFrom":subQ0}),1.0]])]});}
            var Q143;
            {var subQ0=sQuery(id+"F0.wireOp",EDGE,"E585");Q143=makeQuery(id+"F0.imprint","IMPRINT",FACE,{"disambiguationData":[TD([[makeQuery(id+"F0.imprint","IMPRINT",EDGE,{"derivedFrom":subQ0}),1.0]])]});}
            var Q144;
            {var subQ0=sQuery(id+"F0.wireOp",EDGE,"E591");Q144=makeQuery(id+"F0.imprint","IMPRINT",FACE,{"disambiguationData":[TD([[makeQuery(id+"F0.imprint","IMPRINT",EDGE,{"derivedFrom":subQ0}),1.0]])]});}
            var Q145;
            {var subQ0=sQuery(id+"F0.wireOp",EDGE,"E581");Q145=makeQuery(id+"F0.imprint","IMPRINT",FACE,{"disambiguationData":[TD([[makeQuery(id+"F0.imprint","IMPRINT",EDGE,{"derivedFrom":subQ0}),1.0]])]});}
            var Q146;
            Q146=makeQuery(id+"F0.imprint","IMPRINT",FACE,{"disambiguationData":[TD([[makeQuery(id+"F0.imprint","IMPRINT",EDGE,{"derivedFrom":sQuery(id+"F0.wireOp",EDGE,"E576")}),1.0]])]});
            var Q147;
            {var subQ1=sQuery(id+"F0.wireOp",EDGE,"E605");Q147=makeQuery(id+"F0.imprint","IMPRINT",FACE,{"disambiguationData":[TD([[makeQuery(id+"F0.imprint","IMPRINT",EDGE,{"derivedFrom":subQ1}),1.0]])]});}
            var Q148;
            {var subQ0=sQuery(id+"F0.wireOp",EDGE,"E601");Q148=makeQuery(id+"F0.imprint","IMPRINT",FACE,{"disambiguationData":[TD([[makeQuery(id+"F0.imprint","IMPRINT",EDGE,{"derivedFrom":subQ0}),1.0]])]});}
            var Q149;
            Q149=makeQuery(id+"F0.imprint","IMPRINT",FACE,{"disambiguationData":[TD([[makeQuery(id+"F0.imprint","IMPRINT",EDGE,{"derivedFrom":sQuery(id+"F0.wireOp",EDGE,"E596")}),1.0]])]});
            var Q150;
            {var subQ0=sQuery(id+"F0.wireOp",EDGE,"E611");Q150=makeQuery(id+"F0.imprint","IMPRINT",FACE,{"disambiguationData":[TD([[makeQuery(id+"F0.imprint","IMPRINT",EDGE,{"derivedFrom":subQ0}),1.0]])]});}
            var Q151;
            {var subQ0=sQuery(id+"F0.wireOp",EDGE,"E701");Q151=makeQuery(id+"F0.imprint","IMPRINT",FACE,{"disambiguationData":[TD([[makeQuery(id+"F0.imprint","IMPRINT",EDGE,{"derivedFrom":subQ0}),1.0]])]});}
            var Q152;
            {var subQ3=sQuery(id+"F0.wireOp",EDGE,"E705");Q152=makeQuery(id+"F0.imprint","IMPRINT",FACE,{"disambiguationData":[TD([[makeQuery(id+"F0.imprint","IMPRINT",EDGE,{"derivedFrom":subQ3}),1.0]])]});}
            var Q153;
            Q153=makeQuery(id+"F0.imprint","IMPRINT",FACE,{"disambiguationData":[TD([[makeQuery(id+"F0.imprint","IMPRINT",EDGE,{"derivedFrom":sQuery(id+"F0.wireOp",EDGE,"E696")}),1.0]])]});
            var Q154;
            {var subQ0=sQuery(id+"F0.wireOp",EDGE,"E711");Q154=makeQuery(id+"F0.imprint","IMPRINT",FACE,{"disambiguationData":[TD([[makeQuery(id+"F0.imprint","IMPRINT",EDGE,{"derivedFrom":subQ0}),1.0]])]});}
            var Q155;
            {var subQ0=sQuery(id+"F0.wireOp",EDGE,"E691");Q155=makeQuery(id+"F0.imprint","IMPRINT",FACE,{"disambiguationData":[TD([[makeQuery(id+"F0.imprint","IMPRINT",EDGE,{"derivedFrom":subQ0}),1.0]])]});}
            var Q156;
            {var subQ4=sQuery(id+"F0.wireOp",EDGE,"E685");Q156=makeQuery(id+"F0.imprint","IMPRINT",FACE,{"disambiguationData":[TD([[makeQuery(id+"F0.imprint","IMPRINT",EDGE,{"derivedFrom":subQ4}),1.0]])]});}
            var Q157;
            {var subQ0=sQuery(id+"F0.wireOp",EDGE,"E681");Q157=makeQuery(id+"F0.imprint","IMPRINT",FACE,{"disambiguationData":[TD([[makeQuery(id+"F0.imprint","IMPRINT",EDGE,{"derivedFrom":subQ0}),1.0]])]});}
            var Q158;
            Q158=makeQuery(id+"F0.imprint","IMPRINT",FACE,{"disambiguationData":[TD([[makeQuery(id+"F0.imprint","IMPRINT",EDGE,{"derivedFrom":sQuery(id+"F0.wireOp",EDGE,"E676")}),1.0]])]});
            var Q159;
            {var subQ0=sQuery(id+"F0.wireOp",EDGE,"E781");Q159=makeQuery(id+"F0.imprint","IMPRINT",FACE,{"disambiguationData":[TD([[makeQuery(id+"F0.imprint","IMPRINT",EDGE,{"derivedFrom":subQ0}),1.0]])]});}
            var Q160;
            {var subQ1=sQuery(id+"F0.wireOp",EDGE,"E785");Q160=makeQuery(id+"F0.imprint","IMPRINT",FACE,{"disambiguationData":[TD([[makeQuery(id+"F0.imprint","IMPRINT",EDGE,{"derivedFrom":subQ1}),1.0]])]});}
            var Q161;
            {var subQ0=sQuery(id+"F0.wireOp",EDGE,"E791");Q161=makeQuery(id+"F0.imprint","IMPRINT",FACE,{"disambiguationData":[TD([[makeQuery(id+"F0.imprint","IMPRINT",EDGE,{"derivedFrom":subQ0}),1.0]])]});}
            var Q162;
            Q162=makeQuery(id+"F0.imprint","IMPRINT",FACE,{"disambiguationData":[TD([[makeQuery(id+"F0.imprint","IMPRINT",EDGE,{"derivedFrom":sQuery(id+"F0.wireOp",EDGE,"E776")}),1.0]])]});
            var Q163;
            {var subQ0=sQuery(id+"F0.wireOp",EDGE,"E821");Q163=makeQuery(id+"F0.imprint","IMPRINT",FACE,{"disambiguationData":[TD([[makeQuery(id+"F0.imprint","IMPRINT",EDGE,{"derivedFrom":subQ0}),1.0]])]});}
            var Q164;
            {var subQ2=sQuery(id+"F0.wireOp",EDGE,"E797");Q164=makeQuery(id+"F0.imprint","IMPRINT",FACE,{"disambiguationData":[TD([[makeQuery(id+"F0.imprint","IMPRINT",EDGE,{"derivedFrom":subQ2}),1.0]])]});}
            var Q165;
            {var subQ3=sQuery(id+"F0.wireOp",EDGE,"E917");Q165=makeQuery(id+"F0.imprint","IMPRINT",FACE,{"disambiguationData":[TD([[makeQuery(id+"F0.imprint","IMPRINT",EDGE,{"derivedFrom":subQ3}),1.0]])]});}
            var Q166;
            {var subQ0=sQuery(id+"F0.wireOp",EDGE,"E923");Q166=makeQuery(id+"F0.imprint","IMPRINT",FACE,{"disambiguationData":[TD([[makeQuery(id+"F0.imprint","IMPRINT",EDGE,{"derivedFrom":subQ0}),1.0]])]});}
            var Q167;
            {var subQ0=sQuery(id+"F0.wireOp",EDGE,"E913");Q167=makeQuery(id+"F0.imprint","IMPRINT",FACE,{"disambiguationData":[TD([[makeQuery(id+"F0.imprint","IMPRINT",EDGE,{"derivedFrom":subQ0}),1.0]])]});}
            var Q168;
            Q168=makeQuery(id+"F0.imprint","IMPRINT",FACE,{"disambiguationData":[TD([[makeQuery(id+"F0.imprint","IMPRINT",EDGE,{"derivedFrom":sQuery(id+"F0.wireOp",EDGE,"E908")}),1.0]])]});
            var Q169;
            Q169=makeQuery(id+"F0.imprint","IMPRINT",FACE,{"disambiguationData":[TD([[makeQuery(id+"F0.imprint","IMPRINT",EDGE,{"derivedFrom":sQuery(id+"F0.wireOp",EDGE,"E56")}),-1.0]])]});
            var Q170;
            Q170=makeQuery(id+"F0.imprint","IMPRINT",FACE,{"disambiguationData":[TD([[makeQuery(id+"F0.imprint","IMPRINT",EDGE,{"derivedFrom":sQuery(id+"F0.wireOp",EDGE,"E116")}),-1.0]])]});
            var Q171;
            Q171=makeQuery(id+"F0.imprint","IMPRINT",FACE,{"disambiguationData":[TD([[makeQuery(id+"F0.imprint","IMPRINT",EDGE,{"derivedFrom":sQuery(id+"F0.wireOp",EDGE,"E216")}),-1.0]])]});
            var Q172;
            Q172=makeQuery(id+"F0.imprint","IMPRINT",FACE,{"disambiguationData":[TD([[makeQuery(id+"F0.imprint","IMPRINT",EDGE,{"derivedFrom":sQuery(id+"F0.wireOp",EDGE,"E316")}),-1.0]])]});
            var Q173;
            Q173=makeQuery(id+"F0.imprint","IMPRINT",FACE,{"disambiguationData":[TD([[makeQuery(id+"F0.imprint","IMPRINT",EDGE,{"derivedFrom":sQuery(id+"F0.wireOp",EDGE,"E416")}),-1.0]])]});
            var Q174;
            Q174=makeQuery(id+"F0.imprint","IMPRINT",FACE,{"disambiguationData":[TD([[makeQuery(id+"F0.imprint","IMPRINT",EDGE,{"derivedFrom":sQuery(id+"F0.wireOp",EDGE,"E436")}),-1.0]])]});
            var Q175;
            Q175=makeQuery(id+"F0.imprint","IMPRINT",FACE,{"disambiguationData":[TD([[makeQuery(id+"F0.imprint","IMPRINT",EDGE,{"derivedFrom":sQuery(id+"F0.wireOp",EDGE,"E336")}),-1.0]])]});
            var Q176;
            Q176=makeQuery(id+"F0.imprint","IMPRINT",FACE,{"disambiguationData":[TD([[makeQuery(id+"F0.imprint","IMPRINT",EDGE,{"derivedFrom":sQuery(id+"F0.wireOp",EDGE,"E236")}),-1.0]])]});
            var Q177;
            Q177=makeQuery(id+"F0.imprint","IMPRINT",FACE,{"disambiguationData":[TD([[makeQuery(id+"F0.imprint","IMPRINT",EDGE,{"derivedFrom":sQuery(id+"F0.wireOp",EDGE,"E136")}),-1.0]])]});
            var Q178;
            Q178=makeQuery(id+"F0.imprint","IMPRINT",FACE,{"disambiguationData":[TD([[makeQuery(id+"F0.imprint","IMPRINT",EDGE,{"derivedFrom":sQuery(id+"F0.wireOp",EDGE,"E76")}),-1.0]])]});
            var Q179;
            Q179=makeQuery(id+"F0.imprint","IMPRINT",FACE,{"disambiguationData":[TD([[makeQuery(id+"F0.imprint","IMPRINT",EDGE,{"derivedFrom":sQuery(id+"F0.wireOp",EDGE,"E96")}),-1.0]])]});
            var Q180;
            Q180=makeQuery(id+"F0.imprint","IMPRINT",FACE,{"disambiguationData":[TD([[makeQuery(id+"F0.imprint","IMPRINT",EDGE,{"derivedFrom":sQuery(id+"F0.wireOp",EDGE,"E156")}),-1.0]])]});
            var Q181;
            Q181=makeQuery(id+"F0.imprint","IMPRINT",FACE,{"disambiguationData":[TD([[makeQuery(id+"F0.imprint","IMPRINT",EDGE,{"derivedFrom":sQuery(id+"F0.wireOp",EDGE,"E256")}),-1.0]])]});
            var Q182;
            Q182=makeQuery(id+"F0.imprint","IMPRINT",FACE,{"disambiguationData":[TD([[makeQuery(id+"F0.imprint","IMPRINT",EDGE,{"derivedFrom":sQuery(id+"F0.wireOp",EDGE,"E356")}),-1.0]])]});
            var Q183;
            Q183=makeQuery(id+"F0.imprint","IMPRINT",FACE,{"disambiguationData":[TD([[makeQuery(id+"F0.imprint","IMPRINT",EDGE,{"derivedFrom":sQuery(id+"F0.wireOp",EDGE,"E456")}),-1.0]])]});
            var Q184;
            Q184=makeQuery(id+"F0.imprint","IMPRINT",FACE,{"disambiguationData":[TD([[makeQuery(id+"F0.imprint","IMPRINT",EDGE,{"derivedFrom":sQuery(id+"F0.wireOp",EDGE,"E476")}),-1.0]])]});
            var Q185;
            Q185=makeQuery(id+"F0.imprint","IMPRINT",FACE,{"disambiguationData":[TD([[makeQuery(id+"F0.imprint","IMPRINT",EDGE,{"derivedFrom":sQuery(id+"F0.wireOp",EDGE,"E376")}),-1.0]])]});
            var Q186;
            Q186=makeQuery(id+"F0.imprint","IMPRINT",FACE,{"disambiguationData":[TD([[makeQuery(id+"F0.imprint","IMPRINT",EDGE,{"derivedFrom":sQuery(id+"F0.wireOp",EDGE,"E276")}),-1.0]])]});
            var Q187;
            Q187=makeQuery(id+"F0.imprint","IMPRINT",FACE,{"disambiguationData":[TD([[makeQuery(id+"F0.imprint","IMPRINT",EDGE,{"derivedFrom":sQuery(id+"F0.wireOp",EDGE,"E176")}),-1.0]])]});
            var Q188;
            Q188=makeQuery(id+"F0.imprint","IMPRINT",FACE,{"disambiguationData":[TD([[makeQuery(id+"F0.imprint","IMPRINT",EDGE,{"derivedFrom":sQuery(id+"F0.wireOp",EDGE,"E4")}),-1.0]])]});
            var Q189;
            Q189=makeQuery(id+"F0.imprint","IMPRINT",FACE,{"disambiguationData":[TD([[makeQuery(id+"F0.imprint","IMPRINT",EDGE,{"derivedFrom":sQuery(id+"F0.wireOp",EDGE,"E196")}),-1.0]])]});
            var Q190;
            Q190=makeQuery(id+"F0.imprint","IMPRINT",FACE,{"disambiguationData":[TD([[makeQuery(id+"F0.imprint","IMPRINT",EDGE,{"derivedFrom":sQuery(id+"F0.wireOp",EDGE,"E296")}),-1.0]])]});
            var Q191;
            Q191=makeQuery(id+"F0.imprint","IMPRINT",FACE,{"disambiguationData":[TD([[makeQuery(id+"F0.imprint","IMPRINT",EDGE,{"derivedFrom":sQuery(id+"F0.wireOp",EDGE,"E396")}),-1.0]])]});
            var Q192;
            Q192=makeQuery(id+"F0.imprint","IMPRINT",FACE,{"disambiguationData":[TD([[makeQuery(id+"F0.imprint","IMPRINT",EDGE,{"derivedFrom":sQuery(id+"F0.wireOp",EDGE,"E496")}),-1.0]])]});
            var Q193;
            Q193=makeQuery(id+"F0.imprint","IMPRINT",FACE,{"disambiguationData":[TD([[makeQuery(id+"F0.imprint","IMPRINT",EDGE,{"derivedFrom":sQuery(id+"F0.wireOp",EDGE,"E736")}),-1.0]])]});
            var Q194;
            Q194=makeQuery(id+"F0.imprint","IMPRINT",FACE,{"disambiguationData":[TD([[makeQuery(id+"F0.imprint","IMPRINT",EDGE,{"derivedFrom":sQuery(id+"F0.wireOp",EDGE,"E636")}),-1.0]])]});
            var Q195;
            Q195=makeQuery(id+"F0.imprint","IMPRINT",FACE,{"disambiguationData":[TD([[makeQuery(id+"F0.imprint","IMPRINT",EDGE,{"derivedFrom":sQuery(id+"F0.wireOp",EDGE,"E536")}),-1.0]])]});
            var Q196;
            Q196=makeQuery(id+"F0.imprint","IMPRINT",FACE,{"disambiguationData":[TD([[makeQuery(id+"F0.imprint","IMPRINT",EDGE,{"derivedFrom":sQuery(id+"F0.wireOp",EDGE,"E556")}),-1.0]])]});
            var Q197;
            Q197=makeQuery(id+"F0.imprint","IMPRINT",FACE,{"disambiguationData":[TD([[makeQuery(id+"F0.imprint","IMPRINT",EDGE,{"derivedFrom":sQuery(id+"F0.wireOp",EDGE,"E656")}),-1.0]])]});
            var Q198;
            Q198=makeQuery(id+"F0.imprint","IMPRINT",FACE,{"disambiguationData":[TD([[makeQuery(id+"F0.imprint","IMPRINT",EDGE,{"derivedFrom":sQuery(id+"F0.wireOp",EDGE,"E756")}),-1.0]])]});
            var Q199;
            Q199=makeQuery(id+"F0.imprint","IMPRINT",FACE,{"disambiguationData":[TD([[makeQuery(id+"F0.imprint","IMPRINT",EDGE,{"derivedFrom":sQuery(id+"F0.wireOp",EDGE,"E888")}),-1.0]])]});
            var Q200;
            Q200=makeQuery(id+"F0.imprint","IMPRINT",FACE,{"disambiguationData":[TD([[makeQuery(id+"F0.imprint","IMPRINT",EDGE,{"derivedFrom":sQuery(id+"F0.wireOp",EDGE,"E868")}),-1.0]])]});
            var Q201;
            Q201=makeQuery(id+"F0.imprint","IMPRINT",FACE,{"disambiguationData":[TD([[makeQuery(id+"F0.imprint","IMPRINT",EDGE,{"derivedFrom":sQuery(id+"F0.wireOp",EDGE,"E848")}),-1.0]])]});
            var Q202;
            Q202=makeQuery(id+"F0.imprint","IMPRINT",FACE,{"disambiguationData":[TD([[makeQuery(id+"F0.imprint","IMPRINT",EDGE,{"derivedFrom":sQuery(id+"F0.wireOp",EDGE,"E716")}),-1.0]])]});
            var Q203;
            Q203=makeQuery(id+"F0.imprint","IMPRINT",FACE,{"disambiguationData":[TD([[makeQuery(id+"F0.imprint","IMPRINT",EDGE,{"derivedFrom":sQuery(id+"F0.wireOp",EDGE,"E616")}),-1.0]])]});
            var Q204;
            Q204=makeQuery(id+"F0.imprint","IMPRINT",FACE,{"disambiguationData":[TD([[makeQuery(id+"F0.imprint","IMPRINT",EDGE,{"derivedFrom":sQuery(id+"F0.wireOp",EDGE,"E516")}),-1.0]])]});
            var Q205;
            Q205=makeQuery(id+"F0.imprint","IMPRINT",FACE,{"disambiguationData":[TD([[makeQuery(id+"F0.imprint","IMPRINT",EDGE,{"derivedFrom":sQuery(id+"F0.wireOp",EDGE,"E576")}),-1.0]])]});
            var Q206;
            Q206=makeQuery(id+"F0.imprint","IMPRINT",FACE,{"disambiguationData":[TD([[makeQuery(id+"F0.imprint","IMPRINT",EDGE,{"derivedFrom":sQuery(id+"F0.wireOp",EDGE,"E676")}),-1.0]])]});
            var Q207;
            Q207=makeQuery(id+"F0.imprint","IMPRINT",FACE,{"disambiguationData":[TD([[makeQuery(id+"F0.imprint","IMPRINT",EDGE,{"derivedFrom":sQuery(id+"F0.wireOp",EDGE,"E776")}),-1.0]])]});
            var Q208;
            Q208=makeQuery(id+"F0.imprint","IMPRINT",FACE,{"disambiguationData":[TD([[makeQuery(id+"F0.imprint","IMPRINT",EDGE,{"derivedFrom":sQuery(id+"F0.wireOp",EDGE,"E908")}),-1.0]])]});
            var Q209;
            {var subQ2=sQuery(id+"F0.wireOp",EDGE,"E797");Q209=makeQuery(id+"F0.imprint","IMPRINT",FACE,{"disambiguationData":[TD([[makeQuery(id+"F0.imprint","IMPRINT",EDGE,{"derivedFrom":subQ2}),-1.0]])]});}
            var Q210;
            Q210=makeQuery(id+"F0.imprint","IMPRINT",FACE,{"disambiguationData":[TD([[makeQuery(id+"F0.imprint","IMPRINT",EDGE,{"derivedFrom":sQuery(id+"F0.wireOp",EDGE,"E696")}),-1.0]])]});
            var Q211;
            Q211=makeQuery(id+"F0.imprint","IMPRINT",FACE,{"disambiguationData":[TD([[makeQuery(id+"F0.imprint","IMPRINT",EDGE,{"derivedFrom":sQuery(id+"F0.wireOp",EDGE,"E596")}),-1.0]])]});
            var Q212;
            {var subQ0=sQuery(id+"F0.wireOp",EDGE,"E845");Q212=makeQuery(id+"F0.imprint","IMPRINT",FACE,{"disambiguationData":[TD([[makeQuery(id+"F0.imprint","IMPRINT",EDGE,{"derivedFrom":subQ0}),-1.0]])]});}
            extrude(context, id + "F1", {"entities" : qUnion([Q0, Q1, Q2, Q3, Q4, Q5, Q6, Q7, Q8, Q9, Q10, Q11, Q12, Q13, Q14, Q15, Q16, Q17, Q18, Q19, Q20, Q21, Q22, Q23, Q24, Q25, Q26, Q27, Q28, Q29, Q30, Q31, Q32, Q33, Q34, Q35, Q36, Q37, Q38, Q39, Q40, Q41, Q42, Q43, Q44, Q45, Q46, Q47, Q48, Q49, Q50, Q51, Q52, Q53, Q54, Q55, Q56, Q57, Q58, Q59, Q60, Q61, Q62, Q63, Q64, Q65, Q66, Q67, Q68, Q69, Q70, Q71, Q72, Q73, Q74, Q75, Q76, Q77, Q78, Q79, Q80, Q81, Q82, Q83, Q84, Q85, Q86, Q87, Q88, Q89, Q90, Q91, Q92, Q93, Q94, Q95, Q96, Q97, Q98, Q99, Q100, Q101, Q102, Q103, Q104, Q105, Q106, Q107, Q108, Q109, Q110, Q111, Q112, Q113, Q114, Q115, Q116, Q117, Q118, Q119, Q120, Q121, Q122, Q123, Q124, Q125, Q126, Q127, Q128, Q129, Q130, Q131, Q132, Q133, Q134, Q135, Q136, Q137, Q138, Q139, Q140, Q141, Q142, Q143, Q144, Q145, Q146, Q147, Q148, Q149, Q150, Q151, Q152, Q153, Q154, Q155, Q156, Q157, Q158, Q159, Q160, Q161, Q162, Q163, Q164, Q165, Q166, Q167, Q168, Q169, Q170, Q171, Q172, Q173, Q174, Q175, Q176, Q177, Q178, Q179, Q180, Q181, Q182, Q183, Q184, Q185, Q186, Q187, Q188, Q189, Q190, Q191, Q192, Q193, Q194, Q195, Q196, Q197, Q198, Q199, Q200, Q201, Q202, Q203, Q204, Q205, Q206, Q207, Q208, Q209, Q210, Q211, Q212]), "depth" : 5 * mm});
        }
        {
            var Q0;
            Q0=makeQuery(id+"F1.opExtrude","CAP_FACE",FACE,{"disambiguationData":[OSD([sQuery(id+"F0.wireOp",EDGE,"E0"),sQuery(id+"F0.wireOp",EDGE,"E1"),sQuery(id+"F0.wireOp",EDGE,"E2"),sQuery(id+"F0.wireOp",EDGE,"E3"),sQuery(id+"F0.wireOp",EDGE,"E845"),sQuery(id+"F0.wireOp",EDGE,"E846"),sQuery(id+"F0.wireOp",EDGE,"E847"),sQuery(id+"F0.wireOp",EDGE,"E969.right")])],"isStart":false});
            var sketch = newSketch(context, id + "F2", { "sketchPlane" : qUnion([Q0])});
            skCircle(sketch, "E971", {"center": v(-86.43, -55.47) * mm, "radius": 1.8 * mm});
            skCircle(sketch, "E972", {"center": v(-86.43, -55.47) * mm, "radius": 1 * mm});
            skCircle(sketch, "E973", {"center": v(86.43, -55.47) * mm, "radius": 1.8 * mm});
            skCircle(sketch, "E974", {"center": v(86.43, -55.47) * mm, "radius": 1 * mm});
            skCircle(sketch, "E975", {"center": v(86.43, 55.47) * mm, "radius": 1.8 * mm});
            skCircle(sketch, "E976", {"center": v(86.43, 55.47) * mm, "radius": 1 * mm});
            skCircle(sketch, "E977", {"center": v(-86.43, 55.47) * mm, "radius": 1.8 * mm});
            skCircle(sketch, "E978", {"center": v(-86.43, 55.47) * mm, "radius": 1 * mm});
            skCircle(sketch, "E979", {"center": v(0, 7.15) * mm, "radius": 1.8 * mm});
            skCircle(sketch, "E980", {"center": v(0, 7.15) * mm, "radius": 1 * mm});
            skCircle(sketch, "E981", {"center": v(47.63, -7.14) * mm, "radius": 1.8 * mm});
            skPoint(sketch, "E981.centerSnap0", {"position": v(45.9, -7.14) * mm});
            skCircle(sketch, "E982", {"center": v(47.63, -7.14) * mm, "radius": 1 * mm});
            skCircle(sketch, "E983", {"center": v(-47.7, -2.38) * mm, "radius": 1.8 * mm});
            skPoint(sketch, "E983.centerSnap0", {"position": v(-49.35, -2.38) * mm});
            skCircle(sketch, "E984", {"center": v(-47.7, -2.38) * mm, "radius": 1 * mm});
            skCircle(sketch, "E985", {"center": v(-47.7, 55.47) * mm, "radius": 1.8 * mm});
            skCircle(sketch, "E986", {"center": v(-47.7, 55.47) * mm, "radius": 1 * mm});
            skCircle(sketch, "E987", {"center": v(-47.7, -55.47) * mm, "radius": 1.8 * mm});
            skCircle(sketch, "E988", {"center": v(-47.7, -55.47) * mm, "radius": 1 * mm});
            skCircle(sketch, "E989", {"center": v(0, 55.47) * mm, "radius": 1.8 * mm});
            skCircle(sketch, "E990", {"center": v(0, 55.47) * mm, "radius": 1 * mm});
            skCircle(sketch, "E991", {"center": v(0, -55.47) * mm, "radius": 1.8 * mm});
            skPoint(sketch, "E991.centerSnap0", {"position": v(0, -59.77) * mm});
            skCircle(sketch, "E992", {"center": v(0, -55.47) * mm, "radius": 1 * mm});
            skCircle(sketch, "E993", {"center": v(47.63, 55.47) * mm, "radius": 1.8 * mm});
            skCircle(sketch, "E994", {"center": v(47.63, 55.47) * mm, "radius": 1 * mm});
            skCircle(sketch, "E995", {"center": v(47.63, -55.47) * mm, "radius": 1.8 * mm});
            skCircle(sketch, "E996", {"center": v(47.63, -55.47) * mm, "radius": 1 * mm});
            skCircle(sketch, "E997", {"center": v(-86.43, 2.38) * mm, "radius": 1.8 * mm});
            skCircle(sketch, "E998", {"center": v(-86.43, 2.38) * mm, "radius": 1 * mm});
            skCircle(sketch, "E999", {"center": v(86.43, 2.38) * mm, "radius": 1.8 * mm});
            skCircle(sketch, "E1000", {"center": v(86.43, 2.38) * mm, "radius": 1 * mm});
            skSolve(sketch);
        }
        {
            var Q0;
            {var subQ0=sQuery(id+"F0.wireOp",EDGE,"E3");var subQ1=sQuery(id+"F0.wireOp",EDGE,"E2");Q0=makeQuery(id+"FlM27Dyb4vpNypC_1.boolean.opBoolean","MERGE",EDGE,{"derivedFrom":[makeQuery(id+"F1.opExtrude","SWEPT_EDGE",EDGE,{"disambiguationData":[OSD([subQ1,subQ0])]}),makeQuery(id+"FlM27Dyb4vpNypC_1.opExtrude","SWEPT_EDGE",EDGE,{"disambiguationData":[OSD([subQ1,subQ0])]})]});}
            var Q1;
            {var subQ0=sQuery(id+"F0.wireOp",EDGE,"E3");var subQ1=sQuery(id+"F0.wireOp",EDGE,"E0");Q1=makeQuery(id+"FlM27Dyb4vpNypC_1.boolean.opBoolean","MERGE",EDGE,{"derivedFrom":[makeQuery(id+"F1.opExtrude","SWEPT_EDGE",EDGE,{"disambiguationData":[OSD([subQ1,subQ0])]}),makeQuery(id+"FlM27Dyb4vpNypC_1.opExtrude","SWEPT_EDGE",EDGE,{"disambiguationData":[OSD([subQ1,subQ0])]})]});}
            var Q2;
            {var subQ0=sQuery(id+"F0.wireOp",EDGE,"E1");var subQ1=sQuery(id+"F0.wireOp",EDGE,"E0");Q2=makeQuery(id+"FlM27Dyb4vpNypC_1.boolean.opBoolean","MERGE",EDGE,{"derivedFrom":[makeQuery(id+"F1.opExtrude","SWEPT_EDGE",EDGE,{"disambiguationData":[OSD([subQ1,subQ0])]}),makeQuery(id+"FlM27Dyb4vpNypC_1.opExtrude","SWEPT_EDGE",EDGE,{"disambiguationData":[OSD([subQ1,subQ0])]})]});}
            var Q3;
            {var subQ0=sQuery(id+"F0.wireOp",EDGE,"E2");var subQ1=sQuery(id+"F0.wireOp",EDGE,"E1");Q3=makeQuery(id+"FlM27Dyb4vpNypC_1.boolean.opBoolean","MERGE",EDGE,{"derivedFrom":[makeQuery(id+"F1.opExtrude","SWEPT_EDGE",EDGE,{"disambiguationData":[OSD([subQ1,subQ0])]}),makeQuery(id+"FlM27Dyb4vpNypC_1.opExtrude","SWEPT_EDGE",EDGE,{"disambiguationData":[OSD([subQ1,subQ0])]})]});}
            fillet(context, id + "F3", {"entities" : qUnion([Q0, Q1, Q2, Q3]), "radius" : 5 * mm, "tangentPropagation" : true, "allowEdgeOverflow" : false});
        }
        {
            var Q0;
            Q0=makeQuery(id+"F2.imprint","IMPRINT",FACE,{"disambiguationData":[TD([[makeQuery(id+"F2.imprint","IMPRINT",EDGE,{"derivedFrom":sQuery(id+"F2.wireOp",EDGE,"E974")}),1.0]])]});
            var Q1;
            Q1=makeQuery(id+"F2.imprint","IMPRINT",FACE,{"disambiguationData":[TD([[makeQuery(id+"F2.imprint","IMPRINT",EDGE,{"derivedFrom":sQuery(id+"F2.wireOp",EDGE,"E976")}),1.0]])]});
            var Q2;
            Q2=makeQuery(id+"F2.imprint","IMPRINT",FACE,{"disambiguationData":[TD([[makeQuery(id+"F2.imprint","IMPRINT",EDGE,{"derivedFrom":sQuery(id+"F2.wireOp",EDGE,"E978")}),1.0]])]});
            var Q3;
            Q3=makeQuery(id+"F2.imprint","IMPRINT",FACE,{"disambiguationData":[TD([[makeQuery(id+"F2.imprint","IMPRINT",EDGE,{"derivedFrom":sQuery(id+"F2.wireOp",EDGE,"E972")}),1.0]])]});
            var Q4;
            Q4=makeQuery(id+"F2.imprint","IMPRINT",FACE,{"disambiguationData":[TD([[makeQuery(id+"F2.imprint","IMPRINT",EDGE,{"derivedFrom":sQuery(id+"F2.wireOp",EDGE,"E980")}),1.0]])]});
            var Q5;
            Q5=makeQuery(id+"F2.imprint","IMPRINT",FACE,{"disambiguationData":[TD([[makeQuery(id+"F2.imprint","IMPRINT",EDGE,{"derivedFrom":sQuery(id+"F2.wireOp",EDGE,"ujkoGJg9-zatk-nCZ3-epMn-KVPZoMVvY8ag")}),1.0]])]});
            var Q6;
            Q6=makeQuery(id+"F2.imprint","IMPRINT",FACE,{"disambiguationData":[TD([[makeQuery(id+"F2.imprint","IMPRINT",EDGE,{"derivedFrom":sQuery(id+"F2.wireOp",EDGE,"E982")}),1.0]])]});
            var Q7;
            Q7=makeQuery(id+"F2.imprint","IMPRINT",FACE,{"disambiguationData":[TD([[makeQuery(id+"F2.imprint","IMPRINT",EDGE,{"derivedFrom":sQuery(id+"F2.wireOp",EDGE,"E990")}),1.0]])]});
            var Q8;
            Q8=makeQuery(id+"F2.imprint","IMPRINT",FACE,{"disambiguationData":[TD([[makeQuery(id+"F2.imprint","IMPRINT",EDGE,{"derivedFrom":sQuery(id+"F2.wireOp",EDGE,"E984")}),1.0]])]});
            var Q9;
            Q9=makeQuery(id+"F2.imprint","IMPRINT",FACE,{"disambiguationData":[TD([[makeQuery(id+"F2.imprint","IMPRINT",EDGE,{"derivedFrom":sQuery(id+"F2.wireOp",EDGE,"E992")}),1.0]])]});
            var Q10;
            Q10=makeQuery(id+"F2.imprint","IMPRINT",FACE,{"disambiguationData":[TD([[makeQuery(id+"F2.imprint","IMPRINT",EDGE,{"derivedFrom":sQuery(id+"F2.wireOp",EDGE,"E1000")}),1.0]])]});
            var Q11;
            Q11=makeQuery(id+"F2.imprint","IMPRINT",FACE,{"disambiguationData":[TD([[makeQuery(id+"F2.imprint","IMPRINT",EDGE,{"derivedFrom":sQuery(id+"F2.wireOp",EDGE,"E998")}),1.0]])]});
            extrude(context, id + "F4", {"entities" : qUnion([Q0, Q1, Q2, Q3, Q4, Q5, Q6, Q7, Q8, Q9, Q10, Q11]), "operationType" : NewBodyOperationType.REMOVE, "oppositeDirection" : true, "depth" : 5 * mm});
        }
        {
            var Q0;
            Q0=makeQuery(id+"F1.opExtrude","CAP_FACE",FACE,{"disambiguationData":[OSD([sQuery(id+"F0.wireOp",EDGE,"E0"),sQuery(id+"F0.wireOp",EDGE,"E1"),sQuery(id+"F0.wireOp",EDGE,"E2"),sQuery(id+"F0.wireOp",EDGE,"E3")])],"isStart":true});
            var sketch = newSketch(context, id + "F5", { "sketchPlane" : qUnion([Q0])});
            skCircle(sketch, "E1001", {"center": v(-86.43, 55.47) * mm, "radius": 1.8 * mm});
            skCircle(sketch, "E1002", {"center": v(-86.43, 55.47) * mm, "radius": 1 * mm});
            skCircle(sketch, "E1003", {"center": v(0, 55.47) * mm, "radius": 1.8 * mm});
            skCircle(sketch, "E1004", {"center": v(-86.43, -2.38) * mm, "radius": 1.8 * mm});
            skCircle(sketch, "E1005", {"center": v(-86.43, -2.38) * mm, "radius": 1 * mm});
            skCircle(sketch, "E1006", {"center": v(-86.43, -55.47) * mm, "radius": 1.8 * mm});
            skCircle(sketch, "E1007", {"center": v(-47.7, 2.38) * mm, "radius": 1.8 * mm});
            skCircle(sketch, "E1008", {"center": v(0, -7.15) * mm, "radius": 1.8 * mm});
            skCircle(sketch, "E1009", {"center": v(0, -55.47) * mm, "radius": 1.8 * mm});
            skCircle(sketch, "E1010", {"center": v(47.63, 7.14) * mm, "radius": 1.8 * mm});
            skCircle(sketch, "E1011", {"center": v(86.43, 55.47) * mm, "radius": 1.8 * mm});
            skCircle(sketch, "E1012", {"center": v(86.43, -2.38) * mm, "radius": 1.8 * mm});
            skCircle(sketch, "E1013", {"center": v(86.43, -55.47) * mm, "radius": 1.8 * mm});
            skCircle(sketch, "E1014", {"center": v(-47.7, 2.38) * mm, "radius": 1 * mm});
            skCircle(sketch, "E1015", {"center": v(0, 55.47) * mm, "radius": 1 * mm});
            skCircle(sketch, "E1016", {"center": v(0, -7.15) * mm, "radius": 1 * mm});
            skCircle(sketch, "E1017", {"center": v(0, -55.47) * mm, "radius": 1 * mm});
            skCircle(sketch, "E1018", {"center": v(47.63, 7.14) * mm, "radius": 1 * mm});
            skCircle(sketch, "E1019", {"center": v(86.43, 55.47) * mm, "radius": 1 * mm});
            skCircle(sketch, "E1020", {"center": v(86.43, -2.38) * mm, "radius": 1 * mm});
            skCircle(sketch, "E1021", {"center": v(86.43, -55.47) * mm, "radius": 1 * mm});
            skSolve(sketch);
        }
        {
            var Q0;
            Q0=makeQuery(id+"F5.imprint","IMPRINT",FACE,{"disambiguationData":[TD([[makeQuery(id+"F5.imprint","IMPRINT",EDGE,{"derivedFrom":sQuery(id+"F5.wireOp",EDGE,"E1001")}),1.0]])]});
            var Q1;
            Q1=makeQuery(id+"F5.imprint","IMPRINT",FACE,{"disambiguationData":[TD([[makeQuery(id+"F5.imprint","IMPRINT",EDGE,{"derivedFrom":sQuery(id+"F5.wireOp",EDGE,"E1004")}),1.0]])]});
            var Q2;
            Q2=makeQuery(id+"F5.imprint","IMPRINT",FACE,{"disambiguationData":[TD([[makeQuery(id+"F5.imprint","IMPRINT",EDGE,{"derivedFrom":sQuery(id+"F5.wireOp",EDGE,"E1003")}),1.0]])]});
            var Q3;
            Q3=makeQuery(id+"F5.imprint","IMPRINT",FACE,{"disambiguationData":[TD([[makeQuery(id+"F5.imprint","IMPRINT",EDGE,{"derivedFrom":sQuery(id+"F5.wireOp",EDGE,"E1006")}),1.0]])]});
            var Q4;
            Q4=makeQuery(id+"F5.imprint","IMPRINT",FACE,{"disambiguationData":[TD([[makeQuery(id+"F5.imprint","IMPRINT",EDGE,{"derivedFrom":sQuery(id+"F5.wireOp",EDGE,"E1009")}),1.0]])]});
            var Q5;
            Q5=makeQuery(id+"F5.imprint","IMPRINT",FACE,{"disambiguationData":[TD([[makeQuery(id+"F5.imprint","IMPRINT",EDGE,{"derivedFrom":sQuery(id+"F5.wireOp",EDGE,"E1008")}),1.0]])]});
            var Q6;
            Q6=makeQuery(id+"F5.imprint","IMPRINT",FACE,{"disambiguationData":[TD([[makeQuery(id+"F5.imprint","IMPRINT",EDGE,{"derivedFrom":sQuery(id+"F5.wireOp",EDGE,"E1012")}),1.0]])]});
            var Q7;
            Q7=makeQuery(id+"F5.imprint","IMPRINT",FACE,{"disambiguationData":[TD([[makeQuery(id+"F5.imprint","IMPRINT",EDGE,{"derivedFrom":sQuery(id+"F5.wireOp",EDGE,"E1013")}),1.0]])]});
            var Q8;
            Q8=makeQuery(id+"F5.imprint","IMPRINT",FACE,{"disambiguationData":[TD([[makeQuery(id+"F5.imprint","IMPRINT",EDGE,{"derivedFrom":sQuery(id+"F5.wireOp",EDGE,"E1011")}),1.0]])]});
            var Q9;
            Q9=makeQuery(id+"F5.imprint","IMPRINT",FACE,{"disambiguationData":[TD([[makeQuery(id+"F5.imprint","IMPRINT",EDGE,{"derivedFrom":sQuery(id+"F5.wireOp",EDGE,"E1007")}),1.0]])]});
            var Q10;
            Q10=makeQuery(id+"F5.imprint","IMPRINT",FACE,{"disambiguationData":[TD([[makeQuery(id+"F5.imprint","IMPRINT",EDGE,{"derivedFrom":sQuery(id+"F5.wireOp",EDGE,"E1010")}),1.0]])]});
            extrude(context, id + "F6", {"entities" : qUnion([Q0, Q1, Q2, Q3, Q4, Q5, Q6, Q7, Q8, Q9, Q10]), "operationType" : NewBodyOperationType.REMOVE, "oppositeDirection" : true, "depth" : 2.5 * mm});
        }
    });
